FCSTD DOCUMENT  (FreeCAD 1.0R39319 (Git))
Label: lithography
License: All rights reserved
objects: App::Link×141, App::FeaturePython×32, Assembly::AssemblyLink×2, Assembly::JointGroup×1, Assembly::AssemblyObject×1
EXTERNAL_REF file=frame/frame.FCStd obj=Assembly
EXTERNAL_REF file=frame/frame.FCStd obj=_0x30_450_v3
EXTERNAL_REF file=frame/frame.FCStd obj=_0x30_550_v6
EXTERNAL_REF file=frame/frame.FCStd obj=_0x30_450
EXTERNAL_REF file=frame/frame.FCStd obj=_0x30_551
EXTERNAL_REF file=frame/frame.FCStd obj=_0x30_552
EXTERNAL_REF file=frame/frame.FCStd obj=_0x30_550
EXTERNAL_REF file=frame/frame.FCStd obj=_0x30_450_001
EXTERNAL_REF file=frame/frame.FCStd obj=_0x30_450_002
EXTERNAL_REF file=frame/frame.FCStd obj=_0x30_550_001
EXTERNAL_REF file=frame/frame.FCStd obj=_0x30_550_002
EXTERNAL_REF file=frame/frame.FCStd obj=_0x30_450_003
EXTERNAL_REF file=frame/frame.FCStd obj=_0x30_450_004
EXTERNAL_REF file=frame/frame.FCStd obj=_0_30_ANGLE_BRACKET_001
EXTERNAL_REF file=frame/frame.FCStd obj=_0_30_ANGLE_BRACKET_002
EXTERNAL_REF file=frame/frame.FCStd obj=_0_30_ANGLE_BRACKET_003
EXTERNAL_REF file=frame/frame.FCStd obj=_0_30_ANGLE_BRACKET_004
EXTERNAL_REF file=frame/frame.FCStd obj=_0_30_ANGLE_BRACKET_005
EXTERNAL_REF file=frame/frame.FCStd obj=_0_30_ANGLE_BRACKET_006
EXTERNAL_REF file=frame/frame.FCStd obj=_0_30_ANGLE_BRACKET_007
EXTERNAL_REF file=frame/frame.FCStd obj=_0_30_ANGLE_BRACKET_008
EXTERNAL_REF file=frame/frame.FCStd obj=_0_30_ANGLE_BRACKET_009
EXTERNAL_REF file=frame/frame.FCStd obj=_0_30_ANGLE_BRACKET_010
EXTERNAL_REF file=frame/frame.FCStd obj=_0_30_ANGLE_BRACKET_011
EXTERNAL_REF file=frame/frame.FCStd obj=_0_30_ANGLE_BRACKET_012
EXTERNAL_REF file=frame/frame.FCStd obj=_0_30_ANGLE_BRACKET_013
EXTERNAL_REF file=frame/frame.FCStd obj=_0_30_ANGLE_BRACKET_014
EXTERNAL_REF file=frame/frame.FCStd obj=_0_30_ANGLE_BRACKET_015
EXTERNAL_REF file=frame/frame.FCStd obj=_0_30_ANGLE_BRACKET_016
EXTERNAL_REF file=frame/frame.FCStd obj=_0_30_ANGLE_BRACKET_017
EXTERNAL_REF file=frame/frame.FCStd obj=_0_30_ANGLE_BRACKET_018
EXTERNAL_REF file=frame/frame.FCStd obj=_0_30_ANGLE_BRACKET_019
EXTERNAL_REF file=frame/frame.FCStd obj=_0_30_ANGLE_BRACKET_020
EXTERNAL_REF file=frame/frame.FCStd obj=_0_30_ANGLE_BRACKET_021
EXTERNAL_REF file=frame/frame.FCStd obj=_0_30_ANGLE_BRACKET_022
EXTERNAL_REF file=frame/frame.FCStd obj=_0_30_ANGLE_BRACKET_023
EXTERNAL_REF file=frame/frame.FCStd obj=_0_30_ANGLE_BRACKET_024
EXTERNAL_REF file=frame/frame.FCStd obj=_0x30_450_005
EXTERNAL_REF file=frame/frame.FCStd obj=_0x30_270_001
EXTERNAL_REF file=frame/frame.FCStd obj=_0x30_270_002
EXTERNAL_REF file=frame/frame.FCStd obj=_0x30_450_006
EXTERNAL_REF file=frame/frame.FCStd obj=_0x30_450_007
EXTERNAL_REF file=frame/frame.FCStd obj=_0x30_450_008
EXTERNAL_REF file=frame/frame.FCStd obj=_0_30_ANGLE_BRACKET_025
EXTERNAL_REF file=frame/frame.FCStd obj=_0_30_ANGLE_BRACKET_026
EXTERNAL_REF file=frame/frame.FCStd obj=_0_30_ANGLE_BRACKET_027
EXTERNAL_REF file=frame/frame.FCStd obj=_0_30_ANGLE_BRACKET_028
EXTERNAL_REF file=frame/frame.FCStd obj=_0_30_ANGLE_BRACKET_029
EXTERNAL_REF file=frame/frame.FCStd obj=_0_30_ANGLE_BRACKET_030
EXTERNAL_REF file=frame/frame.FCStd obj=_0_30_ANGLE_BRACKET_031
EXTERNAL_REF file=frame/frame.FCStd obj=_0_30_ANGLE_BRACKET_032
EXTERNAL_REF file=frame/frame.FCStd obj=_0x30_450_009
EXTERNAL_REF file=frame/frame.FCStd obj=_0x30_450_010
EXTERNAL_REF file=frame/frame.FCStd obj=_0_30_ANGLE_BRACKET_033
EXTERNAL_REF file=frame/frame.FCStd obj=_0_30_ANGLE_BRACKET_034
EXTERNAL_REF file=frame/frame.FCStd obj=_0_30_ANGLE_BRACKET_035
EXTERNAL_REF file=frame/frame.FCStd obj=_0_30_ANGLE_BRACKET_036
EXTERNAL_REF file=frame/frame.FCStd obj=_0_30_ANGLE_BRACKET_037
EXTERNAL_REF file=frame/frame.FCStd obj=_0_30_ANGLE_BRACKET_038
EXTERNAL_REF file=frame/frame.FCStd obj=_0_30_ANGLE_BRACKET_039
EXTERNAL_REF file=frame/frame.FCStd obj=_0_30_ANGLE_BRACKET_040
EXTERNAL_REF file=frame/frame.FCStd obj=_0_30_ANGLE_BRACKET_041
EXTERNAL_REF file=frame/frame.FCStd obj=_0_30_ANGLE_BRACKET_042
EXTERNAL_REF file=frame/frame.FCStd obj=_0_30_ANGLE_BRACKET_043
EXTERNAL_REF file=frame/frame.FCStd obj=_0_30_ANGLE_BRACKET_044
EXTERNAL_REF file=frame/frame.FCStd obj=_0x30_450_011
EXTERNAL_REF file=frame/frame.FCStd obj=_0_30_ANGLE_BRACKET_045
EXTERNAL_REF file=frame/frame.FCStd obj=_0_30_ANGLE_BRACKET_046
EXTERNAL_REF file=panels/plexi.FCStd obj=Part
EXTERNAL_REF file=panels/plexi.FCStd obj=Part002
EXTERNAL_REF file=panels/plexi-mount.FCStd obj=Part001
EXTERNAL_REF file=panels/plexi-mount.FCStd obj=Part
EXTERNAL_REF file=panels/plexi.FCStd obj=Part003
EXTERNAL_REF file=panels/plexi.FCStd obj=Part004
EXTERNAL_REF file=panels/plexi.FCStd obj=Part001
EXTERNAL_REF file=panels/plexi.FCStd obj=Part005
EXTERNAL_REF file=panels/plexi.FCStd obj=Part006
EXTERNAL_REF file=panels/plexi.FCStd obj=Part007
EXTERNAL_REF file=panels/plexi.FCStd obj=Part008
EXTERNAL_REF file=panels/plexi.FCStd obj=Part009
EXTERNAL_REF file=electronics/electronics-box.FCStd obj=Assembly
EXTERNAL_REF file=electronics/electronics-box.FCStd obj=alu_prof_3030_300_000
EXTERNAL_REF file=electronics/electronics-box.FCStd obj=alu_prof_3030_450_000
EXTERNAL_REF file=electronics/electronics-box.FCStd obj=alu_prof_3030_300_001
EXTERNAL_REF file=electronics/electronics-box.FCStd obj=alu_prof_3030_200_000
EXTERNAL_REF file=electronics/electronics-box.FCStd obj=alu_prof_3030_200_001
EXTERNAL_REF file=electronics/electronics-box.FCStd obj=alu_prof_3030_200_002
EXTERNAL_REF file=electronics/electronics-box.FCStd obj=alu_prof_3030_200_003
EXTERNAL_REF file=electronics/electronics-box.FCStd obj=alu_prof_3030_450_003
EXTERNAL_REF file=electronics/electronics-box.FCStd obj=_030_angle_bracket_000
EXTERNAL_REF file=electronics/electronics-box.FCStd obj=_030_angle_bracket_001
EXTERNAL_REF file=electronics/electronics-box.FCStd obj=_030_angle_bracket_002
EXTERNAL_REF file=electronics/electronics-box.FCStd obj=_030_angle_bracket_003
EXTERNAL_REF file=electronics/electronics-box.FCStd obj=_030_angle_bracket_004
EXTERNAL_REF file=electronics/electronics-box.FCStd obj=_030_angle_bracket_005
EXTERNAL_REF file=electronics/electronics-box.FCStd obj=_030_angle_bracket_006
EXTERNAL_REF file=electronics/electronics-box.FCStd obj=_030_angle_bracket_007
EXTERNAL_REF file=electronics/electronics-box.FCStd obj=_030_angle_bracket_008
EXTERNAL_REF file=electronics/electronics-box.FCStd obj=_030_angle_bracket_009
EXTERNAL_REF file=electronics/electronics-box.FCStd obj=_030_angle_bracket_010
EXTERNAL_REF file=electronics/electronics-box.FCStd obj=_030_angle_bracket_011
EXTERNAL_REF file=electronics/electronics-box.FCStd obj=_030_angle_bracket_012
EXTERNAL_REF file=electronics/electronics-box.FCStd obj=_030_angle_bracket_013
EXTERNAL_REF file=electronics/electronics-box.FCStd obj=_030_angle_bracket_014
EXTERNAL_REF file=electronics/electronics-box.FCStd obj=_030_angle_bracket_015
EXTERNAL_REF file=electronics/electronics-box.FCStd obj=din_mount_part
EXTERNAL_REF file=electronics/electronics-box.FCStd obj=din_mount_part001
EXTERNAL_REF file=electronics/electronics-box.FCStd obj=din_rail_180mm
EXTERNAL_REF file=electronics/electronics-box.FCStd obj=alu_prof_3030_450_004
EXTERNAL_REF file=electronics/electronics-box.FCStd obj=_030_angle_bracket_016
EXTERNAL_REF file=electronics/electronics-box.FCStd obj=_030_angle_bracket_017
EXTERNAL_REF file=electronics/electronics-box.FCStd obj=power_supply_bracket_part
EXTERNAL_REF file=electronics/electronics-box.FCStd obj=power_supply_bracket_part001
EXTERNAL_REF file=electronics/electronics-box.FCStd obj=LRS_154
EXTERNAL_REF file=electronics/electronics-box.FCStd obj=LRS_155
EXTERNAL_REF file=electronics/electronics-box.FCStd obj=dlp_power_supply_bracket_part
EXTERNAL_REF file=electronics/electronics-box.FCStd obj=smc100c_bracket_part
EXTERNAL_REF file=electronics/electronics-box.FCStd obj=smc100c_bracket_part001
EXTERNAL_REF file=electronics/electronics-box.FCStd obj=SMC100CC
EXTERNAL_REF file=electronics/electronics-box.FCStd obj=SMC100CC001
EXTERNAL_REF file=electronics/electronics-box.FCStd obj=ports_panel_part

FEATURE [App::Link] _0x30_450_v3  label="30x30 450 002"
  LinkPlacement = pos=(-180.5,79.4999,31.5001) rot=(0,1.00097,0;0rad)
  LinkedObject = -> <external frame/frame.FCStd>#_0x30_450_v3
  Placement = pos=(-180.5,79.4999,31.5001) rot=(0,1.00097,0;0rad)
FEATURE [App::Link] _0x30_550_v6  label="30x30 550 002"
  LinkPlacement = pos=(-145.5,79.4999,-33.4999) rot=(0,1,0;1.5708rad)
  LinkedObject = -> <external frame/frame.FCStd>#_0x30_550_v6
  Placement = pos=(-145.5,79.4999,-33.4999) rot=(0,1,0;1.5708rad)
FEATURE [App::Link] _0x30_450  label="30x30 450 005"
  LinkPlacement = pos=(339.5,79.4999,31.4999) rot=(0,1.00097,0;0rad)
  LinkedObject = -> <external frame/frame.FCStd>#_0x30_450
  Placement = pos=(339.5,79.4999,31.4999) rot=(0,1.00097,0;0rad)
FEATURE [App::Link] _0x30_551  label="30x30 450 003"
  LinkPlacement = pos=(339.5,494.5,-33.5001) rot=(1,0,0;1.5708rad)
  LinkedObject = -> <external frame/frame.FCStd>#_0x30_551
  Placement = pos=(339.5,494.5,-33.5001) rot=(1,0,0;1.5708rad)
FEATURE [App::Link] _0x30_552  label="30x30 450 004"
  LinkPlacement = pos=(339.5,494.5,446.5) rot=(0.57735,0.57735,-0.57735;2.0944rad)
  LinkedObject = -> <external frame/frame.FCStd>#_0x30_552
  Placement = pos=(339.5,494.5,446.5) rot=(0.57735,0.57735,-0.57735;2.0944rad)
FEATURE [App::Link] _0x30_550  label="30x30 550 003"
  LinkPlacement = pos=(304.5,79.4999,446.5) rot=(0,-1,0;1.5708rad)
  LinkedObject = -> <external frame/frame.FCStd>#_0x30_550
  Placement = pos=(304.5,79.4999,446.5) rot=(0,-1,0;1.5708rad)
FEATURE [App::Link] _0x30_450_001  label="30x30 450 006"
  LinkPlacement = pos=(-180.5,494.5,446.5) rot=(1,0,0;1.5708rad)
  LinkedObject = -> <external frame/frame.FCStd>#_0x30_450_001
  Placement = pos=(-180.5,494.5,446.5) rot=(1,0,0;1.5708rad)
FEATURE [App::Link] _0x30_450_002  label="30x30 450 007"
  LinkPlacement = pos=(-180.5,494.5,-33.4999) rot=(1,0,0;1.5708rad)
  LinkedObject = -> <external frame/frame.FCStd>#_0x30_450_002
  Placement = pos=(-180.5,494.5,-33.4999) rot=(1,0,0;1.5708rad)
FEATURE [App::Link] _0x30_550_001  label="30x30 550 004"
  LinkPlacement = pos=(-145.5,559.5,-33.4999) rot=(0,1,0;1.5708rad)
  LinkedObject = -> <external frame/frame.FCStd>#_0x30_550_001
  Placement = pos=(-145.5,559.5,-33.4999) rot=(0,1,0;1.5708rad)
FEATURE [App::Link] _0x30_550_002  label="30x30 550 005"
  LinkPlacement = pos=(304.5,559.5,446.5) rot=(0,-1,0;1.5708rad)
  LinkedObject = -> <external frame/frame.FCStd>#_0x30_550_002
  Placement = pos=(304.5,559.5,446.5) rot=(0,-1,0;1.5708rad)
FEATURE [App::Link] _0x30_450_003  label="30x30 450 008"
  LinkPlacement = pos=(339.5,559.5,31.4999) rot=(0,1.00097,0;0rad)
  LinkedObject = -> <external frame/frame.FCStd>#_0x30_450_003
  Placement = pos=(339.5,559.5,31.4999) rot=(0,1.00097,0;0rad)
FEATURE [App::Link] _0x30_450_004  label="30x30 450 009"
  LinkPlacement = pos=(-180.5,559.5,31.5001) rot=(0,1.00097,0;0rad)
  LinkedObject = -> <external frame/frame.FCStd>#_0x30_450_004
  Placement = pos=(-180.5,559.5,31.5001) rot=(0,1.00097,0;0rad)
FEATURE [App::Link] _0_30_ANGLE_BRACKET_001  label="30-30 ANGLE BRACKET 002"
  LinkPlacement = pos=(-165.5,79.2999,-0.999886) rot=(-0.57735,-0.57735,-0.57735;2.0944rad)
  LinkedObject = -> <external frame/frame.FCStd>#_0_30_ANGLE_BRACKET_001
  Placement = pos=(-165.5,79.2999,-0.999886) rot=(-0.57735,-0.57735,-0.57735;2.0944rad)
FEATURE [App::Link] _0_30_ANGLE_BRACKET_002  label="30-30 ANGLE BRACKET 003"
  LinkPlacement = pos=(-165.5,112,-33.2999) rot=(0.707107,0.707107,0;3.14159rad)
  LinkedObject = -> <external frame/frame.FCStd>#_0_30_ANGLE_BRACKET_002
  Placement = pos=(-165.5,112,-33.2999) rot=(0.707107,0.707107,0;3.14159rad)
FEATURE [App::Link] _0_30_ANGLE_BRACKET_003  label="30-30 ANGLE BRACKET 004"
  LinkPlacement = pos=(-180.7,112,-18.4999) rot=(0.57735,0.57735,0.57735;2.0944rad)
  LinkedObject = -> <external frame/frame.FCStd>#_0_30_ANGLE_BRACKET_003
  Placement = pos=(-180.7,112,-18.4999) rot=(0.57735,0.57735,0.57735;2.0944rad)
FEATURE [App::Link] _0_30_ANGLE_BRACKET_004  label="30-30 ANGLE BRACKET 005"
  LinkPlacement = pos=(-180.3,112,431.5) rot=(-0.57735,-0.57735,0.57735;2.0944rad)
  LinkedObject = -> <external frame/frame.FCStd>#_0_30_ANGLE_BRACKET_004
  Placement = pos=(-180.3,112,431.5) rot=(-0.57735,-0.57735,0.57735;2.0944rad)
FEATURE [App::Link] _0_30_ANGLE_BRACKET_005  label="30-30 ANGLE BRACKET 006"
  LinkPlacement = pos=(-180.7,544.5,-0.99988) rot=(0.707107,0,0.707107;3.14159rad)
  LinkedObject = -> <external frame/frame.FCStd>#_0_30_ANGLE_BRACKET_005
  Placement = pos=(-180.7,544.5,-0.99988) rot=(0.707107,0,0.707107;3.14159rad)
FEATURE [App::Link] _0_30_ANGLE_BRACKET_006  label="30-30 ANGLE BRACKET 007"
  LinkPlacement = pos=(-180.3,544.5,414) rot=(-0.707107,0,0.707107;3.14159rad)
  LinkedObject = -> <external frame/frame.FCStd>#_0_30_ANGLE_BRACKET_006
  Placement = pos=(-180.3,544.5,414) rot=(-0.707107,0,0.707107;3.14159rad)
FEATURE [App::Link] _0_30_ANGLE_BRACKET_007  label="30-30 ANGLE BRACKET 008"
  LinkPlacement = pos=(-165.5,79.5999,414) rot=(0.57735,0.57735,-0.57735;2.0944rad)
  LinkedObject = -> <external frame/frame.FCStd>#_0_30_ANGLE_BRACKET_007
  Placement = pos=(-165.5,79.5999,414) rot=(0.57735,0.57735,-0.57735;2.0944rad)
FEATURE [App::Link] _0_30_ANGLE_BRACKET_008  label="30-30 ANGLE BRACKET 009"
  LinkPlacement = pos=(324.5,79.2999,414) rot=(-0.57735,0.57735,0.57735;2.0944rad)
  LinkedObject = -> <external frame/frame.FCStd>#_0_30_ANGLE_BRACKET_008
  Placement = pos=(324.5,79.2999,414) rot=(-0.57735,0.57735,0.57735;2.0944rad)
FEATURE [App::Link] _0_30_ANGLE_BRACKET_009  label="30-30 ANGLE BRACKET 010"
  LinkPlacement = pos=(307,79.2999,-18.5001) rot=(0,0.707107,0.707107;3.14159rad)
  LinkedObject = -> <external frame/frame.FCStd>#_0_30_ANGLE_BRACKET_009
  Placement = pos=(307,79.2999,-18.5001) rot=(0,0.707107,0.707107;3.14159rad)
FEATURE [App::Link] _0_30_ANGLE_BRACKET_010  label="30-30 ANGLE BRACKET 011"
  LinkPlacement = pos=(307,544.5,-33.7001) rot=(0,0,1;3.14159rad)
  LinkedObject = -> <external frame/frame.FCStd>#_0_30_ANGLE_BRACKET_010
  Placement = pos=(307,544.5,-33.7001) rot=(0,0,1;3.14159rad)
FEATURE [App::Link] _0_30_ANGLE_BRACKET_011  label="30-30 ANGLE BRACKET 012"
  LinkPlacement = pos=(-165.5,527,-33.6999) rot=(0,0,1;4.71239rad)
  LinkedObject = -> <external frame/frame.FCStd>#_0_30_ANGLE_BRACKET_011
  Placement = pos=(-165.5,527,-33.6999) rot=(0,0,1;4.71239rad)
FEATURE [App::Link] _0_30_ANGLE_BRACKET_012  label="30-30 ANGLE BRACKET 013"
  LinkPlacement = pos=(307,94.4999,-33.7001) rot=(0,1,0;3.14159rad)
  LinkedObject = -> <external frame/frame.FCStd>#_0_30_ANGLE_BRACKET_012
  Placement = pos=(307,94.4999,-33.7001) rot=(0,1,0;3.14159rad)
FEATURE [App::Link] _0_30_ANGLE_BRACKET_013  label="30-30 ANGLE BRACKET 014"
  LinkPlacement = pos=(339.7,544.5,-1.00009) rot=(0.707107,0,0.707107;3.14159rad)
  LinkedObject = -> <external frame/frame.FCStd>#_0_30_ANGLE_BRACKET_013
  Placement = pos=(339.7,544.5,-1.00009) rot=(0.707107,0,0.707107;3.14159rad)
FEATURE [App::Link] _0_30_ANGLE_BRACKET_014  label="30-30 ANGLE BRACKET 015"
  LinkPlacement = pos=(339.7,112,-18.5001) rot=(0.57735,0.57735,0.57735;2.0944rad)
  LinkedObject = -> <external frame/frame.FCStd>#_0_30_ANGLE_BRACKET_014
  Placement = pos=(339.7,112,-18.5001) rot=(0.57735,0.57735,0.57735;2.0944rad)
FEATURE [App::Link] _0_30_ANGLE_BRACKET_015  label="30-30 ANGLE BRACKET 016"
  LinkPlacement = pos=(339.5,544.5,414) rot=(-0.707794,0,0.707795;3.14159rad)
  LinkedObject = -> <external frame/frame.FCStd>#_0_30_ANGLE_BRACKET_015
  Placement = pos=(339.5,544.5,414) rot=(-0.707794,0,0.707795;3.14159rad)
FEATURE [App::Link] _0_30_ANGLE_BRACKET_016  label="30-30 ANGLE BRACKET 017"
  LinkPlacement = pos=(339.9,112,431.5) rot=(-0.57735,-0.57735,0.57735;2.0944rad)
  LinkedObject = -> <external frame/frame.FCStd>#_0_30_ANGLE_BRACKET_016
  Placement = pos=(339.9,112,431.5) rot=(-0.57735,-0.57735,0.57735;2.0944rad)
FEATURE [App::Link] _0_30_ANGLE_BRACKET_017  label="30-30 ANGLE BRACKET 018"
  LinkPlacement = pos=(324.5,112,446.7) rot=(0,0,1;1.5708rad)
  LinkedObject = -> <external frame/frame.FCStd>#_0_30_ANGLE_BRACKET_017
  Placement = pos=(324.5,112,446.7) rot=(0,0,1;1.5708rad)
FEATURE [App::Link] _0_30_ANGLE_BRACKET_018  label="30-30 ANGLE BRACKET 019"
  LinkPlacement = pos=(-165.5,527,446.7) rot=(0,0,1;4.71239rad)
  LinkedObject = -> <external frame/frame.FCStd>#_0_30_ANGLE_BRACKET_018
  Placement = pos=(-165.5,527,446.7) rot=(0,0,1;4.71239rad)
FEATURE [App::Link] _0_30_ANGLE_BRACKET_019  label="30-30 ANGLE BRACKET 020"
  LinkPlacement = pos=(-165.5,112,446.7) rot=(-0.707107,-0.707107,0;3.14159rad)
  LinkedObject = -> <external frame/frame.FCStd>#_0_30_ANGLE_BRACKET_019
  Placement = pos=(-165.5,112,446.7) rot=(-0.707107,-0.707107,0;3.14159rad)
FEATURE [App::Link] _0_30_ANGLE_BRACKET_020  label="30-30 ANGLE BRACKET 021"
  LinkPlacement = pos=(324.5,527,446.6) rot=(0.707107,-0.707107,0;3.14159rad)
  LinkedObject = -> <external frame/frame.FCStd>#_0_30_ANGLE_BRACKET_020
  Placement = pos=(324.5,527,446.6) rot=(0.707107,-0.707107,0;3.14159rad)
FEATURE [App::Link] _0_30_ANGLE_BRACKET_021  label="30-30 ANGLE BRACKET 022"
  LinkPlacement = pos=(307,559.3,431.5) rot=(0,-0.707107,0.707107;3.14159rad)
  LinkedObject = -> <external frame/frame.FCStd>#_0_30_ANGLE_BRACKET_021
  Placement = pos=(307,559.3,431.5) rot=(0,-0.707107,0.707107;3.14159rad)
FEATURE [App::Link] _0_30_ANGLE_BRACKET_022  label="30-30 ANGLE BRACKET 023"
  LinkPlacement = pos=(307,559.7,-18.5001) rot=(0,-0.707107,-0.707107;3.14159rad)
  LinkedObject = -> <external frame/frame.FCStd>#_0_30_ANGLE_BRACKET_022
  Placement = pos=(307,559.7,-18.5001) rot=(0,-0.707107,-0.707107;3.14159rad)
FEATURE [App::Link] _0_30_ANGLE_BRACKET_023  label="30-30 ANGLE BRACKET 024"
  LinkPlacement = pos=(-165.5,559.7,-0.999886) rot=(0.57735,0.57735,0.57735;4.18879rad)
  LinkedObject = -> <external frame/frame.FCStd>#_0_30_ANGLE_BRACKET_023
  Placement = pos=(-165.5,559.7,-0.999886) rot=(0.57735,0.57735,0.57735;4.18879rad)
FEATURE [App::Link] _0_30_ANGLE_BRACKET_024  label="30-30 ANGLE BRACKET 025"
  LinkPlacement = pos=(-165.5,559.7,414) rot=(-0.57735,-0.57735,0.57735;4.18879rad)
  LinkedObject = -> <external frame/frame.FCStd>#_0_30_ANGLE_BRACKET_024
  Placement = pos=(-165.5,559.7,414) rot=(-0.57735,-0.57735,0.57735;4.18879rad)
FEATURE [App::Link] _0x30_450_005  label="30x30 450 010"
  LinkPlacement = pos=(-180.5,144.5,226.5) rot=(1,0,0;4.71239rad)
  LinkedObject = -> <external frame/frame.FCStd>#_0x30_450_005
  Placement = pos=(-180.5,144.5,226.5) rot=(1,0,0;4.71239rad)
FEATURE [App::Link] _0x30_270_001  label="30x30 270 002"
  LinkPlacement = pos=(54.5,229.5,226.5) rot=(0,1,0;4.71239rad)
  LinkedObject = -> <external frame/frame.FCStd>#_0x30_270_001
  Placement = pos=(54.5,229.5,226.5) rot=(0,1,0;4.71239rad)
FEATURE [App::Link] _0x30_270_002  label="30x30 270 003"
  LinkPlacement = pos=(54.5,314.5,226.5) rot=(0,1,0;4.71239rad)
  LinkedObject = -> <external frame/frame.FCStd>#_0x30_270_002
  Placement = pos=(54.5,314.5,226.5) rot=(0,1,0;4.71239rad)
FEATURE [App::Link] _0x30_450_006  label="30x30 450 011"
  LinkPlacement = pos=(119.5,494.5,226.5) rot=(-0.57735,0.57735,-0.57735;4.18879rad)
  LinkedObject = -> <external frame/frame.FCStd>#_0x30_450_006
  Placement = pos=(119.5,494.5,226.5) rot=(-0.57735,0.57735,-0.57735;4.18879rad)
FEATURE [App::Link] _0x30_450_007  label="30x30 450 012"
  LinkPlacement = pos=(119.5,79.4999,31.5) rot=(0,1.00375,0;0rad)
  LinkedObject = -> <external frame/frame.FCStd>#_0x30_450_007
  Placement = pos=(119.5,79.4999,31.5) rot=(0,1.00375,0;0rad)
FEATURE [App::Link] _0x30_450_008  label="30x30 450 013"
  LinkPlacement = pos=(119.5,559.5,31.5) rot=(0,-1.00375,0;6.28318rad)
  LinkedObject = -> <external frame/frame.FCStd>#_0x30_450_008
  Placement = pos=(119.5,559.5,31.5) rot=(0,-1.00375,0;6.28318rad)
FEATURE [App::Link] _0_30_ANGLE_BRACKET_025  label="30-30 ANGLE BRACKET 026"
  LinkPlacement = pos=(119.3,527,211.5) rot=(0.57735,-0.57735,0.57735;4.18879rad)
  LinkedObject = -> <external frame/frame.FCStd>#_0_30_ANGLE_BRACKET_025
  Placement = pos=(119.3,527,211.5) rot=(0.57735,-0.57735,0.57735;4.18879rad)
FEATURE [App::Link] _0_30_ANGLE_BRACKET_026  label="30-30 ANGLE BRACKET 027"
  LinkPlacement = pos=(-180.3,94.4999,194) rot=(0,1,0;1.5708rad)
  LinkedObject = -> <external frame/frame.FCStd>#_0_30_ANGLE_BRACKET_026
  Placement = pos=(-180.3,94.4999,194) rot=(0,1,0;1.5708rad)
FEATURE [App::Link] _0_30_ANGLE_BRACKET_027  label="30-30 ANGLE BRACKET 028"
  LinkPlacement = pos=(119.4,94.4999,194) rot=(0,1,0;1.5708rad)
  LinkedObject = -> <external frame/frame.FCStd>#_0_30_ANGLE_BRACKET_027
  Placement = pos=(119.4,94.4999,194) rot=(0,1,0;1.5708rad)
FEATURE [App::Link] _0_30_ANGLE_BRACKET_028  label="30-30 ANGLE BRACKET 029"
  LinkPlacement = pos=(-180.7,544.5,194) rot=(0.707107,0,-0.707107;3.14159rad)
  LinkedObject = -> <external frame/frame.FCStd>#_0_30_ANGLE_BRACKET_028
  Placement = pos=(-180.7,544.5,194) rot=(0.707107,0,-0.707107;3.14159rad)
FEATURE [App::Link] _0_30_ANGLE_BRACKET_029  label="30-30 ANGLE BRACKET 030"
  LinkPlacement = pos=(-165.5,197,226.7) rot=(0,0,-1;1.5708rad)
  LinkedObject = -> <external frame/frame.FCStd>#_0_30_ANGLE_BRACKET_029
  Placement = pos=(-165.5,197,226.7) rot=(0,0,-1;1.5708rad)
FEATURE [App::Link] _0_30_ANGLE_BRACKET_030  label="30-30 ANGLE BRACKET 031"
  LinkPlacement = pos=(-148,329.5,226.7) rot=(0,1.00375,0;0rad)
  LinkedObject = -> <external frame/frame.FCStd>#_0_30_ANGLE_BRACKET_030
  Placement = pos=(-148,329.5,226.7) rot=(0,1.00375,0;0rad)
FEATURE [App::Link] _0_30_ANGLE_BRACKET_031  label="30-30 ANGLE BRACKET 032"
  LinkPlacement = pos=(104.5,347,226.7) rot=(0,0,1;1.5708rad)
  LinkedObject = -> <external frame/frame.FCStd>#_0_30_ANGLE_BRACKET_031
  Placement = pos=(104.5,347,226.7) rot=(0,0,1;1.5708rad)
FEATURE [App::Link] _0_30_ANGLE_BRACKET_032  label="30-30 ANGLE BRACKET 033"
  LinkPlacement = pos=(87,214.5,226.7) rot=(0,0,-1;3.14159rad)
  LinkedObject = -> <external frame/frame.FCStd>#_0_30_ANGLE_BRACKET_032
  Placement = pos=(87,214.5,226.7) rot=(0,0,-1;3.14159rad)
FEATURE [App::Link] _0x30_450_009  label="30x30 450 014"
  LinkPlacement = pos=(229.5,144.5,-33.7) rot=(-1,0,0;1.5708rad)
  LinkedObject = -> <external frame/frame.FCStd>#_0x30_450_009
  Placement = pos=(229.5,144.5,-33.7) rot=(-1,0,0;1.5708rad)
FEATURE [App::Link] _0x30_450_010  label="30x30 450 015"
  LinkPlacement = pos=(149.5,494.5,-33.7) rot=(-1,0,0;4.71239rad)
  LinkedObject = -> <external frame/frame.FCStd>#_0x30_450_010
  Placement = pos=(149.5,494.5,-33.7) rot=(-1,0,0;4.71239rad)
FEATURE [App::Link] _0_30_ANGLE_BRACKET_033  label="30-30 ANGLE BRACKET 034"
  LinkPlacement = pos=(134.5,79.2999,-1.00001) rot=(0.579515,0.579515,0.579515;4.18879rad)
  LinkedObject = -> <external frame/frame.FCStd>#_0_30_ANGLE_BRACKET_033
  Placement = pos=(134.5,79.2999,-1.00001) rot=(0.579515,0.579515,0.579515;4.18879rad)
FEATURE [App::Link] _0_30_ANGLE_BRACKET_034  label="30-30 ANGLE BRACKET 035"
  LinkPlacement = pos=(86.9999,79.2999,-18.5) rot=(0,-0.709758,-0.709758;3.14159rad)
  LinkedObject = -> <external frame/frame.FCStd>#_0_30_ANGLE_BRACKET_034
  Placement = pos=(86.9999,79.2999,-18.5) rot=(0,-0.709758,-0.709758;3.14159rad)
FEATURE [App::Link] _0_30_ANGLE_BRACKET_035  label="30-30 ANGLE BRACKET 036"
  LinkPlacement = pos=(104.5,79.6999,414) rot=(0.579515,-0.579515,-0.579515;4.18879rad)
  LinkedObject = -> <external frame/frame.FCStd>#_0_30_ANGLE_BRACKET_035
  Placement = pos=(104.5,79.6999,414) rot=(0.579515,-0.579515,-0.579515;4.18879rad)
FEATURE [App::Link] _0_30_ANGLE_BRACKET_036  label="30-30 ANGLE BRACKET 037"
  LinkPlacement = pos=(152,79.3999,431.5) rot=(1.00375,0,0;4.71239rad)
  LinkedObject = -> <external frame/frame.FCStd>#_0_30_ANGLE_BRACKET_036
  Placement = pos=(152,79.3999,431.5) rot=(1.00375,0,0;4.71239rad)
FEATURE [App::Link] _0_30_ANGLE_BRACKET_037  label="30-30 ANGLE BRACKET 038"
  LinkPlacement = pos=(117,544.5,-33.5) rot=(0,0,1;3.14159rad)
  LinkedObject = -> <external frame/frame.FCStd>#_0_30_ANGLE_BRACKET_037
  Placement = pos=(117,544.5,-33.5) rot=(0,0,1;3.14159rad)
FEATURE [App::Link] _0_30_ANGLE_BRACKET_038  label="30-30 ANGLE BRACKET 039"
  LinkPlacement = pos=(134.5,112,-33.5) rot=(0,0,1;1.5708rad)
  LinkedObject = -> <external frame/frame.FCStd>#_0_30_ANGLE_BRACKET_038
  Placement = pos=(134.5,112,-33.5) rot=(0,0,1;1.5708rad)
FEATURE [App::Link] _0_30_ANGLE_BRACKET_039  label="30-30 ANGLE BRACKET 040"
  LinkPlacement = pos=(262,94.4999,-33.9001) rot=(0,1.00375,0;0rad)
  LinkedObject = -> <external frame/frame.FCStd>#_0_30_ANGLE_BRACKET_039
  Placement = pos=(262,94.4999,-33.9001) rot=(0,1.00375,0;0rad)
FEATURE [App::Link] _0_30_ANGLE_BRACKET_040  label="30-30 ANGLE BRACKET 041"
  LinkPlacement = pos=(244.5,527,-33.9001) rot=(0,0,1;4.71239rad)
  LinkedObject = -> <external frame/frame.FCStd>#_0_30_ANGLE_BRACKET_040
  Placement = pos=(244.5,527,-33.9001) rot=(0,0,1;4.71239rad)
FEATURE [App::Link] _0_30_ANGLE_BRACKET_041  label="30-30 ANGLE BRACKET 042"
  LinkPlacement = pos=(134.5,559.7,-1.00001) rot=(-0.579515,-0.579515,-0.579515;2.0944rad)
  LinkedObject = -> <external frame/frame.FCStd>#_0_30_ANGLE_BRACKET_041
  Placement = pos=(134.5,559.7,-1.00001) rot=(-0.579515,-0.579515,-0.579515;2.0944rad)
FEATURE [App::Link] _0_30_ANGLE_BRACKET_042  label="30-30 ANGLE BRACKET 043"
  LinkPlacement = pos=(86.9999,559.6,-18.5) rot=(0,0.709758,0.709758;3.14159rad)
  LinkedObject = -> <external frame/frame.FCStd>#_0_30_ANGLE_BRACKET_042
  Placement = pos=(86.9999,559.6,-18.5) rot=(0,0.709758,0.709758;3.14159rad)
FEATURE [App::Link] _0_30_ANGLE_BRACKET_043  label="30-30 ANGLE BRACKET 044"
  LinkPlacement = pos=(87,559.7,431.5) rot=(0,0.709758,-0.709758;3.14159rad)
  LinkedObject = -> <external frame/frame.FCStd>#_0_30_ANGLE_BRACKET_043
  Placement = pos=(87,559.7,431.5) rot=(0,0.709758,-0.709758;3.14159rad)
FEATURE [App::Link] _0_30_ANGLE_BRACKET_044  label="30-30 ANGLE BRACKET 045"
  LinkPlacement = pos=(134.5,559.3,414) rot=(0.579515,0.579515,-0.579515;2.0944rad)
  LinkedObject = -> <external frame/frame.FCStd>#_0_30_ANGLE_BRACKET_044
  Placement = pos=(134.5,559.3,414) rot=(0.579515,0.579515,-0.579515;2.0944rad)
FEATURE [App::Link] _0x30_450_011  label="30x30 450 016"
  LinkPlacement = pos=(119.5,144.5,446.5) rot=(1,0,0;4.71239rad)
  LinkedObject = -> <external frame/frame.FCStd>#_0x30_450_011
  Placement = pos=(119.5,144.5,446.5) rot=(1,0,0;4.71239rad)
FEATURE [App::Link] _0_30_ANGLE_BRACKET_045  label="30-30 ANGLE BRACKET 046"
  LinkPlacement = pos=(119.2,112,431.5) rot=(-0.57735,-0.57735,0.57735;2.0944rad)
  LinkedObject = -> <external frame/frame.FCStd>#_0_30_ANGLE_BRACKET_045
  Placement = pos=(119.2,112,431.5) rot=(-0.57735,-0.57735,0.57735;2.0944rad)
FEATURE [App::Link] _0_30_ANGLE_BRACKET_046  label="30-30 ANGLE BRACKET 047"
  LinkPlacement = pos=(119.8,544.5,414) rot=(0.707107,0,-0.707107;3.14159rad)
  LinkedObject = -> <external frame/frame.FCStd>#_0_30_ANGLE_BRACKET_046
  Placement = pos=(119.8,544.5,414) rot=(0.707107,0,-0.707107;3.14159rad)
FEATURE [Assembly::AssemblyLink] frame_assembly  label="frame-assembly"
  Group = -> [_0x30_450_v3,_0x30_550_v6,_0x30_450,_0x30_551,_0x30_552,_0x30_550,_0x30_450_001,_0x30_450_002,_0x30_550_001,_0x30_550_002,_0x30_450_003,_0x30_450_004,_0_30_ANGLE_BRACKET_001,_0_30_ANGLE_BRACKET_002,_0_30_ANGLE_BRACKET_003,_0_30_ANGLE_BRACKET_004,_0_30_ANGLE_BRACKET_005,_0_30_ANGLE_BRACKET_006,_0_30_ANGLE_BRACKET_007,_0_30_ANGLE_BRACKET_008,_0_30_ANGLE_BRACKET_009,_0_30_ANGLE_BRACKET_010,+45 more]
  LinkedObject = -> <external frame/frame.FCStd>#Assembly
  Origin = -> Origin001
  Rigid = true
FEATURE [App::FeaturePython] GroundedJoint  # Assembly grounded joint (typed FeaturePython)
  ObjectToGround = -> frame_assembly
FEATURE [App::Link] plexi_472x212_body001  label="plexi-472x212-body001"
  LinkPlacement = pos=(229.5,577.6,206.5) rot=(1,0,0;1.5708rad)
  LinkedObject = -> <external panels/plexi.FCStd>#Part
  Placement = pos=(229.5,577.6,206.5) rot=(1,0,0;1.5708rad)
FEATURE [App::Link] plexi_471_2x471_2_body  label="plexi-471.2x471.2-body"
  LinkPlacement = pos=(357.7,319.9,206.9) rot=(-0.707107,0,0.707107;3.14159rad)
  LinkedObject = -> <external panels/plexi.FCStd>#Part002
  Placement = pos=(357.7,319.9,206.9) rot=(-0.707107,0,0.707107;3.14159rad)
FEATURE [App::Link] middle_plexi_mount_part  label="middle-plexi-mount-part"
  LinkPlacement = pos=(104.5,580.7,-48.5) rot=(1,0,0;1.5708rad)
  LinkedObject = -> <external panels/plexi-mount.FCStd>#Part001
  Placement = pos=(104.5,580.7,-48.5) rot=(1,0,0;1.5708rad)
FEATURE [App::Link] corner_plexi_mount_part  label="corner-plexi-mount-part"
  LinkPlacement = pos=(354.5,580.7,-48.5001) rot=(0.57735,-0.57735,0.57735;2.0944rad)
  LinkedObject = -> <external panels/plexi-mount.FCStd>#Part
  Placement = pos=(354.5,580.7,-48.5001) rot=(0.57735,-0.57735,0.57735;2.0944rad)
FEATURE [App::FeaturePython] Joint  label="Fixed"  # Assembly joint (typed FeaturePython)
  Activated = true
  AngleMax = 0
  AngleMin = 0
  Detach1 = false
  Detach2 = false
  Distance = 0
  Distance2 = 0
  EnableAngleMax = false
  EnableAngleMin = false
  EnableLengthMax = false
  EnableLengthMin = false
  JointType = 0 (Fixed)
  LengthMax = 0
  LengthMin = 0
  Offset2 = pos=(0,0,13.8) rot=(0,0,-1;1.5708rad)
  Placement1 = pos=(37.5,0,6.2) rot=(-0.707107,0,0.707107;3.14159rad)
  Placement2 = pos=(-22.5,15,500) rot=(-0.57735,-0.57735,0.57735;2.0944rad)
  Reference1 = -> Assembly [corner_plexi_mount_part.Body.Edge29,corner_plexi_mount_part.Body.Edge29]
  Reference2 = -> Assembly [frame_assembly._0x30_550_001.Edge44,frame_assembly._0x30_550_001.Edge44]
FEATURE [App::FeaturePython] Joint005  label="Fixed004"  # Assembly joint (typed FeaturePython)
  Activated = true
  AngleMax = 0
  AngleMin = 0
  Detach1 = false
  Detach2 = false
  Distance = 0
  Distance2 = 0
  EnableAngleMax = false
  EnableAngleMin = false
  EnableLengthMax = false
  EnableLengthMin = false
  JointType = 0 (Fixed)
  LengthMax = 0
  LengthMin = 0
  Offset2 = pos=(0,0,0) rot=(0,0,-1;1.5708rad)
  Placement1 = pos=(106,-236,1.5) rot=(0,0,1;0rad)
  Placement2 = pos=(19,19,4.6) rot=(0,0,-1;1.5708rad)
  Reference1 = -> Assembly [plexi_472x212_body001.Body.Edge2,plexi_472x212_body001.Body.Edge2]
  Reference2 = -> Assembly [corner_plexi_mount_part.Body.Edge27,corner_plexi_mount_part.Body.Edge27]
FEATURE [App::Link] corner_plexi_mount_part001  label="corner-plexi-mount-part001"
  LinkPlacement = pos=(354.5,580.7,461.5) rot=(0,0.707107,-0.707107;3.14159rad)
  LinkedObject = -> <external panels/plexi-mount.FCStd>#Part
  Placement = pos=(354.5,580.7,461.5) rot=(0,0.707107,-0.707107;3.14159rad)
FEATURE [App::FeaturePython] Joint006  label="Fixed005"  # Assembly joint (typed FeaturePython)
  Activated = true
  AngleMax = 0
  AngleMin = 0
  Detach1 = false
  Detach2 = false
  Distance = 0
  Distance2 = 0
  EnableAngleMax = false
  EnableAngleMin = false
  EnableLengthMax = false
  EnableLengthMin = false
  JointType = 0 (Fixed)
  LengthMax = 0
  LengthMin = 0
  Offset2 = pos=(0,0,31.2) rot=(0,0,1;1.5708rad)
  Placement1 = pos=(0,37.5,6.2) rot=(0.57735,0.57735,0.57735;4.18879rad)
  Placement2 = pos=(-22.5,15,-50) rot=(-0.57735,0.57735,0.57735;4.18879rad)
  Reference1 = -> Assembly [corner_plexi_mount_part001.Body.Edge25,corner_plexi_mount_part001.Body.Edge25]
  Reference2 = -> Assembly [frame_assembly._0x30_550_002.Edge195,frame_assembly._0x30_550_002.Edge195]
FEATURE [App::FeaturePython] Joint007  label="Fixed006"  # Assembly joint (typed FeaturePython)
  Activated = true
  AngleMax = 0
  AngleMin = 0
  Detach1 = false
  Detach2 = false
  Distance = 0
  Distance2 = 0
  EnableAngleMax = false
  EnableAngleMin = false
  EnableLengthMax = false
  EnableLengthMin = false
  JointType = 0 (Fixed)
  LengthMax = 0
  LengthMin = 0
  Placement1 = pos=(19,19,4.6) rot=(0,0,1;0rad)
  Placement2 = pos=(-106,-236,1.5) rot=(0,0,1;0rad)
  Reference1 = -> Assembly [middle_plexi_mount_part.Body001.Edge31,middle_plexi_mount_part.Body001.Edge31]
  Reference2 = -> Assembly [plexi_472x212_body001.Body.Edge1,plexi_472x212_body001.Body.Edge1]
FEATURE [App::Link] middle_plexi_mount_part001  label="middle-plexi-mount-part001"
  LinkPlacement = pos=(134.5,580.7,461.5) rot=(0,0.707107,-0.707107;3.14159rad)
  LinkedObject = -> <external panels/plexi-mount.FCStd>#Part001
  Placement = pos=(134.5,580.7,461.5) rot=(0,0.707107,-0.707107;3.14159rad)
FEATURE [App::FeaturePython] Joint008  label="Fixed007"  # Assembly joint (typed FeaturePython)
  Activated = true
  AngleMax = 0
  AngleMin = 0
  Detach1 = false
  Detach2 = false
  Distance = 0
  Distance2 = 0
  EnableAngleMax = false
  EnableAngleMin = false
  EnableLengthMax = false
  EnableLengthMin = false
  JointType = 0 (Fixed)
  LengthMax = 0
  LengthMin = 0
  Offset2 = pos=(0,0,0) rot=(0,0,1;3.14159rad)
  Placement1 = pos=(11,19,4.6) rot=(0,0,1;0rad)
  Placement2 = pos=(-106,236,1.5) rot=(0,0,1;3.14159rad)
  Reference1 = -> Assembly [middle_plexi_mount_part001.Body001.Edge58,middle_plexi_mount_part001.Body001.Edge58]
  Reference2 = -> Assembly [plexi_472x212_body001.Body.Edge8,plexi_472x212_body001.Body.Edge8]
FEATURE [App::Link] corner_plexi_mount_part002  label="corner-plexi-mount-part002"
  LinkPlacement = pos=(360.7,574.5,461.5) rot=(-0.707107,0,0.707107;3.14159rad)
  LinkedObject = -> <external panels/plexi-mount.FCStd>#Part
  Placement = pos=(360.7,574.5,461.5) rot=(-0.707107,0,0.707107;3.14159rad)
FEATURE [App::FeaturePython] Joint009  label="Fixed008"  # Assembly joint (typed FeaturePython)
  Activated = true
  AngleMax = 0
  AngleMin = 0
  Detach1 = false
  Detach2 = false
  Distance = 0
  Distance2 = 0
  EnableAngleMax = false
  EnableAngleMin = false
  EnableLengthMax = false
  EnableLengthMin = false
  JointType = 0 (Fixed)
  LengthMax = 0
  LengthMin = 0
  Offset2 = pos=(0,0,0) rot=(0,0,-1;1.5708rad)
  Placement1 = pos=(37.5,0,6.2) rot=(-0.707107,0,0.707107;3.14159rad)
  Placement2 = pos=(0,37.5,6.2) rot=(0,0.707107,0.707107;3.14159rad)
  Reference1 = -> Assembly [corner_plexi_mount_part002.Body.Edge29,corner_plexi_mount_part002.Body.Edge29]
  Reference2 = -> Assembly [corner_plexi_mount_part001.Body.Edge25,corner_plexi_mount_part001.Body.Edge25]
FEATURE [App::FeaturePython] Joint010  label="Fixed009"  # Assembly joint (typed FeaturePython)
  Activated = true
  AngleMax = 0
  AngleMin = 0
  Detach1 = false
  Detach2 = false
  Distance = 0
  Distance2 = 0
  EnableAngleMax = false
  EnableAngleMin = false
  EnableLengthMax = false
  EnableLengthMin = false
  JointType = 0 (Fixed)
  LengthMax = 0
  LengthMin = 0
  Placement1 = pos=(-235.6,-235.6,0) rot=(0,0,1;0rad)
  Placement2 = pos=(19,19,3) rot=(0,0,1;0rad)
  Reference1 = -> Assembly [plexi_471_2x471_2_body.Body002.Edge1,plexi_471_2x471_2_body.Body002.Vertex1]
  Reference2 = -> Assembly [corner_plexi_mount_part002.Body.Edge27,corner_plexi_mount_part002.Body.Vertex20]
FEATURE [App::Link] corner_plexi_mount_part003  label="corner-plexi-mount-part003"
  LinkPlacement = pos=(360.8,64.4999,461.5) rot=(-0.57735,-0.57735,0.57735;2.0944rad)
  LinkedObject = -> <external panels/plexi-mount.FCStd>#Part
  Placement = pos=(360.8,64.4999,461.5) rot=(-0.57735,-0.57735,0.57735;2.0944rad)
FEATURE [App::FeaturePython] Joint011  label="Fixed010"  # Assembly joint (typed FeaturePython)
  Activated = true
  AngleMax = 0
  AngleMin = 0
  Detach1 = false
  Detach2 = false
  Distance = 0
  Distance2 = 0
  EnableAngleMax = false
  EnableAngleMin = false
  EnableLengthMax = false
  EnableLengthMin = false
  JointType = 0 (Fixed)
  LengthMax = 0
  LengthMin = 0
  Offset1 = pos=(0.8,0,0) rot=(0,0,1;0rad)
  Offset2 = pos=(0,0,0) rot=(0,0,-1;1.5708rad)
  Placement1 = pos=(19.8,19,4.6) rot=(0,0,1;0rad)
  Placement2 = pos=(-235.6,235.6,1.5) rot=(0,0,-1;1.5708rad)
  Reference1 = -> Assembly [corner_plexi_mount_part003.Body.Edge27,corner_plexi_mount_part003.Body.Edge27]
  Reference2 = -> Assembly [plexi_471_2x471_2_body.Body002.Edge8,plexi_471_2x471_2_body.Body002.Edge8]
FEATURE [App::Link] corner_plexi_mount_part004  label="corner-plexi-mount-part004"
  LinkPlacement = pos=(360.7,574.5,-48.5001) rot=(-0.57735,0.57735,0.57735;4.18879rad)
  LinkedObject = -> <external panels/plexi-mount.FCStd>#Part
  Placement = pos=(360.7,574.5,-48.5001) rot=(-0.57735,0.57735,0.57735;4.18879rad)
FEATURE [App::Link] corner_plexi_mount_part005  label="corner-plexi-mount-part005"
  LinkPlacement = pos=(360.8,64.4999,-48.5001) rot=(0,-1,0;1.5708rad)
  LinkedObject = -> <external panels/plexi-mount.FCStd>#Part
  Placement = pos=(360.8,64.4999,-48.5001) rot=(0,-1,0;1.5708rad)
FEATURE [App::FeaturePython] Joint012  label="Fixed011"  # Assembly joint (typed FeaturePython)
  Activated = true
  AngleMax = 0
  AngleMin = 0
  Detach1 = false
  Detach2 = false
  Distance = 0
  Distance2 = 0
  EnableAngleMax = false
  EnableAngleMin = false
  EnableLengthMax = false
  EnableLengthMin = false
  JointType = 0 (Fixed)
  LengthMax = 0
  LengthMin = 0
  Offset1 = pos=(0.8,0.8,0) rot=(0,0,1;0rad)
  Offset2 = pos=(0,0,0) rot=(0,0,1;3.14159rad)
  Placement1 = pos=(19.8,19.8,4.6) rot=(0,0,1;0rad)
  Placement2 = pos=(235.6,235.6,1.5) rot=(0,0,1;3.14159rad)
  Reference1 = -> Assembly [corner_plexi_mount_part005.Body.Edge27,corner_plexi_mount_part005.Body.Edge27]
  Reference2 = -> Assembly [plexi_471_2x471_2_body.Body002.Edge5,plexi_471_2x471_2_body.Body002.Edge5]
FEATURE [App::FeaturePython] Joint013  label="Fixed012"  # Assembly joint (typed FeaturePython)
  Activated = true
  AngleMax = 0
  AngleMin = 0
  Detach1 = false
  Detach2 = false
  Distance = 0
  Distance2 = 0
  EnableAngleMax = false
  EnableAngleMin = false
  EnableLengthMax = false
  EnableLengthMin = false
  JointType = 0 (Fixed)
  LengthMax = 0
  LengthMin = 0
  Offset2 = pos=(0,0,-75) rot=(0,0,-1;1.5708rad)
  Placement1 = pos=(0,75,6.2) rot=(0.57735,0.57735,0.57735;4.18879rad)
  Placement2 = pos=(75,0,6.2) rot=(-0.57735,-0.57735,0.57735;2.0944rad)
  Reference1 = -> Assembly [corner_plexi_mount_part004.Body.Edge25,corner_plexi_mount_part004.Body.Vertex6]
  Reference2 = -> Assembly [corner_plexi_mount_part.Body.Edge29,corner_plexi_mount_part.Body.Vertex21]
FEATURE [App::Link] corner_plexi_mount_part006  label="corner-plexi-mount-part006"
  LinkPlacement = pos=(354.5,574.5,467.7) rot=(-0.707107,0.707107,0;3.14159rad)
  LinkedObject = -> <external panels/plexi-mount.FCStd>#Part
  Placement = pos=(354.5,574.5,467.7) rot=(-0.707107,0.707107,0;3.14159rad)
FEATURE [App::FeaturePython] Joint014  label="Fixed013"  # Assembly joint (typed FeaturePython)
  Activated = true
  AngleMax = 0
  AngleMin = 0
  Detach1 = false
  Detach2 = false
  Distance = 0
  Distance2 = 0
  EnableAngleMax = false
  EnableAngleMin = false
  EnableLengthMax = false
  EnableLengthMin = false
  JointType = 0 (Fixed)
  LengthMax = 0
  LengthMin = 0
  Offset2 = pos=(0,0,37.5) rot=(0,0,-1;1.5708rad)
  Placement1 = pos=(37.5,0,6.2) rot=(-0.707107,0,0.707107;3.14159rad)
  Placement2 = pos=(0,37.5,6.2) rot=(0,0.707107,0.707107;3.14159rad)
  Reference1 = -> Assembly [corner_plexi_mount_part006.Body.Edge29,corner_plexi_mount_part006.Body.Edge29]
  Reference2 = -> Assembly [corner_plexi_mount_part002.Body.Edge25,corner_plexi_mount_part002.Body.Vertex21]
FEATURE [App::Link] plexi_top_471_2x211_2_part  label="plexi-top-471.2x211.2-part"
  LinkPlacement = pos=(229.9,319.9,461.6) rot=(0,1.00097,0;0rad)
  LinkedObject = -> <external panels/plexi.FCStd>#Part003
  Placement = pos=(229.9,319.9,461.6) rot=(0,1.00097,0;0rad)
FEATURE [App::FeaturePython] Joint015  label="Fixed014"  # Assembly joint (typed FeaturePython)
  Activated = true
  AngleMax = 0
  AngleMin = 0
  Detach1 = false
  Detach2 = false
  Distance = 0
  Distance2 = 0
  EnableAngleMax = false
  EnableAngleMin = false
  EnableLengthMax = false
  EnableLengthMin = false
  JointType = 0 (Fixed)
  LengthMax = 0
  LengthMin = 0
  Offset2 = pos=(0,0,0) rot=(0,0,-1;1.5708rad)
  Placement1 = pos=(105.6,235.6,1.5) rot=(0,0,1;0rad)
  Placement2 = pos=(19,19,4.6) rot=(0,0,-1;1.5708rad)
  Reference1 = -> Assembly [plexi_top_471_2x211_2_part.Body003.Edge5,plexi_top_471_2x211_2_part.Body003.Edge5]
  Reference2 = -> Assembly [corner_plexi_mount_part006.Body.Edge27,corner_plexi_mount_part006.Body.Edge27]
FEATURE [App::Link] corner_plexi_mount_part007  label="corner-plexi-mount-part007"
  LinkPlacement = pos=(354.6,64.4999,467.7) rot=(0,1,0;3.14159rad)
  LinkedObject = -> <external panels/plexi-mount.FCStd>#Part
  Placement = pos=(354.6,64.4999,467.7) rot=(0,1,0;3.14159rad)
FEATURE [App::FeaturePython] Joint016  label="Fixed015"  # Assembly joint (typed FeaturePython)
  Activated = true
  AngleMax = 0
  AngleMin = 0
  Detach1 = false
  Detach2 = false
  Distance = 0
  Distance2 = 0
  EnableAngleMax = false
  EnableAngleMin = false
  EnableLengthMax = false
  EnableLengthMin = false
  JointType = 0 (Fixed)
  LengthMax = 0
  LengthMin = 0
  Offset2 = pos=(0,0,0) rot=(0,0,-1;1.5708rad)
  Placement1 = pos=(0,37.5,6.2) rot=(0.57735,0.57735,0.57735;4.18879rad)
  Placement2 = pos=(37.5,0,6.2) rot=(-0.57735,-0.57735,0.57735;2.0944rad)
  Reference1 = -> Assembly [corner_plexi_mount_part007.Body.Edge25,corner_plexi_mount_part007.Body.Edge25]
  Reference2 = -> Assembly [corner_plexi_mount_part003.Body.Edge29,corner_plexi_mount_part003.Body.Edge29]
FEATURE [App::Link] middle_plexi_mount_part002  label="middle-plexi-mount-part002"
  LinkPlacement = pos=(104.5,574.5,467.7) rot=(1,0,0;3.14159rad)
  LinkedObject = -> <external panels/plexi-mount.FCStd>#Part001
  Placement = pos=(104.5,574.5,467.7) rot=(1,0,0;3.14159rad)
FEATURE [App::FeaturePython] Joint017  label="Fixed016"  # Assembly joint (typed FeaturePython)
  Activated = true
  AngleMax = 0
  AngleMin = 0
  Detach1 = false
  Detach2 = false
  Distance = 0
  Distance2 = 0
  EnableAngleMax = false
  EnableAngleMin = false
  EnableLengthMax = false
  EnableLengthMin = false
  JointType = 0 (Fixed)
  LengthMax = 0
  LengthMin = 0
  Offset2 = pos=(0,0,0) rot=(0,0,1;1.5708rad)
  Placement1 = pos=(75,0,6.2) rot=(-0.707107,0,0.707107;3.14159rad)
  Placement2 = pos=(-45,0,6.2) rot=(-0.57735,0.57735,0.57735;4.18879rad)
  Reference1 = -> Assembly [middle_plexi_mount_part002.Body001.Edge29,middle_plexi_mount_part002.Body001.Vertex6]
  Reference2 = -> Assembly [middle_plexi_mount_part001.Body001.Edge29,middle_plexi_mount_part001.Body001.Vertex25]
FEATURE [App::Link] middle_plexi_mount_part003  label="middle-plexi-mount-part003"
  LinkPlacement = pos=(134.5,64.4999,467.697) rot=(0,1,0;3.14159rad)
  LinkedObject = -> <external panels/plexi-mount.FCStd>#Part001
  Placement = pos=(134.5,64.4999,467.697) rot=(0,1,0;3.14159rad)
FEATURE [App::FeaturePython] Joint018  label="Fixed017"  # Assembly joint (typed FeaturePython)
  Activated = true
  AngleMax = 0
  AngleMin = 0
  Detach1 = false
  Detach2 = false
  Distance = 0
  Distance2 = 0
  EnableAngleMax = false
  EnableAngleMin = false
  EnableLengthMax = false
  EnableLengthMin = false
  JointType = 0 (Fixed)
  LengthMax = 0
  LengthMin = 0
  Offset1 = pos=(0.5,4,360) rot=(0,0,1;0rad)
  Placement1 = pos=(19,435,2.99698) rot=(0.57735,0.57735,0.57735;4.18879rad)
  Placement2 = pos=(11,75,3) rot=(0.57735,0.57735,0.57735;4.18879rad)
  Reference1 = -> Assembly [middle_plexi_mount_part003.Body001.Face13,middle_plexi_mount_part003.Body001.Face13]
  Reference2 = -> Assembly [middle_plexi_mount_part002.Body001.Face13,middle_plexi_mount_part002.Body001.Vertex38]
FEATURE [App::Link] plexi_top_471_2x291_2_part  label="plexi-top-471.2x291.2-part"
  LinkPlacement = pos=(-30.4999,319.5,461.997) rot=(0,1.00097,0;0rad)
  LinkedObject = -> <external panels/plexi.FCStd>#Part004
  Placement = pos=(-30.4999,319.5,461.997) rot=(0,1.00097,0;0rad)
FEATURE [App::FeaturePython] Joint019  label="Fixed018"  # Assembly joint (typed FeaturePython)
  Activated = true
  AngleMax = 0
  AngleMin = 0
  Detach1 = false
  Detach2 = false
  Distance = 0
  Distance2 = 0
  EnableAngleMax = false
  EnableAngleMin = false
  EnableLengthMax = false
  EnableLengthMin = false
  JointType = 0 (Fixed)
  LengthMax = 0
  LengthMin = 0
  Offset1 = pos=(0.4,-0.4,0) rot=(0,0,1;0rad)
  Offset2 = pos=(0,0,-2) rot=(0,0,1;3.14159rad)
  Placement1 = pos=(146,-236,1.5) rot=(0,0,1;0rad)
  Placement2 = pos=(19,19,4.2) rot=(0,0,1;3.14159rad)
  Reference1 = -> Assembly [plexi_top_471_2x291_2_part.Body004.Edge2,plexi_top_471_2x291_2_part.Body004.Edge2]
  Reference2 = -> Assembly [middle_plexi_mount_part003.Body001.Edge31,middle_plexi_mount_part003.Body001.Vertex26]
FEATURE [App::Link] corner_plexi_mount_part008  label="corner-plexi-mount-part008"
  LinkPlacement = pos=(-195.5,574.5,467.7) rot=(1,0,0;3.14159rad)
  LinkedObject = -> <external panels/plexi-mount.FCStd>#Part
  Placement = pos=(-195.5,574.5,467.7) rot=(1,0,0;3.14159rad)
FEATURE [App::FeaturePython] Joint020  label="Fixed019"  # Assembly joint (typed FeaturePython)
  Activated = true
  AngleMax = 0
  AngleMin = 0
  Detach1 = false
  Detach2 = false
  Distance = 0
  Distance2 = 0
  EnableAngleMax = false
  EnableAngleMin = false
  EnableLengthMax = false
  EnableLengthMin = false
  JointType = 0 (Fixed)
  LengthMax = 0
  LengthMin = 0
  Offset1 = pos=(0,0,-31.2) rot=(0,0,1;0rad)
  Offset2 = pos=(0,0,0) rot=(0,0,-1;1.5708rad)
  Placement1 = pos=(0,6.3,6.2) rot=(0.57735,0.57735,0.57735;4.18879rad)
  Placement2 = pos=(15,8.7,500) rot=(0,0.707107,0.707107;3.14159rad)
  Reference1 = -> Assembly [corner_plexi_mount_part008.Body.Edge25,corner_plexi_mount_part008.Body.Edge25]
  Reference2 = -> Assembly [frame_assembly._0x30_550_002.Edge22,frame_assembly._0x30_550_002.Edge22]
FEATURE [App::Link] corner_plexi_mount_part009  label="corner-plexi-mount-part009"
  LinkPlacement = pos=(-195.5,64.4999,467.7) rot=(0.707107,0.707107,0;3.14159rad)
  LinkedObject = -> <external panels/plexi-mount.FCStd>#Part
  Placement = pos=(-195.5,64.4999,467.7) rot=(0.707107,0.707107,0;3.14159rad)
FEATURE [App::FeaturePython] Joint021  label="Fixed020"  # Assembly joint (typed FeaturePython)
  Activated = true
  AngleMax = 0
  AngleMin = 0
  Detach1 = false
  Detach2 = false
  Distance = 0
  Distance2 = 0
  EnableAngleMax = false
  EnableAngleMin = false
  EnableLengthMax = false
  EnableLengthMin = false
  JointType = 0 (Fixed)
  LengthMax = 0
  LengthMin = 0
  Offset2 = pos=(0,0,13.8) rot=(0,0,1;1.5708rad)
  Placement1 = pos=(37.5,0,6.2) rot=(-0.707107,0,0.707107;3.14159rad)
  Placement2 = pos=(15,22.5,500) rot=(1,0,0;4.71239rad)
  Reference1 = -> Assembly [corner_plexi_mount_part009.Body.Edge29,corner_plexi_mount_part009.Body.Edge29]
  Reference2 = -> Assembly [frame_assembly._0x30_550.Edge22,frame_assembly._0x30_550.Edge22]
FEATURE [App::Link] plexi_bottom_511_2x471_2_part  label="plexi-bottom-511.2x471.2-part"
  LinkPlacement = pos=(79.4998,319.5,-51.5) rot=(0,1.00097,0;0rad)
  LinkedObject = -> <external panels/plexi.FCStd>#Part001
  Placement = pos=(79.4998,319.5,-51.5) rot=(0,1.00097,0;0rad)
FEATURE [App::FeaturePython] Joint022  label="Fixed021"  # Assembly joint (typed FeaturePython)
  Activated = true
  AngleMax = 0
  AngleMin = 0
  Detach1 = false
  Detach2 = false
  Distance = 0
  Distance2 = 0
  EnableAngleMax = false
  EnableAngleMin = false
  EnableLengthMax = false
  EnableLengthMin = false
  JointType = 0 (Fixed)
  LengthMax = 0
  LengthMin = 0
  Offset2 = pos=(0,0,0) rot=(0,0,1;1.5708rad)
  Placement1 = pos=(255.6,-225,3) rot=(0.57735,0.57735,0.57735;4.18879rad)
  Placement2 = pos=(-4.4,-15,400) rot=(0.707107,0.707107,0;3.14159rad)
  Reference1 = -> Assembly [plexi_bottom_511_2x471_2_part.Body001.Edge25,plexi_bottom_511_2x471_2_part.Body001.Vertex16]
  Reference2 = -> Assembly [frame_assembly._0x30_551.Edge315,frame_assembly._0x30_551.Vertex81]
FEATURE [App::Link] corner_plexi_mount_part010  label="corner-plexi-mount-part010"
  LinkPlacement = pos=(-195.5,58.2999,461.5) rot=(-1,0,0;1.5708rad)
  LinkedObject = -> <external panels/plexi-mount.FCStd>#Part
  Placement = pos=(-195.5,58.2999,461.5) rot=(-1,0,0;1.5708rad)
FEATURE [App::FeaturePython] Joint024  label="Fixed023"  # Assembly joint (typed FeaturePython)
  Activated = true
  AngleMax = 0
  AngleMin = 0
  Detach1 = false
  Detach2 = false
  Distance = 0
  Distance2 = 0
  EnableAngleMax = false
  EnableAngleMin = false
  EnableLengthMax = false
  EnableLengthMin = false
  JointType = 0 (Fixed)
  LengthMax = 0
  LengthMin = 0
  Offset2 = pos=(0,0,37.5) rot=(0,0,-1;1.5708rad)
  Placement1 = pos=(37.5,0,6.2) rot=(-0.707107,0,0.707107;3.14159rad)
  Placement2 = pos=(0,37.5,6.2) rot=(0,0.707107,0.707107;3.14159rad)
  Reference1 = -> Assembly [corner_plexi_mount_part010.Body.Edge29,corner_plexi_mount_part010.Body.Edge29]
  Reference2 = -> Assembly [corner_plexi_mount_part009.Body.Edge25,corner_plexi_mount_part009.Body.Vertex21]
FEATURE [App::Link] corner_plexi_mount_part011  label="corner-plexi-mount-part011"
  LinkPlacement = pos=(-195.5,580.7,461.5) rot=(0.57735,0.57735,-0.57735;2.0944rad)
  LinkedObject = -> <external panels/plexi-mount.FCStd>#Part
  Placement = pos=(-195.5,580.7,461.5) rot=(0.57735,0.57735,-0.57735;2.0944rad)
FEATURE [App::FeaturePython] Joint026  label="Fixed025"  # Assembly joint (typed FeaturePython)
  Activated = true
  AngleMax = 0
  AngleMin = 0
  Detach1 = false
  Detach2 = false
  Distance = 0
  Distance2 = 0
  EnableAngleMax = false
  EnableAngleMin = false
  EnableLengthMax = false
  EnableLengthMin = false
  JointType = 0 (Fixed)
  LengthMax = 0
  LengthMin = 0
  Offset2 = pos=(0,0,-37.5) rot=(0,0,-1;1.5708rad)
  Placement1 = pos=(0,37.5,6.2) rot=(0.57735,0.57735,0.57735;4.18879rad)
  Placement2 = pos=(37.5,0,6.2) rot=(-0.57735,-0.57735,0.57735;2.0944rad)
  Reference1 = -> Assembly [corner_plexi_mount_part011.Body.Edge25,corner_plexi_mount_part011.Body.Edge25]
  Reference2 = -> Assembly [corner_plexi_mount_part008.Body.Edge29,corner_plexi_mount_part008.Body.Vertex21]
FEATURE [App::Link] plexi_top_471_2x211_2_part001  label="plexi-top-471.2x211.2-part001"
  LinkPlacement = pos=(229.5,61.4999,206.5) rot=(0,0.707107,0.707107;3.14159rad)
  LinkedObject = -> <external panels/plexi.FCStd>#Part003
  Placement = pos=(229.5,61.4999,206.5) rot=(0,0.707107,0.707107;3.14159rad)
FEATURE [App::FeaturePython] Joint027  label="Fixed026"  # Assembly joint (typed FeaturePython)
  Activated = true
  AngleMax = 0
  AngleMin = 0
  Detach1 = false
  Detach2 = false
  Distance = 0
  Distance2 = 0
  EnableAngleMax = false
  EnableAngleMin = false
  EnableLengthMax = false
  EnableLengthMin = false
  JointType = 0 (Fixed)
  LengthMax = 0
  LengthMin = 0
  Offset2 = pos=(0,0,19.4) rot=(0,0,-1;1.5708rad)
  Placement1 = pos=(-105.6,235.6,3) rot=(-0.707107,0,0.707107;3.14159rad)
  Placement2 = pos=(-4.4,-15,-30.6) rot=(0,0,-1;1.5708rad)
  Reference1 = -> Assembly [plexi_top_471_2x211_2_part001.Body003.Edge10,plexi_top_471_2x211_2_part001.Body003.Vertex8]
  Reference2 = -> Assembly [frame_assembly._0x30_550.Edge315,frame_assembly._0x30_550.Vertex148]
FEATURE [App::Link] corner_plexi_mount_part012  label="corner-plexi-mount-part012"
  LinkPlacement = pos=(-201.7,574.5,461.5) rot=(-0.57735,0.57735,-0.57735;2.0944rad)
  LinkedObject = -> <external panels/plexi-mount.FCStd>#Part
  Placement = pos=(-201.7,574.5,461.5) rot=(-0.57735,0.57735,-0.57735;2.0944rad)
FEATURE [App::Link] corner_plexi_mount_part013  label="corner-plexi-mount-part013"
  LinkPlacement = pos=(-201.7,64.4999,461.5) rot=(0,1,0;1.5708rad)
  LinkedObject = -> <external panels/plexi-mount.FCStd>#Part
  Placement = pos=(-201.7,64.4999,461.5) rot=(0,1,0;1.5708rad)
FEATURE [App::FeaturePython] Joint029  label="Fixed028"  # Assembly joint (typed FeaturePython)
  Activated = true
  AngleMax = 0
  AngleMin = 0
  Detach1 = false
  Detach2 = false
  Distance = 0
  Distance2 = 0
  EnableAngleMax = false
  EnableAngleMin = false
  EnableLengthMax = false
  EnableLengthMin = false
  JointType = 0 (Fixed)
  LengthMax = 0
  LengthMin = 0
  Offset2 = pos=(0,0,0) rot=(0,0,-1;1.5708rad)
  Placement1 = pos=(0,37.5,6.2) rot=(0.57735,0.57735,0.57735;4.18879rad)
  Placement2 = pos=(37.5,0,6.2) rot=(-0.57735,-0.57735,0.57735;2.0944rad)
  Reference1 = -> Assembly [corner_plexi_mount_part013.Body.Edge25,corner_plexi_mount_part013.Body.Edge25]
  Reference2 = -> Assembly [corner_plexi_mount_part009.Body.Edge29,corner_plexi_mount_part009.Body.Edge29]
FEATURE [App::FeaturePython] Joint030  label="Fixed029"  # Assembly joint (typed FeaturePython)
  Activated = true
  AngleMax = 0
  AngleMin = 0
  Detach1 = false
  Detach2 = false
  Distance = 0
  Distance2 = 0
  EnableAngleMax = false
  EnableAngleMin = false
  EnableLengthMax = false
  EnableLengthMin = false
  JointType = 0 (Fixed)
  LengthMax = 0
  LengthMin = 0
  Offset2 = pos=(0,0,37.5) rot=(0,0,-1;1.5708rad)
  Placement1 = pos=(37.5,0,6.2) rot=(-0.707107,0,0.707107;3.14159rad)
  Placement2 = pos=(0,37.5,6.2) rot=(0,0.707107,0.707107;3.14159rad)
  Reference1 = -> Assembly [corner_plexi_mount_part012.Body.Edge29,corner_plexi_mount_part012.Body.Edge29]
  Reference2 = -> Assembly [corner_plexi_mount_part008.Body.Edge25,corner_plexi_mount_part008.Body.Vertex21]
FEATURE [App::Link] plexi_top_471_2x291_2_part001  label="plexi-top-471.2x291.2-part001"
  LinkPlacement = pos=(-30.9,64.4999,206.9) rot=(1,0,0;1.5708rad)
  LinkedObject = -> <external panels/plexi.FCStd>#Part004
  Placement = pos=(-30.9,64.4999,206.9) rot=(1,0,0;1.5708rad)
FEATURE [App::Link] plexi_top_471_2x291_2_part002  label="plexi-top-471.2x291.2-part002"
  LinkPlacement = pos=(-30.6,574.6,206.4) rot=(-1,0,0;1.5708rad)
  LinkedObject = -> <external panels/plexi.FCStd>#Part004
  Placement = pos=(-30.6,574.6,206.4) rot=(-1,0,0;1.5708rad)
FEATURE [App::FeaturePython] Joint032  label="Fixed031"  # Assembly joint (typed FeaturePython)
  Activated = true
  AngleMax = 0
  AngleMin = 0
  Detach1 = false
  Detach2 = false
  Distance = 0
  Distance2 = 0
  EnableAngleMax = false
  EnableAngleMin = false
  EnableLengthMax = false
  EnableLengthMin = false
  JointType = 0 (Fixed)
  LengthMax = 0
  LengthMin = 0
  Offset1 = pos=(0.5,-0.5,0) rot=(0,0,1;0rad)
  Offset2 = pos=(0,0,0) rot=(0,0,1;3.14159rad)
  Placement1 = pos=(146.1,-236.1,1.5) rot=(0,0,1;0rad)
  Placement2 = pos=(19,19,4.6) rot=(0,0,1;3.14159rad)
  Reference1 = -> Assembly [plexi_top_471_2x291_2_part002.Body004.Edge2,plexi_top_471_2x291_2_part002.Body004.Edge2]
  Reference2 = -> Assembly [middle_plexi_mount_part001.Body001.Edge31,middle_plexi_mount_part001.Body001.Edge31]
  expr: .Offset1.Base.y = -0.5
FEATURE [App::FeaturePython] Joint033  label="Fixed032"  # Assembly joint (typed FeaturePython)
  Activated = true
  AngleMax = 0
  AngleMin = 0
  Detach1 = false
  Detach2 = false
  Distance = 0
  Distance2 = 0
  EnableAngleMax = false
  EnableAngleMin = false
  EnableLengthMax = false
  EnableLengthMin = false
  JointType = 0 (Fixed)
  LengthMax = 0
  LengthMin = 0
  Offset2 = pos=(0,0,-1.5) rot=(0,0,1;0rad)
  Placement1 = pos=(-145.6,235.6,1.5) rot=(0,0,1;0rad)
  Placement2 = pos=(19,19,4.7) rot=(0,0,1;0rad)
  Reference1 = -> Assembly [plexi_top_471_2x291_2_part001.Body004.Edge8,plexi_top_471_2x291_2_part001.Body004.Edge8]
  Reference2 = -> Assembly [corner_plexi_mount_part010.Body.Edge27,corner_plexi_mount_part010.Body.Vertex22]
FEATURE [App::Link] corner_plexi_mount_part014  label="corner-plexi-mount-part014"
  LinkPlacement = pos=(-195.5,58.2999,-48.4999) rot=(-0.57735,-0.57735,-0.57735;2.0944rad)
  LinkedObject = -> <external panels/plexi-mount.FCStd>#Part
  Placement = pos=(-195.5,58.2999,-48.4999) rot=(-0.57735,-0.57735,-0.57735;2.0944rad)
FEATURE [App::FeaturePython] Joint034  label="Fixed033"  # Assembly joint (typed FeaturePython)
  Activated = true
  AngleMax = 0
  AngleMin = 0
  Detach1 = false
  Detach2 = false
  Distance = 0
  Distance2 = 0
  EnableAngleMax = false
  EnableAngleMin = false
  EnableLengthMax = false
  EnableLengthMin = false
  JointType = 0 (Fixed)
  LengthMax = 0
  LengthMin = 0
  Offset2 = pos=(0,0,23.7) rot=(0,0,1;1.5708rad)
  Placement1 = pos=(0,0,6.2) rot=(-0.707107,0,0.707107;3.14159rad)
  Placement2 = pos=(15,-15,-50) rot=(0.57735,-0.57735,0.57735;4.18879rad)
  Reference1 = -> Assembly [corner_plexi_mount_part014.Body.Edge29,corner_plexi_mount_part014.Body.Vertex21]
  Reference2 = -> Assembly [frame_assembly._0x30_550_v6.Edge151,frame_assembly._0x30_550_v6.Edge151]
FEATURE [App::Link] corner_plexi_mount_part015  label="corner-plexi-mount-part015"
  LinkPlacement = pos=(-195.5,580.7,-51.4999) rot=(1,0,0;1.5708rad)
  LinkedObject = -> <external panels/plexi-mount.FCStd>#Part
  Placement = pos=(-195.5,580.7,-51.4999) rot=(1,0,0;1.5708rad)
FEATURE [App::FeaturePython] Joint035  label="Fixed034"  # Assembly joint (typed FeaturePython)
  Activated = true
  AngleMax = 0
  AngleMin = 0
  Detach1 = false
  Detach2 = false
  Distance = 0
  Distance2 = 0
  EnableAngleMax = false
  EnableAngleMin = false
  EnableLengthMax = false
  EnableLengthMin = false
  JointType = 0 (Fixed)
  LengthMax = 0
  LengthMin = 0
  Offset2 = pos=(0,0,28.2) rot=(0,0,1;1.5708rad)
  Placement1 = pos=(0,37.5,6.2) rot=(0.57735,0.57735,0.57735;4.18879rad)
  Placement2 = pos=(-19.5,15,-50) rot=(-0.57735,0.57735,0.57735;4.18879rad)
  Reference1 = -> Assembly [corner_plexi_mount_part015.Body.Edge25,corner_plexi_mount_part015.Body.Edge25]
  Reference2 = -> Assembly [frame_assembly._0x30_550_001.Edge195,frame_assembly._0x30_550_001.Edge195]
FEATURE [App::Link] plexi_back_471x471_part  label="plexi-back-471x471-part"
  LinkPlacement = pos=(-197.1,319.5,206.5) rot=(-0.57735,0.57735,0.57735;4.18879rad)
  LinkedObject = -> <external panels/plexi.FCStd>#Part005
  Placement = pos=(-197.1,319.5,206.5) rot=(-0.57735,0.57735,0.57735;4.18879rad)
FEATURE [App::FeaturePython] Joint036  label="Fixed035"  # Assembly joint (typed FeaturePython)
  Activated = true
  AngleMax = 0
  AngleMin = 0
  Detach1 = false
  Detach2 = false
  Distance = 0
  Distance2 = 0
  EnableAngleMax = false
  EnableAngleMin = false
  EnableLengthMax = false
  EnableLengthMin = false
  JointType = 0 (Fixed)
  LengthMax = 0
  LengthMin = 0
  Offset1 = pos=(-0.5,0.5,0) rot=(0,0,1;0rad)
  Placement1 = pos=(-236,236,0) rot=(0,0,1;0rad)
  Placement2 = pos=(19,19,4.6) rot=(0,0,1;0rad)
  Reference1 = -> Assembly [plexi_back_471x471_part.Body005.Edge43,plexi_back_471x471_part.Body005.Vertex11]
  Reference2 = -> Assembly [corner_plexi_mount_part012.Body.Edge27,corner_plexi_mount_part012.Body.Edge27]
FEATURE [App::Link] plexi_electronics_side_261x210_6_part  label="plexi-electronics-side-261x210.6-part"
  LinkPlacement = pos=(-300.8,61.4999,101.6) rot=(-0.57735,-0.57735,-0.57735;2.0944rad)
  LinkedObject = -> <external panels/plexi.FCStd>#Part006
  Placement = pos=(-300.8,61.4999,101.6) rot=(-0.57735,-0.57735,-0.57735;2.0944rad)
FEATURE [App::Link] plexi_electronics_side_261x210_6_part001  label="plexi-electronics-side-261x210.6-part001"
  LinkPlacement = pos=(-300.8,577.5,101.6) rot=(0.57735,-0.57735,0.57735;2.0944rad)
  LinkedObject = -> <external panels/plexi.FCStd>#Part006
  Placement = pos=(-300.8,577.5,101.6) rot=(0.57735,-0.57735,0.57735;2.0944rad)
FEATURE [App::Link] plexi_electronics_top_471x207_6_part  label="plexi-electronics-top-471x207.6-part"
  LinkPlacement = pos=(-302.3,319.6,251.5) rot=(0,0,1;4.71239rad)
  LinkedObject = -> <external panels/plexi.FCStd>#Part007
  Placement = pos=(-302.3,319.6,251.5) rot=(0,0,1;4.71239rad)
FEATURE [App::Link] plexi_electronics_bottom_471x210_6_part  label="plexi-electronics-bottom-471x210.6-part"
  LinkPlacement = pos=(-300.7,319.4,-48.4998) rot=(0.707107,0.707107,0;3.14159rad)
  LinkedObject = -> <external panels/plexi.FCStd>#Part008
  Placement = pos=(-300.7,319.4,-48.4998) rot=(0.707107,0.707107,0;3.14159rad)
FEATURE [App::Link] plexi_electronics_front_471x261_part  label="plexi-electronics-front-471x261-part"
  LinkPlacement = pos=(-428.5,319.6,101.6) rot=(0,-1,0;4.71239rad)
  LinkedObject = -> <external panels/plexi.FCStd>#Part009
  Placement = pos=(-428.5,319.6,101.6) rot=(0,-1,0;4.71239rad)
FEATURE [App::FeaturePython] Joint042  label="RackPinion"  # Assembly joint (typed FeaturePython)
  Activated = true
  AngleMax = 0
  AngleMin = 0
  Detach1 = false
  Detach2 = false
  Distance = 0
  Distance2 = 0
  EnableAngleMax = false
  EnableAngleMin = false
  EnableLengthMax = false
  EnableLengthMin = false
  JointType = 9 (RackPinion)
  LengthMax = 0
  LengthMin = 0
FEATURE [App::Link] alu_prof_3030_300_000  label="alu-prof-3030-300-001"
  LinkedObject = -> <external electronics/electronics-box.FCStd>#alu_prof_3030_300_000
FEATURE [App::Link] alu_prof_3030_450_000  label="alu-prof-3030-450-001"
  LinkPlacement = pos=(415,-2.4e-15,235) rot=(0,-1,0;1.5708rad)
  LinkedObject = -> <external electronics/electronics-box.FCStd>#alu_prof_3030_450_000
  Placement = pos=(415,-2.4e-15,235) rot=(0,-1,0;1.5708rad)
FEATURE [App::Link] alu_prof_3030_300_001  label="alu-prof-3030-300-002"
  LinkPlacement = pos=(480,-1.166e-13,740) rot=(0,1,0;3.14159rad)
  LinkedObject = -> <external electronics/electronics-box.FCStd>#alu_prof_3030_300_001
  Placement = pos=(480,-1.166e-13,740) rot=(0,1,0;3.14159rad)
FEATURE [App::Link] alu_prof_3030_200_000  label="alu-prof-3030-200-001"
  LinkPlacement = pos=(480,-235,505) rot=(1,0,0;4.71239rad)
  LinkedObject = -> <external electronics/electronics-box.FCStd>#alu_prof_3030_200_000
  Placement = pos=(480,-235,505) rot=(1,0,0;4.71239rad)
FEATURE [App::Link] alu_prof_3030_200_001  label="alu-prof-3030-200-002"
  LinkPlacement = pos=(9.88e-14,-235,505) rot=(-1,0,0;1.5708rad)
  LinkedObject = -> <external electronics/electronics-box.FCStd>#alu_prof_3030_200_001
  Placement = pos=(9.88e-14,-235,505) rot=(-1,0,0;1.5708rad)
FEATURE [App::Link] alu_prof_3030_200_002  label="alu-prof-3030-200-003"
  LinkPlacement = pos=(-9.59e-14,-235,235) rot=(1,0,0;4.71239rad)
  LinkedObject = -> <external electronics/electronics-box.FCStd>#alu_prof_3030_200_002
  Placement = pos=(-9.59e-14,-235,235) rot=(1,0,0;4.71239rad)
FEATURE [App::Link] alu_prof_3030_200_003  label="alu-prof-3030-200-004"
  LinkPlacement = pos=(480,-235,235) rot=(-1,0,0;1.5708rad)
  LinkedObject = -> <external electronics/electronics-box.FCStd>#alu_prof_3030_200_003
  Placement = pos=(480,-235,235) rot=(-1,0,0;1.5708rad)
FEATURE [App::Link] alu_prof_3030_450_003  label="alu-prof-3030-450-004"
  LinkPlacement = pos=(415,-2e-15,505) rot=(0,1,0;4.71239rad)
  LinkedObject = -> <external electronics/electronics-box.FCStd>#alu_prof_3030_450_003
  Placement = pos=(415,-2e-15,505) rot=(0,1,0;4.71239rad)
FEATURE [App::Link] _030_angle_bracket_000  label="3030-angle-bracket-001"
  LinkPlacement = pos=(0.3,-197.5,250) rot=(-0.57735,-0.57735,-0.57735;4.18879rad)
  LinkedObject = -> <external electronics/electronics-box.FCStd>#_030_angle_bracket_000
  Placement = pos=(0.3,-197.5,250) rot=(-0.57735,-0.57735,-0.57735;4.18879rad)
FEATURE [App::Link] _030_angle_bracket_001  label="3030-angle-bracket-002"
  LinkPlacement = pos=(32.5,-15,505) rot=(1,0,0;3.14159rad)
  LinkedObject = -> <external electronics/electronics-box.FCStd>#_030_angle_bracket_001
  Placement = pos=(32.5,-15,505) rot=(1,0,0;3.14159rad)
FEATURE [App::Link] _030_angle_bracket_002  label="3030-angle-bracket-003"
  LinkPlacement = pos=(0.1,-15,267.5) rot=(0.707107,0,0.707107;3.14159rad)
  LinkedObject = -> <external electronics/electronics-box.FCStd>#_030_angle_bracket_002
  Placement = pos=(0.1,-15,267.5) rot=(0.707107,0,0.707107;3.14159rad)
FEATURE [App::Link] _030_angle_bracket_003  label="3030-angle-bracket-004"
  LinkPlacement = pos=(15,0.1,472.5) rot=(0.57735,0.57735,-0.57735;2.0944rad)
  LinkedObject = -> <external electronics/electronics-box.FCStd>#_030_angle_bracket_003
  Placement = pos=(15,0.1,472.5) rot=(0.57735,0.57735,-0.57735;2.0944rad)
FEATURE [App::Link] _030_angle_bracket_004  label="3030-angle-bracket-005"
  LinkPlacement = pos=(0.3,-215,472.5) rot=(0,-1,0;4.71239rad)
  LinkedObject = -> <external electronics/electronics-box.FCStd>#_030_angle_bracket_004
  Placement = pos=(0.3,-215,472.5) rot=(0,-1,0;4.71239rad)
FEATURE [App::Link] _030_angle_bracket_005  label="3030-angle-bracket-006"
  LinkPlacement = pos=(-0.3,-32.5,490) rot=(0.57735,-0.57735,0.57735;4.18879rad)
  LinkedObject = -> <external electronics/electronics-box.FCStd>#_030_angle_bracket_005
  Placement = pos=(-0.3,-32.5,490) rot=(0.57735,-0.57735,0.57735;4.18879rad)
FEATURE [App::Link] _030_angle_bracket_006  label="3030-angle-bracket-007"
  LinkPlacement = pos=(447.5,-0.3,250) rot=(0,0.707107,0.707107;3.14159rad)
  LinkedObject = -> <external electronics/electronics-box.FCStd>#_030_angle_bracket_006
  Placement = pos=(447.5,-0.3,250) rot=(0,0.707107,0.707107;3.14159rad)
FEATURE [App::Link] _030_angle_bracket_007  label="3030-angle-bracket-008"
  LinkPlacement = pos=(465,-1.3,472.5) rot=(-0.57735,0.57735,0.57735;2.0944rad)
  LinkedObject = -> <external electronics/electronics-box.FCStd>#_030_angle_bracket_007
  Placement = pos=(465,-1.3,472.5) rot=(-0.57735,0.57735,0.57735;2.0944rad)
FEATURE [App::Link] _030_angle_bracket_008  label="3030-angle-bracket-009"
  LinkPlacement = pos=(32.5,-15,234.7) rot=(-1,0,0;3.14159rad)
  LinkedObject = -> <external electronics/electronics-box.FCStd>#_030_angle_bracket_008
  Placement = pos=(32.5,-15,234.7) rot=(-1,0,0;3.14159rad)
FEATURE [App::Link] _030_angle_bracket_009  label="3030-angle-bracket-010"
  LinkPlacement = pos=(15,0.3,267.5) rot=(0.57735,0.57735,0.57735;4.18879rad)
  LinkedObject = -> <external electronics/electronics-box.FCStd>#_030_angle_bracket_009
  Placement = pos=(15,0.3,267.5) rot=(0.57735,0.57735,0.57735;4.18879rad)
FEATURE [App::Link] _030_angle_bracket_010  label="3030-angle-bracket-011"
  LinkPlacement = pos=(447.5,-15,235.3) rot=(0,0,1;3.14159rad)
  LinkedObject = -> <external electronics/electronics-box.FCStd>#_030_angle_bracket_010
  Placement = pos=(447.5,-15,235.3) rot=(0,0,1;3.14159rad)
FEATURE [App::Link] _030_angle_bracket_011  label="3030-angle-bracket-012"
  LinkPlacement = pos=(480.3,-15,267.5) rot=(0.707107,0,0.707107;3.14159rad)
  LinkedObject = -> <external electronics/electronics-box.FCStd>#_030_angle_bracket_011
  Placement = pos=(480.3,-15,267.5) rot=(0.707107,0,0.707107;3.14159rad)
FEATURE [App::Link] _030_angle_bracket_012  label="3030-angle-bracket-013"
  LinkPlacement = pos=(480.3,-197.5,250) rot=(0.57735,0.57735,0.57735;2.0944rad)
  LinkedObject = -> <external electronics/electronics-box.FCStd>#_030_angle_bracket_012
  Placement = pos=(480.3,-197.5,250) rot=(0.57735,0.57735,0.57735;2.0944rad)
FEATURE [App::Link] _030_angle_bracket_013  label="3030-angle-bracket-014"
  LinkPlacement = pos=(479.7,-215,472.5) rot=(0,1,0;1.5708rad)
  LinkedObject = -> <external electronics/electronics-box.FCStd>#_030_angle_bracket_013
  Placement = pos=(479.7,-215,472.5) rot=(0,1,0;1.5708rad)
FEATURE [App::Link] _030_angle_bracket_014  label="3030-angle-bracket-015"
  LinkPlacement = pos=(480.3,-32.5,490) rot=(-0.57735,0.57735,-0.57735;2.0944rad)
  LinkedObject = -> <external electronics/electronics-box.FCStd>#_030_angle_bracket_014
  Placement = pos=(480.3,-32.5,490) rot=(-0.57735,0.57735,-0.57735;2.0944rad)
FEATURE [App::Link] _030_angle_bracket_015  label="3030-angle-bracket-016"
  LinkPlacement = pos=(447.5,-15,504.7) rot=(0,0,-1;3.14159rad)
  LinkedObject = -> <external electronics/electronics-box.FCStd>#_030_angle_bracket_015
  Placement = pos=(447.5,-15,504.7) rot=(0,0,-1;3.14159rad)
FEATURE [App::FeaturePython] Joint043  label="Fixed036"  # Assembly joint (typed FeaturePython)
  Activated = true
  AngleMax = 0
  AngleMin = 0
  Detach1 = false
  Detach2 = false
  Distance = 0
  Distance2 = 0
  EnableAngleMax = false
  EnableAngleMin = false
  EnableLengthMax = false
  EnableLengthMin = false
  JointType = 0 (Fixed)
  LengthMax = 0
  LengthMin = 0
  Placement1 = pos=(8.7,15,20) rot=(-0.707107,0,0.707107;3.14159rad)
  Placement2 = pos=(15,8.7,-50) rot=(0.57735,0.57735,0.57735;4.18879rad)
  Reference1 = -> Assembly [electronics_box_assembly.alu_prof_3030_200_003.Edge71,electronics_box_assembly.alu_prof_3030_200_003.Edge71]
  Reference2 = -> Assembly [frame_assembly._0x30_550_001.Edge197,frame_assembly._0x30_550_001.Edge197]
FEATURE [Assembly::JointGroup] Joints
  Group = -> [GroundedJoint,Joint,Joint005,Joint006,Joint007,Joint008,Joint009,Joint010,Joint011,Joint012,Joint013,Joint014,Joint015,Joint016,Joint017,Joint018,Joint019,Joint020,Joint021,Joint022,Joint024,Joint026,Joint027,Joint029,Joint030,Joint032,Joint033,Joint034,Joint035,Joint036,Joint042,Joint043]
FEATURE [App::Link] din_mount_part
  LinkPlacement = pos=(480,-79,490) rot=(0.707107,-0.707107,0;3.14159rad)
  LinkedObject = -> <external electronics/electronics-box.FCStd>#din_mount_part
  Placement = pos=(480,-79,490) rot=(0.707107,-0.707107,0;3.14159rad)
FEATURE [App::Link] din_mount_part001
  LinkPlacement = pos=(480,-140,490) rot=(0.707107,-0.707107,0;3.14159rad)
  LinkedObject = -> <external electronics/electronics-box.FCStd>#din_mount_part001
  Placement = pos=(480,-140,490) rot=(0.707107,-0.707107,0;3.14159rad)
FEATURE [App::Link] din_rail_180mm  label="din_rail_180mm001"
  LinkPlacement = pos=(465,3,437.5) rot=(0,0,-1;4.71239rad)
  LinkedObject = -> <external electronics/electronics-box.FCStd>#din_rail_180mm
  Placement = pos=(465,3,437.5) rot=(0,0,-1;4.71239rad)
FEATURE [App::Link] alu_prof_3030_450_004  label="alu-prof-3030-450-005"
  LinkPlacement = pos=(65,-5.3e-15,415) rot=(0,-1,0;4.71239rad)
  LinkedObject = -> <external electronics/electronics-box.FCStd>#alu_prof_3030_450_004
  Placement = pos=(65,-5.3e-15,415) rot=(0,-1,0;4.71239rad)
FEATURE [App::Link] _030_angle_bracket_016  label="3030-angle-bracket-017"
  LinkPlacement = pos=(32.5,-0.2,400) rot=(-1,0,0;1.5708rad)
  LinkedObject = -> <external electronics/electronics-box.FCStd>#_030_angle_bracket_016
  Placement = pos=(32.5,-0.2,400) rot=(-1,0,0;1.5708rad)
FEATURE [App::Link] _030_angle_bracket_017  label="3030-angle-bracket-018"
  LinkPlacement = pos=(447.5,-0.3,400) rot=(0,0.707107,-0.707107;3.14159rad)
  LinkedObject = -> <external electronics/electronics-box.FCStd>#_030_angle_bracket_017
  Placement = pos=(447.5,-0.3,400) rot=(0,0.707107,-0.707107;3.14159rad)
FEATURE [App::Link] power_supply_bracket_part  label="power-supply-bracket-part"
  LinkPlacement = pos=(283,15,400) rot=(0.57735,-0.57735,-0.57735;2.0944rad)
  LinkedObject = -> <external electronics/electronics-box.FCStd>#power_supply_bracket_part
  Placement = pos=(283,15,400) rot=(0.57735,-0.57735,-0.57735;2.0944rad)
FEATURE [App::Link] power_supply_bracket_part001  label="power-supply-bracket-part001"
  LinkPlacement = pos=(347,15,400) rot=(0.57735,-0.57735,-0.57735;2.0944rad)
  LinkedObject = -> <external electronics/electronics-box.FCStd>#power_supply_bracket_part001
  Placement = pos=(347,15,400) rot=(0.57735,-0.57735,-0.57735;2.0944rad)
FEATURE [App::Link] LRS_154  label="LRS-155"
  LinkPlacement = pos=(283,-104.5,414.75) rot=(-0.57735,-0.57735,0.57735;4.18879rad)
  LinkedObject = -> <external electronics/electronics-box.FCStd>#LRS_154
  Placement = pos=(283,-104.5,414.75) rot=(-0.57735,-0.57735,0.57735;4.18879rad)
FEATURE [App::Link] LRS_155  label="LRS-156"
  LinkPlacement = pos=(347,-103.25,414.75) rot=(-0.57735,-0.57735,0.57735;4.18879rad)
  LinkedObject = -> <external electronics/electronics-box.FCStd>#LRS_155
  Placement = pos=(347,-103.25,414.75) rot=(-0.57735,-0.57735,0.57735;4.18879rad)
FEATURE [App::Link] dlp_power_supply_bracket_part  label="dlp-power-supply-bracket-part"
  LinkPlacement = pos=(226,-36.5,425) rot=(0,0,1;0rad)
  LinkedObject = -> <external electronics/electronics-box.FCStd>#dlp_power_supply_bracket_part
  Placement = pos=(226,-36.5,425) rot=(0,0,1;0rad)
FEATURE [App::Link] smc100c_bracket_part  label="smc100c-bracket-part"
  LinkPlacement = pos=(171,-194,435) rot=(0,0,-1;4.71239rad)
  LinkedObject = -> <external electronics/electronics-box.FCStd>#smc100c_bracket_part
  Placement = pos=(171,-194,435) rot=(0,0,-1;4.71239rad)
FEATURE [App::Link] smc100c_bracket_part001  label="smc100c-bracket-part001"
  LinkPlacement = pos=(116,-194,435) rot=(0,0,-1;4.71239rad)
  LinkedObject = -> <external electronics/electronics-box.FCStd>#smc100c_bracket_part001
  Placement = pos=(116,-194,435) rot=(0,0,-1;4.71239rad)
FEATURE [App::Link] SMC100CC  label="SMC100CC001"
  LinkPlacement = pos=(92.7646,-343.5,357.708) rot=(-0.57735,0.57735,0.57735;2.0944rad)
  LinkedObject = -> <external electronics/electronics-box.FCStd>#SMC100CC
  Placement = pos=(92.7646,-343.5,357.708) rot=(-0.57735,0.57735,0.57735;2.0944rad)
FEATURE [App::Link] SMC100CC001  label="SMC100CC002"
  LinkPlacement = pos=(147.765,-343.5,357.708) rot=(-0.57735,0.57735,0.57735;2.0944rad)
  LinkedObject = -> <external electronics/electronics-box.FCStd>#SMC100CC001
  Placement = pos=(147.765,-343.5,357.708) rot=(-0.57735,0.57735,0.57735;2.0944rad)
FEATURE [App::Link] ports_panel_part  label="ports-panel-part"
  LinkPlacement = pos=(501.2,-100,257.5) rot=(0.57735,-0.57735,-0.57735;2.0944rad)
  LinkedObject = -> <external electronics/electronics-box.FCStd>#ports_panel_part
  Placement = pos=(501.2,-100,257.5) rot=(0.57735,-0.57735,-0.57735;2.0944rad)
FEATURE [Assembly::AssemblyLink] electronics_box_assembly  label="electronics-box-assembly"
  Group = -> [alu_prof_3030_300_000,alu_prof_3030_450_000,alu_prof_3030_300_001,alu_prof_3030_200_000,alu_prof_3030_200_001,alu_prof_3030_200_002,alu_prof_3030_200_003,alu_prof_3030_450_003,_030_angle_bracket_000,_030_angle_bracket_001,_030_angle_bracket_002,_030_angle_bracket_003,_030_angle_bracket_004,_030_angle_bracket_005,_030_angle_bracket_006,_030_angle_bracket_007,_030_angle_bracket_008,+23 more]
  LinkedObject = -> <external electronics/electronics-box.FCStd>#Assembly
  Origin = -> Origin002
  Placement = pos=(-410.5,79.4999,-268.5) rot=(0,0,1;1.5708rad)
  Rigid = true
FEATURE [Assembly::AssemblyObject] Assembly  label="lithography-assembly"
  Group = -> [Joints,frame_assembly,GroundedJoint,plexi_472x212_body001,plexi_471_2x471_2_body,middle_plexi_mount_part,corner_plexi_mount_part,Joint,Joint005,corner_plexi_mount_part001,Joint006,Joint007,middle_plexi_mount_part001,Joint008,corner_plexi_mount_part002,Joint009,Joint010,corner_plexi_mount_part003,Joint011,corner_plexi_mount_part004,corner_plexi_mount_part005,Joint012,Joint013,+46 more]
  Origin = -> Origin
  Type = Assembly

RESOLVED EXTERNAL PARTS (link-assembly join: the EXTERNAL_REF files above that resolve inside this repo's crawl, each included once):
---- part electronics/electronics-box.FCStd = doc fcstd_18db4ff1930a ----
FCSTD DOCUMENT  (FreeCAD 1.0R39319 (Git))
Label: electronics-box
License: All rights reserved
objects: App::Link×40, App::FeaturePython×40, Part::Feature×11, App::Part×1, Assembly::JointGroup×1, Assembly::AssemblyObject×1
note: 11 computed .brp shape members not serialized (recipe doc carries the construction recipe); baked Part::Feature solids carry a one-line shape summary decoded from their .brp
EXTERNAL_REF file=din_mount.FCStd obj=Part
EXTERNAL_REF file=power-supply-bracket.FCStd obj=Part
EXTERNAL_REF file=dlp-power-supply-bracket.FCStd obj=Part
EXTERNAL_REF file=smc100c-bracket.FCStd obj=Part
EXTERNAL_REF file=ports-panel.FCStd obj=Part

FEATURE [Part::Feature] Part__Feature  label="alu-prof-3030-200-000"
  shape: bbox 30 x 30 x 200 mm, 122 faces (baked)
FEATURE [Part::Feature] Part__Feature001  label="alu-prof-3030-300-000"
  shape: bbox 30 x 30 x 300 mm, 122 faces (baked)
FEATURE [Part::Feature] Part__Feature002  label="alu-prof-3030-450-000"
  shape: bbox 30 x 30 x 450 mm, 122 faces (baked)
FEATURE [App::Link] alu_prof_3030_300_000  label="alu-prof-3030-300-001"
  LinkedObject = -> Part__Feature001
FEATURE [App::Link] alu_prof_3030_450_000  label="alu-prof-3030-450-001"
  LinkPlacement = pos=(415,-2.4e-15,235) rot=(0,-1,0;1.5708rad)
  LinkedObject = -> Part__Feature002
  Placement = pos=(415,-2.4e-15,235) rot=(0,-1,0;1.5708rad)
FEATURE [App::FeaturePython] GroundedJoint  # Assembly grounded joint (typed FeaturePython)
  ObjectToGround = -> alu_prof_3030_300_000
FEATURE [App::FeaturePython] Joint  label="Fixed"  # Assembly joint (typed FeaturePython)
  Activated = true
  AngleMax = 0
  AngleMin = 0
  Detach1 = false
  Detach2 = false
  Distance = 0
  Distance2 = 0
  EnableAngleMax = false
  EnableAngleMin = false
  EnableLengthMax = false
  EnableLengthMin = false
  JointType = 0 (Fixed)
  LengthMax = 0
  LengthMin = 0
  Offset2 = pos=(0,0,0) rot=(0,0,-1;1.5708rad)
  Placement1 = pos=(-15,-8.7,400) rot=(0.57735,0.57735,0.57735;4.18879rad)
  Placement2 = pos=(15,-8.7,220) rot=(0,0.707107,0.707107;3.14159rad)
  Reference1 = -> Assembly [alu_prof_3030_450_000.Edge78,alu_prof_3030_450_000.Edge78]
  Reference2 = -> Assembly [alu_prof_3030_300_000.Edge7,alu_prof_3030_300_000.Edge7]
FEATURE [App::Link] alu_prof_3030_300_001  label="alu-prof-3030-300-002"
  LinkPlacement = pos=(480,-1.166e-13,740) rot=(0,1,0;3.14159rad)
  LinkedObject = -> Part__Feature001
  Placement = pos=(480,-1.166e-13,740) rot=(0,1,0;3.14159rad)
FEATURE [App::Link] alu_prof_3030_200_000  label="alu-prof-3030-200-001"
  LinkPlacement = pos=(480,-235,505) rot=(1,0,0;4.71239rad)
  LinkedObject = -> Part__Feature
  Placement = pos=(480,-235,505) rot=(1,0,0;4.71239rad)
FEATURE [App::Link] alu_prof_3030_200_001  label="alu-prof-3030-200-002"
  LinkPlacement = pos=(9.88e-14,-235,505) rot=(-1,0,0;1.5708rad)
  LinkedObject = -> Part__Feature
  Placement = pos=(9.88e-14,-235,505) rot=(-1,0,0;1.5708rad)
FEATURE [App::Link] alu_prof_3030_200_002  label="alu-prof-3030-200-003"
  LinkPlacement = pos=(-9.59e-14,-235,235) rot=(1,0,0;4.71239rad)
  LinkedObject = -> Part__Feature
  Placement = pos=(-9.59e-14,-235,235) rot=(1,0,0;4.71239rad)
FEATURE [App::Link] alu_prof_3030_200_003  label="alu-prof-3030-200-004"
  LinkPlacement = pos=(480,-235,235) rot=(-1,0,0;1.5708rad)
  LinkedObject = -> Part__Feature
  Placement = pos=(480,-235,235) rot=(-1,0,0;1.5708rad)
FEATURE [App::FeaturePython] Joint001  label="Fixed001"  # Assembly joint (typed FeaturePython)
  Activated = true
  AngleMax = 0
  AngleMin = 0
  Detach1 = false
  Detach2 = false
  Distance = 0
  Distance2 = 0
  EnableAngleMax = false
  EnableAngleMin = false
  EnableLengthMax = false
  EnableLengthMin = false
  JointType = 0 (Fixed)
  LengthMax = 0
  LengthMin = 0
  Offset2 = pos=(0,0,0) rot=(0,0,-1;1.5708rad)
  Placement1 = pos=(15,-8.7,520) rot=(0.57735,0.57735,0.57735;4.18879rad)
  Placement2 = pos=(-15,-8.7,-50) rot=(0,-0.707107,0.707107;3.14159rad)
  Reference1 = -> Assembly [alu_prof_3030_300_001.Edge5,alu_prof_3030_300_001.Edge5]
  Reference2 = -> Assembly [alu_prof_3030_450_000.Edge153,alu_prof_3030_450_000.Edge153]
FEATURE [App::FeaturePython] Joint002  label="Fixed002"  # Assembly joint (typed FeaturePython)
  Activated = true
  AngleMax = 0
  AngleMin = 0
  Detach1 = false
  Detach2 = false
  Distance = 0
  Distance2 = 0
  EnableAngleMax = false
  EnableAngleMin = false
  EnableLengthMax = false
  EnableLengthMin = false
  JointType = 0 (Fixed)
  LengthMax = 0
  LengthMin = 0
  Offset2 = pos=(0,0,0) rot=(0,0,1;1.5708rad)
  Placement1 = pos=(-8.7,15,220) rot=(-0.707107,0,0.707107;3.14159rad)
  Placement2 = pos=(-8.7,-15,220) rot=(0.57735,-0.57735,0.57735;4.18879rad)
  Reference1 = -> Assembly [alu_prof_3030_200_002.Edge133,alu_prof_3030_200_002.Edge133]
  Reference2 = -> Assembly [alu_prof_3030_300_000.Edge205,alu_prof_3030_300_000.Edge205]
FEATURE [App::FeaturePython] Joint003  label="Fixed003"  # Assembly joint (typed FeaturePython)
  Activated = true
  AngleMax = 0
  AngleMin = 0
  Detach1 = false
  Detach2 = false
  Distance = 0
  Distance2 = 0
  EnableAngleMax = false
  EnableAngleMin = false
  EnableLengthMax = false
  EnableLengthMin = false
  JointType = 0 (Fixed)
  LengthMax = 0
  LengthMin = 0
  Offset2 = pos=(0,0,0) rot=(0,0,1;1.5708rad)
  Placement1 = pos=(-8.7,15,220) rot=(-0.707107,0,0.707107;3.14159rad)
  Placement2 = pos=(8.7,-15,520) rot=(0.57735,-0.57735,0.57735;4.18879rad)
  Reference1 = -> Assembly [alu_prof_3030_200_003.Edge133,alu_prof_3030_200_003.Edge133]
  Reference2 = -> Assembly [alu_prof_3030_300_001.Edge263,alu_prof_3030_300_001.Edge263]
FEATURE [App::FeaturePython] Joint004  label="Fixed004"  # Assembly joint (typed FeaturePython)
  Activated = true
  AngleMax = 0
  AngleMin = 0
  Detach1 = false
  Detach2 = false
  Distance = 0
  Distance2 = 0
  EnableAngleMax = false
  EnableAngleMin = false
  EnableLengthMax = false
  EnableLengthMin = false
  JointType = 0 (Fixed)
  LengthMax = 0
  LengthMin = 0
  Offset2 = pos=(0,0,0) rot=(0,0,-1;1.5708rad)
  Placement1 = pos=(-8.7,-15,220) rot=(0.707107,0,0.707107;3.14159rad)
  Placement2 = pos=(-8.7,-15,520) rot=(0.57735,0.57735,0.57735;2.0944rad)
  Reference1 = -> Assembly [alu_prof_3030_200_001.Edge205,alu_prof_3030_200_001.Edge205]
  Reference2 = -> Assembly [alu_prof_3030_300_000.Edge203,alu_prof_3030_300_000.Edge203]
FEATURE [App::FeaturePython] Joint005  label="Fixed005"  # Assembly joint (typed FeaturePython)
  Activated = true
  AngleMax = 0
  AngleMin = 0
  Detach1 = false
  Detach2 = false
  Distance = 0
  Distance2 = 0
  EnableAngleMax = false
  EnableAngleMin = false
  EnableLengthMax = false
  EnableLengthMin = false
  JointType = 0 (Fixed)
  LengthMax = 0
  LengthMin = 0
  Offset2 = pos=(0,0,0) rot=(0,0,-1;1.5708rad)
  Placement1 = pos=(-8.7,-15,220) rot=(0.707107,0,0.707107;3.14159rad)
  Placement2 = pos=(8.7,-15,220) rot=(0.57735,0.57735,0.57735;2.0944rad)
  Reference1 = -> Assembly [alu_prof_3030_200_000.Edge205,alu_prof_3030_200_000.Edge205]
  Reference2 = -> Assembly [alu_prof_3030_300_001.Edge264,alu_prof_3030_300_001.Edge264]
FEATURE [App::Link] alu_prof_3030_450_003  label="alu-prof-3030-450-004"
  LinkPlacement = pos=(415,-2e-15,505) rot=(0,1,0;4.71239rad)
  LinkedObject = -> Part__Feature002
  Placement = pos=(415,-2e-15,505) rot=(0,1,0;4.71239rad)
FEATURE [App::FeaturePython] Joint010  label="Fixed010"  # Assembly joint (typed FeaturePython)
  Activated = true
  AngleMax = 0
  AngleMin = 0
  Detach1 = false
  Detach2 = false
  Distance = 0
  Distance2 = 0
  EnableAngleMax = false
  EnableAngleMin = false
  EnableLengthMax = false
  EnableLengthMin = false
  JointType = 0 (Fixed)
  LengthMax = 0
  LengthMin = 0
  Offset2 = pos=(0,0,0) rot=(0,0,1;1.5708rad)
  Placement1 = pos=(15,-8.7,400) rot=(-0.57735,-0.57735,0.57735;4.18879rad)
  Placement2 = pos=(15,-8.7,520) rot=(1,0,0;4.71239rad)
  Reference1 = -> Assembly [alu_prof_3030_450_003.Edge14,alu_prof_3030_450_003.Edge14]
  Reference2 = -> Assembly [alu_prof_3030_300_000.Edge5,alu_prof_3030_300_000.Edge5]
FEATURE [Part::Feature] Part__Feature003  label="3030-angle-bracket-000"
  shape: bbox 36.72 x 36.72 x 28 mm, 72 faces (baked)
FEATURE [Part::Feature] Part__Feature004  label="SMC100CC"
  shape: bbox 150.5 x 35.5 x 163 mm, 2390 faces (baked)
FEATURE [Part::Feature] Part__Feature005  label="alu-prof-3030-240-000"
  Placement = pos=(0,177,0) rot=(0,0,1;0rad)
  shape: bbox 30 x 30 x 240 mm, 122 faces (baked)
FEATURE [App::Link] _030_angle_bracket_000  label="3030-angle-bracket-001"
  LinkPlacement = pos=(0.3,-197.5,250) rot=(-0.57735,-0.57735,-0.57735;4.18879rad)
  LinkedObject = -> Part__Feature003
  Placement = pos=(0.3,-197.5,250) rot=(-0.57735,-0.57735,-0.57735;4.18879rad)
FEATURE [App::Link] _030_angle_bracket_001  label="3030-angle-bracket-002"
  LinkPlacement = pos=(32.5,-15,505) rot=(1,0,0;3.14159rad)
  LinkedObject = -> Part__Feature003
  Placement = pos=(32.5,-15,505) rot=(1,0,0;3.14159rad)
FEATURE [App::Link] _030_angle_bracket_002  label="3030-angle-bracket-003"
  LinkPlacement = pos=(0.1,-15,267.5) rot=(0.707107,0,0.707107;3.14159rad)
  LinkedObject = -> Part__Feature003
  Placement = pos=(0.1,-15,267.5) rot=(0.707107,0,0.707107;3.14159rad)
FEATURE [App::Link] _030_angle_bracket_003  label="3030-angle-bracket-004"
  LinkPlacement = pos=(15,0.1,472.5) rot=(0.57735,0.57735,-0.57735;2.0944rad)
  LinkedObject = -> Part__Feature003
  Placement = pos=(15,0.1,472.5) rot=(0.57735,0.57735,-0.57735;2.0944rad)
FEATURE [App::Link] _030_angle_bracket_004  label="3030-angle-bracket-005"
  LinkPlacement = pos=(0.3,-215,472.5) rot=(0,-1,0;4.71239rad)
  LinkedObject = -> Part__Feature003
  Placement = pos=(0.3,-215,472.5) rot=(0,-1,0;4.71239rad)
FEATURE [App::Link] _030_angle_bracket_005  label="3030-angle-bracket-006"
  LinkPlacement = pos=(-0.3,-32.5,490) rot=(0.57735,-0.57735,0.57735;4.18879rad)
  LinkedObject = -> Part__Feature003
  Placement = pos=(-0.3,-32.5,490) rot=(0.57735,-0.57735,0.57735;4.18879rad)
FEATURE [App::FeaturePython] Joint013  label="Fixed013"  # Assembly joint (typed FeaturePython)
  Activated = true
  AngleMax = 0
  AngleMin = 0
  Detach1 = false
  Detach2 = false
  Distance = 0
  Distance2 = 0
  EnableAngleMax = false
  EnableAngleMin = false
  EnableLengthMax = false
  EnableLengthMin = false
  JointType = 0 (Fixed)
  LengthMax = 0
  LengthMin = 0
  Offset2 = pos=(0,0,13) rot=(0,0,1;1.5708rad)
  Placement1 = pos=(-17.5,0,0) rot=(0,0,1;0rad)
  Placement2 = pos=(15,0,220) rot=(1,0,0;4.71239rad)
  Reference1 = -> Assembly [_030_angle_bracket_001.Edge3,_030_angle_bracket_001.Edge3]
  Reference2 = -> Assembly [alu_prof_3030_200_001.Edge7,alu_prof_3030_200_001.Vertex4]
FEATURE [App::FeaturePython] Joint014  label="Fixed014"  # Assembly joint (typed FeaturePython)
  Activated = true
  AngleMax = 0
  AngleMin = 0
  Detach1 = false
  Detach2 = false
  Distance = 0
  Distance2 = 0
  EnableAngleMax = false
  EnableAngleMin = false
  EnableLengthMax = false
  EnableLengthMin = false
  JointType = 0 (Fixed)
  LengthMax = 0
  LengthMin = 0
  Offset2 = pos=(0,0,9) rot=(0,0,1;0rad)
  Placement1 = pos=(-17.5,0,3.4e-15) rot=(0,0,1;0rad)
  Placement2 = pos=(-0.3,15,220) rot=(-0.707107,0,0.707107;3.14159rad)
  Reference1 = -> Assembly [_030_angle_bracket_005.Edge3,_030_angle_bracket_005.Edge3]
  Reference2 = -> Assembly [alu_prof_3030_200_001.Edge73,alu_prof_3030_200_001.Edge73]
FEATURE [App::FeaturePython] Joint015  label="Fixed015"  # Assembly joint (typed FeaturePython)
  Activated = true
  AngleMax = 0
  AngleMin = 0
  Detach1 = false
  Detach2 = false
  Distance = 0
  Distance2 = 0
  EnableAngleMax = false
  EnableAngleMin = false
  EnableLengthMax = false
  EnableLengthMin = false
  JointType = 0 (Fixed)
  LengthMax = 0
  LengthMin = 0
  Offset2 = pos=(0,0,4.5) rot=(0,0,-1;1.5708rad)
  Placement1 = pos=(-17.5,1.8e-15,-3e-16) rot=(0,0,1;0rad)
  Placement2 = pos=(-15,0.1,400) rot=(0,0.707107,0.707107;3.14159rad)
  Reference1 = -> Assembly [_030_angle_bracket_003.Edge3,_030_angle_bracket_003.Edge3]
  Reference2 = -> Assembly [alu_prof_3030_450_003.Edge78,alu_prof_3030_450_003.Vertex78]
FEATURE [App::FeaturePython] Joint018  label="Fixed018"  # Assembly joint (typed FeaturePython)
  Activated = true
  AngleMax = 0
  AngleMin = 0
  Detach1 = false
  Detach2 = false
  Distance = 0
  Distance2 = 0
  EnableAngleMax = false
  EnableAngleMin = false
  EnableLengthMax = false
  EnableLengthMin = false
  JointType = 0 (Fixed)
  LengthMax = 0
  LengthMin = 0
  Offset2 = pos=(0,0,-4.5) rot=(0,0,-1;1.5708rad)
  Placement1 = pos=(-4.4,-15,220) rot=(0.707107,0,0.707107;3.14159rad)
  Placement2 = pos=(-17.5,0,-4.5) rot=(0,0,-1;1.5708rad)
  Reference1 = -> Assembly [alu_prof_3030_200_002.Edge205,alu_prof_3030_200_002.Vertex138]
  Reference2 = -> Assembly [_030_angle_bracket_002.Edge3,_030_angle_bracket_002.Edge3]
FEATURE [App::Link] _030_angle_bracket_006  label="3030-angle-bracket-007"
  LinkPlacement = pos=(447.5,-0.3,250) rot=(0,0.707107,0.707107;3.14159rad)
  LinkedObject = -> Part__Feature003
  Placement = pos=(447.5,-0.3,250) rot=(0,0.707107,0.707107;3.14159rad)
FEATURE [App::FeaturePython] Joint019  label="Fixed019"  # Assembly joint (typed FeaturePython)
  Activated = true
  AngleMax = 0
  AngleMin = 0
  Detach1 = false
  Detach2 = false
  Distance = 0
  Distance2 = 0
  EnableAngleMax = false
  EnableAngleMin = false
  EnableLengthMax = false
  EnableLengthMin = false
  JointType = 0 (Fixed)
  LengthMax = 0
  LengthMin = 0
  Offset2 = pos=(0,0,-9) rot=(0,0,1;0rad)
  Placement1 = pos=(-17.5,0,-4e-16) rot=(0,0,1;0rad)
  Placement2 = pos=(15,-0.3,-50) rot=(0.57735,0.57735,0.57735;4.18879rad)
  Reference1 = -> Assembly [_030_angle_bracket_006.Edge3,_030_angle_bracket_006.Edge3]
  Reference2 = -> Assembly [alu_prof_3030_450_000.Edge197,alu_prof_3030_450_000.Edge197]
FEATURE [App::Link] _030_angle_bracket_007  label="3030-angle-bracket-008"
  LinkPlacement = pos=(465,-1.3,472.5) rot=(-0.57735,0.57735,0.57735;2.0944rad)
  LinkedObject = -> Part__Feature003
  Placement = pos=(465,-1.3,472.5) rot=(-0.57735,0.57735,0.57735;2.0944rad)
FEATURE [App::FeaturePython] Joint020  label="Fixed020"  # Assembly joint (typed FeaturePython)
  Activated = true
  AngleMax = 0
  AngleMin = 0
  Detach1 = false
  Detach2 = false
  Distance = 0
  Distance2 = 0
  EnableAngleMax = false
  EnableAngleMin = false
  EnableLengthMax = false
  EnableLengthMin = false
  JointType = 0 (Fixed)
  LengthMax = 0
  LengthMin = 0
  Offset2 = pos=(0,0,-4) rot=(0,0,-1;1.5708rad)
  Placement1 = pos=(-17.5,0,14) rot=(0,0,1;0rad)
  Placement2 = pos=(-15,12.7,-50) rot=(0,-0.707107,0.707107;3.14159rad)
  Reference1 = -> Assembly [_030_angle_bracket_007.Edge3,_030_angle_bracket_007.Vertex3]
  Reference2 = -> Assembly [alu_prof_3030_450_003.Edge173,alu_prof_3030_450_003.Edge173]
FEATURE [App::Link] _030_angle_bracket_008  label="3030-angle-bracket-009"
  LinkPlacement = pos=(32.5,-15,234.7) rot=(-1,0,0;3.14159rad)
  LinkedObject = -> Part__Feature003
  Placement = pos=(32.5,-15,234.7) rot=(-1,0,0;3.14159rad)
FEATURE [App::Link] _030_angle_bracket_009  label="3030-angle-bracket-010"
  LinkPlacement = pos=(15,0.3,267.5) rot=(0.57735,0.57735,0.57735;4.18879rad)
  LinkedObject = -> Part__Feature003
  Placement = pos=(15,0.3,267.5) rot=(0.57735,0.57735,0.57735;4.18879rad)
FEATURE [App::Link] _030_angle_bracket_010  label="3030-angle-bracket-011"
  LinkPlacement = pos=(447.5,-15,235.3) rot=(0,0,1;3.14159rad)
  LinkedObject = -> Part__Feature003
  Placement = pos=(447.5,-15,235.3) rot=(0,0,1;3.14159rad)
FEATURE [App::FeaturePython] Joint021  label="Fixed021"  # Assembly joint (typed FeaturePython)
  Activated = true
  AngleMax = 0
  AngleMin = 0
  Detach1 = false
  Detach2 = false
  Distance = 0
  Distance2 = 0
  EnableAngleMax = false
  EnableAngleMin = false
  EnableLengthMax = false
  EnableLengthMin = false
  JointType = 0 (Fixed)
  LengthMax = 0
  LengthMin = 0
  Offset2 = pos=(0,0,9) rot=(0,0,1;1.5708rad)
  Placement1 = pos=(-17.5,0,0) rot=(0,0,1;0rad)
  Placement2 = pos=(15,0.3,220) rot=(1,0,0;4.71239rad)
  Reference1 = -> Assembly [_030_angle_bracket_008.Edge3,_030_angle_bracket_008.Edge3]
  Reference2 = -> Assembly [alu_prof_3030_200_002.Edge7,alu_prof_3030_200_002.Edge7]
FEATURE [App::FeaturePython] Joint022  label="Fixed022"  # Assembly joint (typed FeaturePython)
  Activated = true
  AngleMax = 0
  AngleMin = 0
  Detach1 = false
  Detach2 = false
  Distance = 0
  Distance2 = 0
  EnableAngleMax = false
  EnableAngleMin = false
  EnableLengthMax = false
  EnableLengthMin = false
  JointType = 0 (Fixed)
  LengthMax = 0
  LengthMin = 0
  Offset2 = pos=(0,0,-9) rot=(0,0,1;1.5708rad)
  Placement1 = pos=(-17.5,3.6e-15,-6e-16) rot=(0,0,1;0rad)
  Placement2 = pos=(15,0.3,400) rot=(-1,0,0;4.71239rad)
  Reference1 = -> Assembly [_030_angle_bracket_009.Edge3,_030_angle_bracket_009.Edge3]
  Reference2 = -> Assembly [alu_prof_3030_450_000.Edge14,alu_prof_3030_450_000.Edge14]
FEATURE [App::FeaturePython] Joint023  label="Fixed023"  # Assembly joint (typed FeaturePython)
  Activated = true
  AngleMax = 0
  AngleMin = 0
  Detach1 = false
  Detach2 = false
  Distance = 0
  Distance2 = 0
  EnableAngleMax = false
  EnableAngleMin = false
  EnableLengthMax = false
  EnableLengthMin = false
  JointType = 0 (Fixed)
  LengthMax = 0
  LengthMin = 0
  Offset2 = pos=(0,0,9) rot=(0,0,1;0rad)
  Placement1 = pos=(-17.5,0,0) rot=(0,0,1;0rad)
  Placement2 = pos=(0.3,-15,-50) rot=(0.707107,0,0.707107;3.14159rad)
  Reference1 = -> Assembly [_030_angle_bracket_010.Edge3,_030_angle_bracket_010.Edge3]
  Reference2 = -> Assembly [alu_prof_3030_450_000.Edge151,alu_prof_3030_450_000.Edge151]
FEATURE [App::Link] _030_angle_bracket_011  label="3030-angle-bracket-012"
  LinkPlacement = pos=(480.3,-15,267.5) rot=(0.707107,0,0.707107;3.14159rad)
  LinkedObject = -> Part__Feature003
  Placement = pos=(480.3,-15,267.5) rot=(0.707107,0,0.707107;3.14159rad)
FEATURE [App::Link] _030_angle_bracket_012  label="3030-angle-bracket-013"
  LinkPlacement = pos=(480.3,-197.5,250) rot=(0.57735,0.57735,0.57735;2.0944rad)
  LinkedObject = -> Part__Feature003
  Placement = pos=(480.3,-197.5,250) rot=(0.57735,0.57735,0.57735;2.0944rad)
FEATURE [App::Link] _030_angle_bracket_013  label="3030-angle-bracket-014"
  LinkPlacement = pos=(479.7,-215,472.5) rot=(0,1,0;1.5708rad)
  LinkedObject = -> Part__Feature003
  Placement = pos=(479.7,-215,472.5) rot=(0,1,0;1.5708rad)
FEATURE [App::FeaturePython] Joint024  label="Fixed024"  # Assembly joint (typed FeaturePython)
  Activated = true
  AngleMax = 0
  AngleMin = 0
  Detach1 = false
  Detach2 = false
  Distance = 0
  Distance2 = 0
  EnableAngleMax = false
  EnableAngleMin = false
  EnableLengthMax = false
  EnableLengthMin = false
  JointType = 0 (Fixed)
  LengthMax = 0
  LengthMin = 0
  Offset2 = pos=(0,0,9) rot=(0,0,1;1.5708rad)
  Placement1 = pos=(-17.5,-1.8e-15,0) rot=(0,0,1;0rad)
  Placement2 = pos=(0.3,-15,220) rot=(0.57735,-0.57735,0.57735;4.18879rad)
  Reference1 = -> Assembly [_030_angle_bracket_011.Edge3,_030_angle_bracket_011.Edge3]
  Reference2 = -> Assembly [alu_prof_3030_200_003.Edge205,alu_prof_3030_200_003.Edge205]
FEATURE [App::Link] _030_angle_bracket_014  label="3030-angle-bracket-015"
  LinkPlacement = pos=(480.3,-32.5,490) rot=(-0.57735,0.57735,-0.57735;2.0944rad)
  LinkedObject = -> Part__Feature003
  Placement = pos=(480.3,-32.5,490) rot=(-0.57735,0.57735,-0.57735;2.0944rad)
FEATURE [App::Link] _030_angle_bracket_015  label="3030-angle-bracket-016"
  LinkPlacement = pos=(447.5,-15,504.7) rot=(0,0,-1;3.14159rad)
  LinkedObject = -> Part__Feature003
  Placement = pos=(447.5,-15,504.7) rot=(0,0,-1;3.14159rad)
FEATURE [App::FeaturePython] Joint027  label="Fixed027"  # Assembly joint (typed FeaturePython)
  Activated = true
  AngleMax = 0
  AngleMin = 0
  Detach1 = false
  Detach2 = false
  Distance = 0
  Distance2 = 0
  EnableAngleMax = false
  EnableAngleMin = false
  EnableLengthMax = false
  EnableLengthMin = false
  JointType = 0 (Fixed)
  LengthMax = 0
  LengthMin = 0
  Offset2 = pos=(0,0,-9) rot=(0,0,1;0rad)
  Placement1 = pos=(-17.5,0,0) rot=(0,0,1;0rad)
  Placement2 = pos=(-0.3,-15,-50) rot=(0.707107,0,0.707107;3.14159rad)
  Reference1 = -> Assembly [_030_angle_bracket_015.Edge3,_030_angle_bracket_015.Edge3]
  Reference2 = -> Assembly [alu_prof_3030_450_003.Edge131,alu_prof_3030_450_003.Edge131]
FEATURE [App::FeaturePython] Joint028  label="Fixed028"  # Assembly joint (typed FeaturePython)
  Activated = true
  AngleMax = 0
  AngleMin = 0
  Detach1 = false
  Detach2 = false
  Distance = 0
  Distance2 = 0
  EnableAngleMax = false
  EnableAngleMin = false
  EnableLengthMax = false
  EnableLengthMin = false
  JointType = 0 (Fixed)
  LengthMax = 0
  LengthMin = 0
  Offset2 = pos=(0,0,-9) rot=(0,0,1;0rad)
  Placement1 = pos=(-17.5,0,0) rot=(0,0,1;0rad)
  Placement2 = pos=(0.3,15,220) rot=(-0.707107,0,0.707107;3.14159rad)
  Reference1 = -> Assembly [_030_angle_bracket_014.Edge3,_030_angle_bracket_014.Edge3]
  Reference2 = -> Assembly [alu_prof_3030_200_000.Edge133,alu_prof_3030_200_000.Edge133]
FEATURE [App::FeaturePython] Joint029  label="Fixed029"  # Assembly joint (typed FeaturePython)
  Activated = true
  AngleMax = 0
  AngleMin = 0
  Detach1 = false
  Detach2 = false
  Distance = 0
  Distance2 = 0
  EnableAngleMax = false
  EnableAngleMin = false
  EnableLengthMax = false
  EnableLengthMin = false
  JointType = 0 (Fixed)
  LengthMax = 0
  LengthMin = 0
  Offset2 = pos=(0,0,9) rot=(0,0,1;0rad)
  Placement1 = pos=(-17.5,-2.84e-14,1.2e-15) rot=(0,0,1;0rad)
  Placement2 = pos=(0.3,-15,20) rot=(0.707107,0,0.707107;3.14159rad)
  Reference1 = -> Assembly [_030_angle_bracket_000.Edge3,_030_angle_bracket_000.Edge3]
  Reference2 = -> Assembly [alu_prof_3030_200_002.Edge203,alu_prof_3030_200_002.Edge203]
FEATURE [App::FeaturePython] Joint030  label="Fixed030"  # Assembly joint (typed FeaturePython)
  Activated = true
  AngleMax = 0
  AngleMin = 0
  Detach1 = false
  Detach2 = false
  Distance = 0
  Distance2 = 0
  EnableAngleMax = false
  EnableAngleMin = false
  EnableLengthMax = false
  EnableLengthMin = false
  JointType = 0 (Fixed)
  LengthMax = 0
  LengthMin = 0
  Offset2 = pos=(0,0,5) rot=(0,0,-1;1.5708rad)
  Placement1 = pos=(-17.5,0,-14) rot=(0,0,1;0rad)
  Placement2 = pos=(-13.7,15,20) rot=(-0.57735,-0.57735,0.57735;2.0944rad)
  Reference1 = -> Assembly [_030_angle_bracket_004.Edge3,_030_angle_bracket_004.Vertex4]
  Reference2 = -> Assembly [alu_prof_3030_200_001.Edge131,alu_prof_3030_200_001.Edge131]
FEATURE [App::FeaturePython] Joint031  label="Fixed031"  # Assembly joint (typed FeaturePython)
  Activated = true
  AngleMax = 0
  AngleMin = 0
  Detach1 = false
  Detach2 = false
  Distance = 0
  Distance2 = 0
  EnableAngleMax = false
  EnableAngleMin = false
  EnableLengthMax = false
  EnableLengthMin = false
  JointType = 0 (Fixed)
  LengthMax = 0
  LengthMin = 0
  Offset2 = pos=(0,0,9) rot=(0,0,1;0rad)
  Placement1 = pos=(-17.5,0,0) rot=(0,0,1;0rad)
  Placement2 = pos=(0.3,-15,20) rot=(0.707107,0,0.707107;3.14159rad)
  Reference1 = -> Assembly [_030_angle_bracket_012.Edge3,_030_angle_bracket_012.Edge3]
  Reference2 = -> Assembly [alu_prof_3030_200_003.Edge203,alu_prof_3030_200_003.Edge203]
FEATURE [App::FeaturePython] Joint032  label="Fixed032"  # Assembly joint (typed FeaturePython)
  Activated = true
  AngleMax = 0
  AngleMin = 0
  Detach1 = false
  Detach2 = false
  Distance = 0
  Distance2 = 0
  EnableAngleMax = false
  EnableAngleMin = false
  EnableLengthMax = false
  EnableLengthMin = false
  JointType = 0 (Fixed)
  LengthMax = 0
  LengthMin = 0
  Offset2 = pos=(0,0,9) rot=(0,0,-1;1.5708rad)
  Placement1 = pos=(-17.5,0,0) rot=(0,0,1;0rad)
  Placement2 = pos=(-0.3,15,20) rot=(-0.57735,-0.57735,0.57735;2.0944rad)
  Reference1 = -> Assembly [_030_angle_bracket_013.Edge3,_030_angle_bracket_013.Edge3]
  Reference2 = -> Assembly [alu_prof_3030_200_000.Edge71,alu_prof_3030_200_000.Edge71]
FEATURE [App::Link] din_mount_part
  LinkPlacement = pos=(480,-79,490) rot=(0.707107,-0.707107,0;3.14159rad)
  LinkedObject = -> <external din_mount.FCStd>#Part
  Placement = pos=(480,-79,490) rot=(0.707107,-0.707107,0;3.14159rad)
FEATURE [App::Link] din_mount_part001
  LinkPlacement = pos=(480,-140,490) rot=(0.707107,-0.707107,0;3.14159rad)
  LinkedObject = -> <external din_mount.FCStd>#Part
  Placement = pos=(480,-140,490) rot=(0.707107,-0.707107,0;3.14159rad)
FEATURE [App::FeaturePython] Joint033  label="Fixed033"  # Assembly joint (typed FeaturePython)
  Activated = true
  AngleMax = 0
  AngleMin = 0
  Detach1 = false
  Detach2 = false
  Distance = 0
  Distance2 = 0
  EnableAngleMax = false
  EnableAngleMin = false
  EnableLengthMax = false
  EnableLengthMin = false
  JointType = 0 (Fixed)
  LengthMax = 0
  LengthMin = 0
  Offset2 = pos=(2,0,-36) rot=(0,0,-1;1.5708rad)
  Placement1 = pos=(0,15,0) rot=(-0.707107,0,0.707107;3.14159rad)
  Placement2 = pos=(-15,15,156) rot=(-0.707107,0.707107,0;3.14159rad)
  Reference1 = -> Assembly [din_mount_part.Body.Edge27,din_mount_part.Body.Edge27]
  Reference2 = -> Assembly [alu_prof_3030_200_000.Edge132,alu_prof_3030_200_000.Edge132]
FEATURE [Part::Feature] Part__Feature006  label="din_rail_180mm"
  shape: bbox 180 x 7.5 x 35 mm, 50 faces (baked)
FEATURE [App::Link] din_rail_180mm  label="din_rail_180mm001"
  LinkPlacement = pos=(465,3,437.5) rot=(0,0,-1;4.71239rad)
  LinkedObject = -> Part__Feature006
  Placement = pos=(465,3,437.5) rot=(0,0,-1;4.71239rad)
FEATURE [App::FeaturePython] Joint034  label="Fixed034"  # Assembly joint (typed FeaturePython)
  Activated = true
  AngleMax = 0
  AngleMin = 0
  Detach1 = false
  Detach2 = false
  Distance = 0
  Distance2 = 0
  EnableAngleMax = false
  EnableAngleMin = false
  EnableLengthMax = false
  EnableLengthMin = false
  JointType = 0 (Fixed)
  LengthMax = 0
  LengthMin = 0
  Offset1 = pos=(-7,0,0) rot=(0,0,1;0rad)
  Placement1 = pos=(-32,-7.92893,2.5) rot=(0,0,1;0rad)
  Placement2 = pos=(25,-7.92893,2.5) rot=(0,0,1;0rad)
  Reference1 = -> Assembly [din_mount_part001.Body.Edge37,din_mount_part001.Body.Edge37]
  Reference2 = -> Assembly [din_mount_part.Body.Edge47,din_mount_part.Body.Edge47]
FEATURE [App::FeaturePython] Joint035  label="Fixed035"  # Assembly joint (typed FeaturePython)
  Activated = true
  AngleMax = 0
  AngleMin = 0
  Detach1 = false
  Detach2 = false
  Distance = 0
  Distance2 = 0
  EnableAngleMax = false
  EnableAngleMin = false
  EnableLengthMax = false
  EnableLengthMin = false
  JointType = 0 (Fixed)
  LengthMax = 0
  LengthMin = 0
  Offset1 = pos=(0,-49,0) rot=(0,0,1;0rad)
  Offset2 = pos=(0,0,0) rot=(0,0,1;1.5708rad)
  Placement1 = pos=(-82,-8.2e-15,1.733e-13) rot=(-0.57735,-0.57735,0.57735;4.18879rad)
  Placement2 = pos=(0,15,52.5) rot=(0.57735,0.57735,0.57735;4.18879rad)
  Reference1 = -> Assembly [din_rail_180mm.Edge62,din_rail_180mm.Edge62]
  Reference2 = -> Assembly [din_mount_part.Body.Edge30,din_mount_part.Body.Edge30]
FEATURE [App::Link] alu_prof_3030_450_004  label="alu-prof-3030-450-005"
  LinkPlacement = pos=(65,-5.3e-15,415) rot=(0,-1,0;4.71239rad)
  LinkedObject = -> Part__Feature002
  Placement = pos=(65,-5.3e-15,415) rot=(0,-1,0;4.71239rad)
FEATURE [App::Link] _030_angle_bracket_016  label="3030-angle-bracket-017"
  LinkPlacement = pos=(32.5,-0.2,400) rot=(-1,0,0;1.5708rad)
  LinkedObject = -> Part__Feature003
  Placement = pos=(32.5,-0.2,400) rot=(-1,0,0;1.5708rad)
FEATURE [App::Link] _030_angle_bracket_017  label="3030-angle-bracket-018"
  LinkPlacement = pos=(447.5,-0.3,400) rot=(0,0.707107,-0.707107;3.14159rad)
  LinkedObject = -> Part__Feature003
  Placement = pos=(447.5,-0.3,400) rot=(0,0.707107,-0.707107;3.14159rad)
FEATURE [App::FeaturePython] Joint036  label="Fixed036"  # Assembly joint (typed FeaturePython)
  Activated = true
  AngleMax = 0
  AngleMin = 0
  Detach1 = false
  Detach2 = false
  Distance = 0
  Distance2 = 0
  EnableAngleMax = false
  EnableAngleMin = false
  EnableLengthMax = false
  EnableLengthMin = false
  JointType = 0 (Fixed)
  LengthMax = 0
  LengthMin = 0
  Offset1 = pos=(0,-90,0) rot=(0,0,1;0rad)
  Offset2 = pos=(0,0,0) rot=(0,0,1;3.14159rad)
  Placement1 = pos=(-105,8.7,400) rot=(0.57735,0.57735,0.57735;4.18879rad)
  Placement2 = pos=(15,8.7,-50) rot=(0.57735,-0.57735,-0.57735;4.18879rad)
  Reference1 = -> Assembly [alu_prof_3030_450_004.Edge58,alu_prof_3030_450_004.Edge58]
  Reference2 = -> Assembly [alu_prof_3030_450_003.Edge197,alu_prof_3030_450_003.Edge197]
FEATURE [App::FeaturePython] Joint037  label="Fixed037"  # Assembly joint (typed FeaturePython)
  Activated = true
  AngleMax = 0
  AngleMin = 0
  Detach1 = false
  Detach2 = false
  Distance = 0
  Distance2 = 0
  EnableAngleMax = false
  EnableAngleMin = false
  EnableLengthMax = false
  EnableLengthMin = false
  JointType = 0 (Fixed)
  LengthMax = 0
  LengthMin = 0
  Offset2 = pos=(0,0,22.5) rot=(0,0,1;0rad)
  Placement1 = pos=(-17.5,0,14) rot=(0,0,1;0rad)
  Placement2 = pos=(15,13.8,-50) rot=(0.57735,0.57735,0.57735;4.18879rad)
  Reference1 = -> Assembly [_030_angle_bracket_016.Edge3,_030_angle_bracket_016.Vertex3]
  Reference2 = -> Assembly [alu_prof_3030_450_004.Edge217,alu_prof_3030_450_004.Edge217]
FEATURE [App::FeaturePython] Joint038  label="Fixed038"  # Assembly joint (typed FeaturePython)
  Activated = true
  AngleMax = 0
  AngleMin = 0
  Detach1 = false
  Detach2 = false
  Distance = 0
  Distance2 = 0
  EnableAngleMax = false
  EnableAngleMin = false
  EnableLengthMax = false
  EnableLengthMin = false
  JointType = 0 (Fixed)
  LengthMax = 0
  LengthMin = 0
  Offset2 = pos=(0,0,9) rot=(0,0,1;0rad)
  Placement1 = pos=(-17.5,0,-6e-16) rot=(0,0,1;0rad)
  Placement2 = pos=(15,-0.3,400) rot=(-0.57735,-0.57735,0.57735;4.18879rad)
  Reference1 = -> Assembly [_030_angle_bracket_017.Edge3,_030_angle_bracket_017.Edge3]
  Reference2 = -> Assembly [alu_prof_3030_450_004.Edge34,alu_prof_3030_450_004.Edge34]
FEATURE [App::Link] power_supply_bracket_part  label="power-supply-bracket-part"
  LinkPlacement = pos=(283,15,400) rot=(0.57735,-0.57735,-0.57735;2.0944rad)
  LinkedObject = -> <external power-supply-bracket.FCStd>#Part
  Placement = pos=(283,15,400) rot=(0.57735,-0.57735,-0.57735;2.0944rad)
FEATURE [App::Link] power_supply_bracket_part001  label="power-supply-bracket-part001"
  LinkPlacement = pos=(347,15,400) rot=(0.57735,-0.57735,-0.57735;2.0944rad)
  LinkedObject = -> <external power-supply-bracket.FCStd>#Part
  Placement = pos=(347,15,400) rot=(0.57735,-0.57735,-0.57735;2.0944rad)
FEATURE [App::FeaturePython] Joint039  label="Fixed039"  # Assembly joint (typed FeaturePython)
  Activated = true
  AngleMax = 0
  AngleMin = 0
  Detach1 = false
  Detach2 = false
  Distance = 0
  Distance2 = 0
  EnableAngleMax = false
  EnableAngleMin = false
  EnableLengthMax = false
  EnableLengthMin = false
  JointType = 0 (Fixed)
  LengthMax = 0
  LengthMin = 0
  Offset2 = pos=(0,2,-120) rot=(0,0,-1;1.5708rad)
  Placement1 = pos=(0,30,-13) rot=(0,0,1;0rad)
  Placement2 = pos=(-15,15,295) rot=(-0.707107,0.707107,0;3.14159rad)
  Reference1 = -> Assembly [power_supply_bracket_part001.Body.Edge82,power_supply_bracket_part001.Body.Edge82]
  Reference2 = -> Assembly [alu_prof_3030_450_004.Edge292,alu_prof_3030_450_004.Edge292]
FEATURE [App::FeaturePython] Joint040  label="Fixed040"  # Assembly joint (typed FeaturePython)
  Activated = true
  AngleMax = 0
  AngleMin = 0
  Detach1 = false
  Detach2 = false
  Distance = 0
  Distance2 = 0
  EnableAngleMax = false
  EnableAngleMin = false
  EnableLengthMax = false
  EnableLengthMin = false
  JointType = 0 (Fixed)
  LengthMax = 0
  LengthMin = 0
  Offset2 = pos=(-30,0,0) rot=(0,0,1;0rad)
  Placement1 = pos=(15,30,-30) rot=(-0.707107,0,0.707107;3.14159rad)
  Placement2 = pos=(15,30,34) rot=(-0.707107,0,0.707107;3.14159rad)
  Reference1 = -> Assembly [power_supply_bracket_part.Body.Edge83,power_supply_bracket_part.Body.Edge83]
  Reference2 = -> Assembly [power_supply_bracket_part001.Body.Edge9,power_supply_bracket_part001.Body.Edge9]
FEATURE [Part::Feature] Part__Feature007  label="LRS-150"
  shape: bbox 97.19 x 29.5 x 159 mm, 315 faces (baked)
FEATURE [Part::Feature] Part__Feature008  label="LRS-151"
  shape: bbox 95.3 x 28.5 x 143 mm, 2203 faces (baked)
FEATURE [Part::Feature] Part__Feature009  label="LRS-152"
  shape: bbox 94.01 x 16.61 x 152.1 mm, 1017 faces (baked)
FEATURE [Part::Feature] Part__Feature010  label="LRS-153"
  shape: bbox 4.818 x 5.068 x 4.818 mm, 39 faces (baked)
FEATURE [App::Part] LRS_150  label="LRS-154"
  Group = -> [Part__Feature007,Part__Feature008,Part__Feature009,Part__Feature010]
  Origin = -> Origin002
FEATURE [App::Link] LRS_154  label="LRS-155"
  LinkPlacement = pos=(283,-104.5,414.75) rot=(-0.57735,-0.57735,0.57735;4.18879rad)
  LinkedObject = -> LRS_150
  Placement = pos=(283,-104.5,414.75) rot=(-0.57735,-0.57735,0.57735;4.18879rad)
FEATURE [App::Link] LRS_155  label="LRS-156"
  LinkPlacement = pos=(347,-103.25,414.75) rot=(-0.57735,-0.57735,0.57735;4.18879rad)
  LinkedObject = -> LRS_150
  Placement = pos=(347,-103.25,414.75) rot=(-0.57735,-0.57735,0.57735;4.18879rad)
FEATURE [App::FeaturePython] Joint041  label="Fixed041"  # Assembly joint (typed FeaturePython)
  Activated = true
  AngleMax = 0
  AngleMin = 0
  Detach1 = false
  Detach2 = false
  Distance = 0
  Distance2 = 0
  EnableAngleMax = false
  EnableAngleMin = false
  EnableLengthMax = false
  EnableLengthMin = false
  JointType = 0 (Fixed)
  LengthMax = 0
  LengthMin = 0
  Offset1 = pos=(0,0,0) rot=(0,1,0;0.785398rad)
  Placement1 = pos=(47.75,15,58.75) rot=(0,1,0;4.71239rad)
  Placement2 = pos=(177,-33,-15) rot=(-1,0,0;1.5708rad)
  Reference1 = -> Assembly [LRS_155.Part__Feature007.Edge487,LRS_155.Part__Feature007.Vertex360]
  Reference2 = -> Assembly [power_supply_bracket_part001.Body.Edge170,power_supply_bracket_part001.Body.Edge170]
FEATURE [App::FeaturePython] Joint042  label="Fixed042"  # Assembly joint (typed FeaturePython)
  Activated = true
  AngleMax = 0
  AngleMin = 0
  Detach1 = false
  Detach2 = false
  Distance = 0
  Distance2 = 0
  EnableAngleMax = false
  EnableAngleMin = false
  EnableLengthMax = false
  EnableLengthMin = false
  JointType = 0 (Fixed)
  LengthMax = 0
  LengthMin = 0
  Offset2 = pos=(0,0,0) rot=(0,0,1;3.14159rad)
  Placement1 = pos=(47.75,15,57.5) rot=(0,1,0;1.5708rad)
  Placement2 = pos=(177,-33,-15) rot=(0,0.707107,0.707107;3.14159rad)
  Reference1 = -> Assembly [LRS_154.Part__Feature007.Edge488,LRS_154.Part__Feature007.Edge488]
  Reference2 = -> Assembly [power_supply_bracket_part.Body.Edge170,power_supply_bracket_part.Body.Edge170]
FEATURE [App::Link] dlp_power_supply_bracket_part  label="dlp-power-supply-bracket-part"
  LinkPlacement = pos=(226,-36.5,425) rot=(0,0,1;0rad)
  LinkedObject = -> <external dlp-power-supply-bracket.FCStd>#Part
  Placement = pos=(226,-36.5,425) rot=(0,0,1;0rad)
FEATURE [App::FeaturePython] Joint043  label="Fixed043"  # Assembly joint (typed FeaturePython)
  Activated = true
  AngleMax = 0
  AngleMin = 0
  Detach1 = false
  Detach2 = false
  Distance = 0
  Distance2 = 0
  EnableAngleMax = false
  EnableAngleMin = false
  EnableLengthMax = false
  EnableLengthMin = false
  JointType = 0 (Fixed)
  LengthMax = 0
  LengthMin = 0
  Offset2 = pos=(0,0,-70) rot=(0,0,1;1.5708rad)
  Placement1 = pos=(0,21.5,5) rot=(0.707107,0,0.707107;3.14159rad)
  Placement2 = pos=(30,30,57) rot=(0.707107,0.707107,0;3.14159rad)
  Reference1 = -> Assembly [dlp_power_supply_bracket_part.Body.Edge15,dlp_power_supply_bracket_part.Body.Edge15]
  Reference2 = -> Assembly [power_supply_bracket_part.Body.Edge77,power_supply_bracket_part.Body.Edge77]
FEATURE [App::Link] smc100c_bracket_part  label="smc100c-bracket-part"
  LinkPlacement = pos=(171,-194,435) rot=(0,0,-1;4.71239rad)
  LinkedObject = -> <external smc100c-bracket.FCStd>#Part
  Placement = pos=(171,-194,435) rot=(0,0,-1;4.71239rad)
FEATURE [App::Link] smc100c_bracket_part001  label="smc100c-bracket-part001"
  LinkPlacement = pos=(116,-194,435) rot=(0,0,-1;4.71239rad)
  LinkedObject = -> <external smc100c-bracket.FCStd>#Part
  Placement = pos=(116,-194,435) rot=(0,0,-1;4.71239rad)
FEATURE [App::FeaturePython] Joint044  label="Fixed044"  # Assembly joint (typed FeaturePython)
  Activated = true
  AngleMax = 0
  AngleMin = 0
  Detach1 = false
  Detach2 = false
  Distance = 0
  Distance2 = 0
  EnableAngleMax = false
  EnableAngleMin = false
  EnableLengthMax = false
  EnableLengthMin = false
  JointType = 0 (Fixed)
  LengthMax = 0
  LengthMin = 0
  Offset2 = pos=(0,0,-140) rot=(0,0,1;1.5708rad)
  Placement1 = pos=(179,15,-5) rot=(0.57735,0.57735,0.57735;4.18879rad)
  Placement2 = pos=(30,30,127) rot=(0.707107,0.707107,0;3.14159rad)
  Reference1 = -> Assembly [smc100c_bracket_part.Body.Edge49,smc100c_bracket_part.Body.Edge49]
  Reference2 = -> Assembly [power_supply_bracket_part.Body.Edge77,power_supply_bracket_part.Body.Edge77]
FEATURE [App::FeaturePython] Joint045  label="Fixed045"  # Assembly joint (typed FeaturePython)
  Activated = true
  AngleMax = 0
  AngleMin = 0
  Detach1 = false
  Detach2 = false
  Distance = 0
  Distance2 = 0
  EnableAngleMax = false
  EnableAngleMin = false
  EnableLengthMax = false
  EnableLengthMin = false
  JointType = 0 (Fixed)
  LengthMax = 0
  LengthMin = 0
  Offset2 = pos=(0,0,40) rot=(0,0,1;0rad)
  Placement1 = pos=(179,15,-5) rot=(0.57735,0.57735,0.57735;4.18879rad)
  Placement2 = pos=(179,70,-5) rot=(0.57735,0.57735,0.57735;4.18879rad)
  Reference1 = -> Assembly [smc100c_bracket_part001.Body.Edge49,smc100c_bracket_part001.Body.Edge49]
  Reference2 = -> Assembly [smc100c_bracket_part.Body.Edge49,smc100c_bracket_part.Body.Vertex42]
FEATURE [App::Link] SMC100CC  label="SMC100CC001"
  LinkPlacement = pos=(92.7646,-343.5,357.708) rot=(-0.57735,0.57735,0.57735;2.0944rad)
  LinkedObject = -> Part__Feature004
  Placement = pos=(92.7646,-343.5,357.708) rot=(-0.57735,0.57735,0.57735;2.0944rad)
FEATURE [App::Link] SMC100CC001  label="SMC100CC002"
  LinkPlacement = pos=(147.765,-343.5,357.708) rot=(-0.57735,0.57735,0.57735;2.0944rad)
  LinkedObject = -> Part__Feature004
  Placement = pos=(147.765,-343.5,357.708) rot=(-0.57735,0.57735,0.57735;2.0944rad)
FEATURE [App::FeaturePython] Joint046  label="Fixed046"  # Assembly joint (typed FeaturePython)
  Activated = true
  AngleMax = 0
  AngleMin = 0
  Detach1 = false
  Detach2 = false
  Distance = 0
  Distance2 = 0
  EnableAngleMax = false
  EnableAngleMin = false
  EnableLengthMax = false
  EnableLengthMin = false
  JointType = 0 (Fixed)
  LengthMax = 0
  LengthMin = 0
  Offset2 = pos=(0,0,0) rot=(0,0,1;1.5708rad)
  Placement1 = pos=(1.70837,-17.2354,239) rot=(0,-0.707107,-0.707107;3.14159rad)
  Placement2 = pos=(89.5,6,-79) rot=(0.57735,-0.57735,0.57735;2.0944rad)
  Reference1 = -> Assembly [SMC100CC.Edge5281,SMC100CC.Edge5281]
  Reference2 = -> Assembly [smc100c_bracket_part001.Body.Edge20,smc100c_bracket_part001.Body.Edge20]
FEATURE [App::FeaturePython] Joint047  label="Fixed047"  # Assembly joint (typed FeaturePython)
  Activated = true
  AngleMax = 0
  AngleMin = 0
  Detach1 = false
  Detach2 = false
  Distance = 0
  Distance2 = 0
  EnableAngleMax = false
  EnableAngleMin = false
  EnableLengthMax = false
  EnableLengthMin = false
  JointType = 0 (Fixed)
  LengthMax = 0
  LengthMin = 0
  Offset2 = pos=(0,0,0) rot=(0,0,1;1.5708rad)
  Placement1 = pos=(1.70837,-17.2354,239) rot=(0,-0.707107,-0.707107;3.14159rad)
  Placement2 = pos=(89.5,6,-79) rot=(0.57735,-0.57735,0.57735;2.0944rad)
  Reference1 = -> Assembly [SMC100CC001.Edge5281,SMC100CC001.Edge5281]
  Reference2 = -> Assembly [smc100c_bracket_part.Body.Edge20,smc100c_bracket_part.Body.Edge20]
FEATURE [App::Link] ports_panel_part  label="ports-panel-part"
  LinkPlacement = pos=(501.2,-100,257.5) rot=(0.57735,-0.57735,-0.57735;2.0944rad)
  LinkedObject = -> <external ports-panel.FCStd>#Part
  Placement = pos=(501.2,-100,257.5) rot=(0.57735,-0.57735,-0.57735;2.0944rad)
FEATURE [App::FeaturePython] Joint048  label="Fixed048"  # Assembly joint (typed FeaturePython)
  Activated = true
  AngleMax = 0
  AngleMin = 0
  Detach1 = false
  Detach2 = false
  Distance = 0
  Distance2 = 0
  EnableAngleMax = false
  EnableAngleMin = false
  EnableLengthMax = false
  EnableLengthMin = false
  JointType = 0 (Fixed)
  LengthMax = 0
  LengthMin = 0
  Offset2 = pos=(0,0,-11.8) rot=(0,0,-1;1.5708rad)
  Placement1 = pos=(115,-2,6.2) rot=(0.57735,0.57735,0.57735;4.18879rad)
  Placement2 = pos=(15,-20.5,20) rot=(0,0.707107,0.707107;3.14159rad)
  Reference1 = -> Assembly [ports_panel_part.Body.Edge13,ports_panel_part.Body.Edge13]
  Reference2 = -> Assembly [alu_prof_3030_200_003.Edge5,alu_prof_3030_200_003.Edge5]
FEATURE [Assembly::JointGroup] Joints
  Group = -> [GroundedJoint,Joint,Joint001,Joint002,Joint003,Joint004,Joint005,Joint010,Joint013,Joint014,Joint015,Joint018,Joint019,Joint020,Joint021,Joint022,Joint023,Joint024,Joint027,Joint028,Joint029,Joint030,Joint031,Joint032,Joint033,Joint034,Joint035,Joint036,Joint037,Joint038,Joint039,Joint040,Joint041,Joint042,Joint043,Joint044,Joint045,Joint046,Joint047,Joint048]
FEATURE [Assembly::AssemblyObject] Assembly  label="electronics-box-assembly"
  Group = -> [Joints,alu_prof_3030_300_000,alu_prof_3030_450_000,GroundedJoint,Joint,alu_prof_3030_300_001,alu_prof_3030_200_000,alu_prof_3030_200_001,alu_prof_3030_200_002,alu_prof_3030_200_003,Joint001,Joint002,Joint003,Joint004,Joint005,alu_prof_3030_450_003,Joint010,_030_angle_bracket_000,_030_angle_bracket_001,_030_angle_bracket_002,_030_angle_bracket_003,_030_angle_bracket_004,_030_angle_bracket_005,+58 more]
  Origin = -> Origin
  Type = Assembly
---- part frame/frame.FCStd = doc fcstd_5eea95a91701 (65374 chars; too large to inline — full recipe in that document) ----
---- part panels/plexi-mount.FCStd = doc fcstd_8aadb9d5b53b ----
FCSTD DOCUMENT  (FreeCAD 1.0R39285 (Git))
Label: plexi-mount
License: All rights reserved
objects: Sketcher::SketchObject×6, PartDesign::Pad×4, PartDesign::Chamfer×4, PartDesign::Pocket×2, PartDesign::Body×2, App::Part×2
note: 44 computed .brp shape members not serialized (recipe doc carries the construction recipe); baked Part::Feature solids carry a one-line shape summary decoded from their .brp

FEATURE [Sketcher::SketchObject] Sketch
  ArcFitTolerance = 1e-06
  AttachmentSupport = -> [XY_Plane001]
  FullyConstrained = true
  MakeInternals = false
  MapMode = 5
  sketch-geometry (13):
    g0: LineSegment [constr] StartX=1e-16 StartY=0 StartZ=0 EndX=75 EndY=0 EndZ=0
    g1: LineSegment [constr] StartX=75 StartY=0 StartZ=0 EndX=75 EndY=30 EndZ=0
    g2: LineSegment [constr] StartX=75 StartY=30 StartZ=0 EndX=0 EndY=30 EndZ=0
    g3: LineSegment [constr] StartX=1e-16 StartY=30 StartZ=0 EndX=1e-16 EndY=0 EndZ=0
    g4: LineSegment [constr] StartX=1e-16 StartY=0 StartZ=0 EndX=30 EndY=0 EndZ=0
    g5: LineSegment [constr] StartX=30 StartY=0 StartZ=0 EndX=30 EndY=75 EndZ=0
    g6: LineSegment [constr] StartX=30 StartY=75 StartZ=0 EndX=0 EndY=75 EndZ=0
    g7: LineSegment [constr] StartX=1e-16 StartY=75 StartZ=0 EndX=1e-16 EndY=0 EndZ=0
    g8: LineSegment StartX=75 StartY=0 StartZ=0 EndX=75 EndY=30 EndZ=0
    g9: LineSegment StartX=30 StartY=75 StartZ=0 EndX=0 EndY=75 EndZ=0
    g10: LineSegment StartX=1e-16 StartY=75 StartZ=0 EndX=1e-16 EndY=0 EndZ=0
    g11: LineSegment StartX=1e-16 StartY=0 StartZ=0 EndX=75 EndY=0 EndZ=0
    g12: LineSegment StartX=30 StartY=75 StartZ=0 EndX=75 EndY=30 EndZ=0
  constraints (32):
    c: Coincident(g0,g1)
    c: Coincident(g1,g2)
    c: Coincident(g2,g3)
    c: Coincident(g3,g0)
    c: Horizontal(g0)
    c: Horizontal(g2)
    c: Vertical(g1)
    c: Vertical(g3)
    c: Distance(g1,g3) = 75
    c: Distance(g0,g2) = 30
    c: Coincident(g0,g-1)
    c: Coincident(g4,g5)
    c: Coincident(g5,g6)
    c: Coincident(g6,g7)
    c: Coincident(g7,g4)
    c: Horizontal(g4)
    c: Horizontal(g6)
    c: Vertical(g5)
    c: Vertical(g7)
    c: Distance(g5,g7) = 30
    c: Distance(g4,g6) = 75
    c: Coincident(g4,g0)
    c: Coincident(g8,g0)
    c: Coincident(g8,g1)
    c: Coincident(g9,g5)
    c: Coincident(g9,g6)
    c: Coincident(g10,g6)
    c: Coincident(g10,g0)
    c: Coincident(g11,g0)
    c: Coincident(g11,g0)
    c: Coincident(g12,g5)
    c: Coincident(g12,g1)
FEATURE [PartDesign::Pad] Pad
  Direction = (0,0,1)
  Length = 3
  Length2 = 10
  Profile = -> Sketch
  ReferenceAxis = -> Sketch [N_Axis]
  Refine = true
  Suppressed = false
  Type = 0
FEATURE [Sketcher::SketchObject] Sketch001
  ArcFitTolerance = 1e-06
  AttachmentSupport = -> [Pad]
  FullyConstrained = true
  MakeInternals = false
  MapMode = 5
  Placement = pos=(0,0,3) rot=(0,0,1;0rad)
  sketch-geometry (14):
    g0: LineSegment [constr] StartX=0 StartY=0 StartZ=0 EndX=19 EndY=0 EndZ=0
    g1: LineSegment [constr] StartX=19 StartY=0 StartZ=0 EndX=19 EndY=75 EndZ=0
    g2: LineSegment [constr] StartX=19 StartY=75 StartZ=0 EndX=0 EndY=75 EndZ=0
    g3: LineSegment [constr] StartX=0 StartY=75 StartZ=0 EndX=0 EndY=0 EndZ=0
    g4: LineSegment [constr] StartX=0 StartY=0 StartZ=0 EndX=75 EndY=0 EndZ=0
    g5: LineSegment [constr] StartX=75 StartY=0 StartZ=0 EndX=75 EndY=19 EndZ=0
    g6: LineSegment [constr] StartX=75 StartY=19 StartZ=0 EndX=0 EndY=19 EndZ=0
    g7: LineSegment [constr] StartX=0 StartY=19 StartZ=0 EndX=0 EndY=0 EndZ=0
    g8: LineSegment StartX=0 StartY=75 StartZ=0 EndX=19 EndY=75 EndZ=0
    g9: LineSegment StartX=19 StartY=75 StartZ=0 EndX=19 EndY=19 EndZ=0
    g10: LineSegment StartX=19 StartY=19 StartZ=0 EndX=75 EndY=19 EndZ=0
    g11: LineSegment StartX=75 StartY=19 StartZ=0 EndX=75 EndY=0 EndZ=0
    g12: LineSegment StartX=75 StartY=0 StartZ=0 EndX=0 EndY=0 EndZ=0
    g13: LineSegment StartX=0 StartY=0 StartZ=0 EndX=0 EndY=75 EndZ=0
  constraints (35):
    c: Coincident(g0,g1)
    c: Coincident(g1,g2)
    c: Coincident(g2,g3)
    c: Coincident(g3,g0)
    c: Horizontal(g0)
    c: Horizontal(g2)
    c: Vertical(g1)
    c: Vertical(g3)
    c: Distance(g1,g3) = 19
    c: Distance(g0,g2) = 75
    c: Coincident(g0,g-1)
    c: Coincident(g4,g5)
    c: Coincident(g5,g6)
    c: Coincident(g6,g7)
    c: Coincident(g7,g4)
    c: Horizontal(g4)
    c: Horizontal(g6)
    c: Vertical(g5)
    c: Vertical(g7)
    c: Distance(g5,g7) = 75
    c: Distance(g4,g6) = 19
    c: Coincident(g4,g0)
    c: Coincident(g8,g2)
    c: Coincident(g8,g1)
    c: Coincident(g9,g1)
    c: PointOnObject(g9,g6)
    c: Vertical(g9)
    c: Coincident(g10,g9)
    c: Coincident(g10,g5)
    c: Coincident(g11,g5)
    c: Coincident(g11,g4)
    c: Coincident(g12,g4)
    c: Coincident(g12,g0)
    c: Coincident(g13,g0)
    c: Coincident(g13,g2)
FEATURE [PartDesign::Pad] Pad001
  BaseFeature = -> Pad
  Direction = (0,0,1)
  Length = 3.2
  Length2 = 10
  Profile = -> Sketch001
  ReferenceAxis = -> Sketch001 [N_Axis]
  Refine = true
  Suppressed = false
  Type = 0
FEATURE [Sketcher::SketchObject] Sketch002
  ArcFitTolerance = 1e-06
  AttachmentSupport = -> [Pad001]
  FullyConstrained = true
  MakeInternals = false
  MapMode = 5
  Placement = pos=(0,0,0) rot=(1,0,0;3.14159rad)
  sketch-geometry (14):
    g0: LineSegment [constr] StartX=0 StartY=1e-16 StartZ=0 EndX=0 EndY=-30 EndZ=0
    g1: LineSegment [constr] StartX=0 StartY=-30 StartZ=0 EndX=30 EndY=-30 EndZ=0
    g2: LineSegment [constr] StartX=30 StartY=-30 StartZ=0 EndX=30 EndY=0 EndZ=0
    g3: LineSegment [constr] StartX=30 StartY=1e-16 StartZ=0 EndX=0 EndY=1e-16 EndZ=0
    g4: LineSegment [constr] StartX=30 StartY=1e-16 StartZ=0 EndX=30 EndY=-15 EndZ=0
    g5: LineSegment [constr] StartX=30 StartY=-15 StartZ=0 EndX=52.5 EndY=-15 EndZ=0
    g6: LineSegment [constr] StartX=52.5 StartY=-15 StartZ=0 EndX=52.5 EndY=0 EndZ=0
    g7: LineSegment [constr] StartX=52.5 StartY=1e-16 StartZ=0 EndX=30 EndY=1e-16 EndZ=0
    g8: Circle CenterX=52.5 CenterY=-15 CenterZ=0 NormalX=0 NormalY=0 NormalZ=1 AngleXU=0 Radius=2.7
    g9: LineSegment [constr] StartX=30 StartY=-30 StartZ=0 EndX=15 EndY=-30 EndZ=0
    g10: LineSegment [constr] StartX=15 StartY=-30 StartZ=0 EndX=15 EndY=-52.5 EndZ=0
    g11: LineSegment [constr] StartX=15 StartY=-52.5 StartZ=0 EndX=30 EndY=-52.5 EndZ=0
    g12: LineSegment [constr] StartX=30 StartY=-52.5 StartZ=0 EndX=30 EndY=-30 EndZ=0
    g13: Circle CenterX=15 CenterY=-52.5 CenterZ=0 NormalX=0 NormalY=0 NormalZ=1 AngleXU=0 Radius=2.7
  constraints (37):
    c: Coincident(g0,g1)
    c: Coincident(g1,g2)
    c: Coincident(g2,g3)
    c: Coincident(g3,g0)
    c: Vertical(g0)
    c: Vertical(g2)
    c: Horizontal(g1)
    c: Horizontal(g3)
    c: Distance(g0,g2) = 30
    c: Distance(g1,g3) = 30
    c: Coincident(g0,g-1)
    c: Coincident(g4,g5)
    c: Coincident(g5,g6)
    c: Coincident(g6,g7)
    c: Coincident(g7,g4)
    c: Vertical(g4)
    c: Vertical(g6)
    c: Horizontal(g5)
    c: Horizontal(g7)
    c: Distance(g4,g6) = 22.5
    c: Distance(g5,g7) = 15
    c: Coincident(g4,g2)
    c: Diameter(g8) = 5.4
    c: Coincident(g8,g5)
    c: Coincident(g9,g10)
    c: Coincident(g10,g11)
    c: Coincident(g11,g12)
    c: Coincident(g12,g9)
    c: Horizontal(g9)
    c: Horizontal(g11)
    c: Vertical(g10)
    c: Vertical(g12)
    c: Distance(g10,g12) = 15
    c: Distance(g9,g11) = 22.5
    c: Coincident(g9,g1)
    c: Diameter(g13) = 5.4
    c: Coincident(g13,g10)
FEATURE [PartDesign::Pocket] Pocket
  BaseFeature = -> Pad001
  Direction = (0,0,1)
  Length = 8
  Length2 = 5
  Profile = -> Sketch002
  ReferenceAxis = -> Sketch002 [N_Axis]
  Refine = true
  Suppressed = false
  Type = 0
FEATURE [PartDesign::Chamfer] Chamfer
  Angle = 45
  Base = -> Pocket [Edge16,Edge15]
  BaseFeature = -> Pocket
  ChamferType = 0
  FlipDirection = false
  Refine = true
  Size = 2
  Size2 = 1
  SupportTransform = false
  Suppressed = false
  UseAllEdges = false
FEATURE [PartDesign::Chamfer] Chamfer001
  Angle = 45
  Base = -> Chamfer [Edge16,Edge3]
  BaseFeature = -> Chamfer
  ChamferType = 0
  FlipDirection = false
  Refine = true
  Size = 6
  Size2 = 1
  SupportTransform = false
  Suppressed = false
  UseAllEdges = false
FEATURE [PartDesign::Body] Body  label="corner-plexi-mount-body"
  AllowCompound = false
  Group = -> [Sketch,Pad,Sketch001,Pad001,Sketch002,Pocket,Chamfer,Chamfer001]
  Origin = -> Origin001
  Tip = -> Chamfer001
FEATURE [App::Part] Part  label="corner-plexi-mount-part"
  Group = -> [Body]
  Origin = -> Origin
FEATURE [Sketcher::SketchObject] Sketch003
  ArcFitTolerance = 1e-06
  AttachmentSupport = -> [XY_Plane003]
  FullyConstrained = true
  MakeInternals = false
  MapMode = 5
  sketch-geometry (15):
    g0: LineSegment [constr] StartX=0 StartY=0 StartZ=0 EndX=75 EndY=0 EndZ=0
    g1: LineSegment [constr] StartX=75 StartY=0 StartZ=0 EndX=75 EndY=30 EndZ=0
    g2: LineSegment [constr] StartX=75 StartY=30 StartZ=0 EndX=0 EndY=30 EndZ=0
    g3: LineSegment [constr] StartX=0 StartY=30 StartZ=0 EndX=0 EndY=0 EndZ=0
    g4: LineSegment [constr] StartX=0 StartY=0 StartZ=0 EndX=30 EndY=0 EndZ=0
    g5: LineSegment [constr] StartX=30 StartY=0 StartZ=0 EndX=30 EndY=75 EndZ=0
    g6: LineSegment [constr] StartX=30 StartY=75 StartZ=0 EndX=0 EndY=75 EndZ=0
    g7: LineSegment [constr] StartX=0 StartY=75 StartZ=0 EndX=0 EndY=0 EndZ=0
    g8: LineSegment StartX=75 StartY=0 StartZ=0 EndX=75 EndY=30 EndZ=0
    g9: LineSegment StartX=0 StartY=0 StartZ=0 EndX=75 EndY=0 EndZ=0
    g10: LineSegment StartX=30 StartY=75 StartZ=0 EndX=75 EndY=30 EndZ=0
    g11: LineSegment StartX=0 StartY=0 StartZ=0 EndX=-45 EndY=0 EndZ=0
    g12: LineSegment StartX=-45 StartY=0 StartZ=0 EndX=-45 EndY=30 EndZ=0
    g13: LineSegment StartX=30 StartY=75 StartZ=0 EndX=0 EndY=75 EndZ=0
    g14: LineSegment StartX=0 StartY=75 StartZ=0 EndX=-45 EndY=30 EndZ=0
  constraints (38):
    c: Coincident(g0,g1)
    c: Coincident(g1,g2)
    c: Coincident(g2,g3)
    c: Coincident(g3,g0)
    c: Horizontal(g0)
    c: Horizontal(g2)
    c: Vertical(g1)
    c: Vertical(g3)
    c: Distance(g1,g3) = 75
    c: Distance(g0,g2) = 30
    c: Coincident(g0,g-1)
    c: Coincident(g4,g5)
    c: Coincident(g5,g6)
    c: Coincident(g6,g7)
    c: Coincident(g7,g4)
    c: Horizontal(g4)
    c: Horizontal(g6)
    c: Vertical(g5)
    c: Vertical(g7)
    c: Distance(g5,g7) = 30
    c: Distance(g4,g6) = 75
    c: Coincident(g4,g0)
    c: Coincident(g8,g0)
    c: Coincident(g8,g1)
    c: Coincident(g9,g0)
    c: Coincident(g9,g0)
    c: Coincident(g10,g5)
    c: Coincident(g10,g1)
    c: Distance(g11) = 45
    c: Coincident(g11,g0)
    c: PointOnObject(g11,g-1)
    c: Distance(g12) = 30
    c: Coincident(g12,g11)
    c: Vertical(g12)
    c: Coincident(g13,g5)
    c: Coincident(g13,g6)
    c: Coincident(g14,g6)
    c: Coincident(g14,g12)
FEATURE [PartDesign::Pad] Pad002
  Direction = (0,0,1)
  Length = 3
  Length2 = 10
  Profile = -> Sketch003
  ReferenceAxis = -> Sketch003 [N_Axis]
  Refine = true
  Suppressed = false
  Type = 0
FEATURE [Sketcher::SketchObject] Sketch004
  ArcFitTolerance = 1e-06
  AttachmentSupport = -> [Pad002]
  FullyConstrained = true
  MakeInternals = false
  MapMode = 5
  Placement = pos=(0,0,3) rot=(0,0,1;0rad)
  sketch-geometry (17):
    g0: LineSegment [constr] StartX=0 StartY=0 StartZ=0 EndX=19 EndY=0 EndZ=0
    g1: LineSegment [constr] StartX=19 StartY=0 StartZ=0 EndX=19 EndY=75 EndZ=0
    g2: LineSegment [constr] StartX=19 StartY=75 StartZ=0 EndX=0 EndY=75 EndZ=0
    g3: LineSegment [constr] StartX=0 StartY=75 StartZ=0 EndX=0 EndY=0 EndZ=0
    g4: LineSegment [constr] StartX=0 StartY=0 StartZ=0 EndX=75 EndY=0 EndZ=0
    g5: LineSegment [constr] StartX=75 StartY=0 StartZ=0 EndX=75 EndY=19 EndZ=0
    g6: LineSegment [constr] StartX=75 StartY=19 StartZ=0 EndX=0 EndY=19 EndZ=0
    g7: LineSegment [constr] StartX=0 StartY=19 StartZ=0 EndX=0 EndY=0 EndZ=0
    g8: LineSegment StartX=19 StartY=75 StartZ=0 EndX=19 EndY=19 EndZ=0
    g9: LineSegment StartX=19 StartY=19 StartZ=0 EndX=75 EndY=19 EndZ=0
    g10: LineSegment StartX=75 StartY=19 StartZ=0 EndX=75 EndY=0 EndZ=0
    g11: LineSegment StartX=75 StartY=0 StartZ=0 EndX=0 EndY=0 EndZ=0
    g12: LineSegment StartX=0 StartY=0 StartZ=0 EndX=-45 EndY=0 EndZ=0
    g13: LineSegment StartX=-45 StartY=0 StartZ=0 EndX=-45 EndY=19 EndZ=0
    g14: LineSegment StartX=-45 StartY=19 StartZ=0 EndX=11 EndY=19 EndZ=0
    g15: LineSegment StartX=11 StartY=19 StartZ=0 EndX=11 EndY=75 EndZ=0
    g16: LineSegment StartX=11 StartY=75 StartZ=0 EndX=19 EndY=75 EndZ=0
  constraints (45):
    c: Coincident(g0,g1)
    c: Coincident(g1,g2)
    c: Coincident(g2,g3)
    c: Coincident(g3,g0)
    c: Horizontal(g0)
    c: Horizontal(g2)
    c: Vertical(g1)
    c: Vertical(g3)
    c: Distance(g1,g3) = 19
    c: Distance(g0,g2) = 75
    c: Coincident(g0,g-1)
    c: Coincident(g4,g5)
    c: Coincident(g5,g6)
    c: Coincident(g6,g7)
    c: Coincident(g7,g4)
    c: Horizontal(g4)
    c: Horizontal(g6)
    c: Vertical(g5)
    c: Vertical(g7)
    c: Distance(g5,g7) = 75
    c: Distance(g4,g6) = 19
    c: Coincident(g4,g0)
    c: Coincident(g8,g1)
    c: PointOnObject(g8,g6)
    c: Vertical(g8)
    c: Coincident(g9,g8)
    c: Coincident(g9,g5)
    c: Coincident(g10,g5)
    c: Coincident(g10,g4)
    c: Coincident(g11,g4)
    c: Coincident(g11,g0)
    c: Distance(g12) = 45
    c: Coincident(g12,g0)
    c: PointOnObject(g12,g-1)
    c: Distance(g13) = 19
    c: Coincident(g13,g12)
    c: Vertical(g13)
    c: Distance(g14) = 56
    c: Coincident(g14,g13)
    c: PointOnObject(g14,g6)
    c: Coincident(g15,g14)
    c: PointOnObject(g15,g2)
    c: Vertical(g15)
    c: Coincident(g16,g15)
    c: Coincident(g16,g1)
FEATURE [PartDesign::Pad] Pad003
  BaseFeature = -> Pad002
  Direction = (0,0,1)
  Length = 3.2
  Length2 = 10
  Profile = -> Sketch004
  ReferenceAxis = -> Sketch004 [N_Axis]
  Refine = true
  Suppressed = false
  Type = 0
FEATURE [Sketcher::SketchObject] Sketch005
  ArcFitTolerance = 1e-06
  AttachmentSupport = -> [Pad003]
  FullyConstrained = true
  MakeInternals = false
  MapMode = 5
  Placement = pos=(0,0,0) rot=(1,0,0;3.14159rad)
  sketch-geometry (16):
    g0: LineSegment [constr] StartX=0 StartY=0 StartZ=0 EndX=0 EndY=-30 EndZ=0
    g1: LineSegment [constr] StartX=0 StartY=-30 StartZ=0 EndX=30 EndY=-30 EndZ=0
    g2: LineSegment [constr] StartX=30 StartY=-30 StartZ=0 EndX=30 EndY=0 EndZ=0
    g3: LineSegment [constr] StartX=30 StartY=0 StartZ=0 EndX=0 EndY=0 EndZ=0
    g4: LineSegment [constr] StartX=30 StartY=0 StartZ=0 EndX=30 EndY=-15 EndZ=0
    g5: LineSegment [constr] StartX=30 StartY=-15 StartZ=0 EndX=52.5 EndY=-15 EndZ=0
    g6: LineSegment [constr] StartX=52.5 StartY=-15 StartZ=0 EndX=52.5 EndY=0 EndZ=0
    g7: LineSegment [constr] StartX=52.5 StartY=0 StartZ=0 EndX=30 EndY=0 EndZ=0
    g8: Circle CenterX=52.5 CenterY=-15 CenterZ=0 NormalX=0 NormalY=0 NormalZ=1 AngleXU=0 Radius=2.7
    g9: LineSegment [constr] StartX=30 StartY=-30 StartZ=0 EndX=15 EndY=-30 EndZ=0
    g10: LineSegment [constr] StartX=15 StartY=-30 StartZ=0 EndX=15 EndY=-52.5 EndZ=0
    g11: LineSegment [constr] StartX=15 StartY=-52.5 StartZ=0 EndX=30 EndY=-52.5 EndZ=0
    g12: LineSegment [constr] StartX=30 StartY=-52.5 StartZ=0 EndX=30 EndY=-30 EndZ=0
    g13: Circle CenterX=15 CenterY=-52.5 CenterZ=0 NormalX=0 NormalY=0 NormalZ=1 AngleXU=0 Radius=2.7
    g14: LineSegment [constr] StartX=0 StartY=-15 StartZ=0 EndX=-22.5 EndY=-15 EndZ=0
    g15: Circle CenterX=-22.5 CenterY=-15 CenterZ=0 NormalX=0 NormalY=0 NormalZ=1 AngleXU=0 Radius=2.7
  constraints (42):
    c: Coincident(g0,g1)
    c: Coincident(g1,g2)
    c: Coincident(g2,g3)
    c: Coincident(g3,g0)
    c: Vertical(g0)
    c: Vertical(g2)
    c: Horizontal(g1)
    c: Horizontal(g3)
    c: Distance(g0,g2) = 30
    c: Distance(g1,g3) = 30
    c: Coincident(g0,g-1)
    c: Coincident(g4,g5)
    c: Coincident(g5,g6)
    c: Coincident(g6,g7)
    c: Coincident(g7,g4)
    c: Vertical(g4)
    c: Vertical(g6)
    c: Horizontal(g5)
    c: Horizontal(g7)
    c: Distance(g4,g6) = 22.5
    c: Distance(g5,g7) = 15
    c: Coincident(g4,g2)
    c: Diameter(g8) = 5.4
    c: Coincident(g8,g5)
    c: Coincident(g9,g10)
    c: Coincident(g10,g11)
    c: Coincident(g11,g12)
    c: Coincident(g12,g9)
    c: Horizontal(g9)
    c: Horizontal(g11)
    c: Vertical(g10)
    c: Vertical(g12)
    c: Distance(g10,g12) = 15
    c: Distance(g9,g11) = 22.5
    c: Coincident(g9,g1)
    c: Diameter(g13) = 5.4
    c: Coincident(g13,g10)
    c: Distance(g14) = 22.5
    c: Symmetric(g0,g0,g14)
    c: Horizontal(g14)
    c: Diameter(g15) = 5.4
    c: Coincident(g15,g14)
FEATURE [PartDesign::Pocket] Pocket001
  BaseFeature = -> Pad003
  Direction = (0,0,1)
  Length = 8
  Length2 = 5
  Profile = -> Sketch005
  ReferenceAxis = -> Sketch005 [N_Axis]
  Refine = true
  Suppressed = false
  Type = 0
FEATURE [PartDesign::Chamfer] Chamfer002
  Angle = 45
  Base = -> Pocket001 [Edge17]
  BaseFeature = -> Pocket001
  ChamferType = 0
  FlipDirection = false
  Refine = true
  Size = 2
  Size2 = 1
  SupportTransform = false
  Suppressed = false
  UseAllEdges = false
FEATURE [PartDesign::Chamfer] Chamfer003
  Angle = 45
  Base = -> Chamfer002 [Edge38,Edge36,Edge18,Edge3]
  BaseFeature = -> Chamfer002
  ChamferType = 0
  FlipDirection = false
  Refine = true
  Size = 6
  Size2 = 1
  SupportTransform = false
  Suppressed = false
  UseAllEdges = false
FEATURE [PartDesign::Body] Body001  label="plexi-mount-part001"
  AllowCompound = false
  Group = -> [Sketch003,Pad002,Sketch004,Pad003,Sketch005,Pocket001,Chamfer002,Chamfer003]
  Origin = -> Origin003
  Tip = -> Chamfer003
FEATURE [App::Part] Part001  label="middle-plexi-mount-part"
  Group = -> [Body001]
  Origin = -> Origin002
---- part panels/plexi.FCStd = doc fcstd_3cd9277dd022 ----
FCSTD DOCUMENT  (FreeCAD 1.0R39285 (Git))
Label: plexi
License: All rights reserved
objects: Sketcher::SketchObject×11, PartDesign::Pad×10, PartDesign::Body×10, App::Part×10, PartDesign::Pocket×1
note: 65 computed .brp shape members not serialized (recipe doc carries the construction recipe); baked Part::Feature solids carry a one-line shape summary decoded from their .brp

FEATURE [Sketcher::SketchObject] Sketch
  ArcFitTolerance = 1e-06
  AttachmentSupport = -> [XY_Plane]
  FullyConstrained = true
  MakeInternals = false
  MapMode = 5
  sketch-geometry (5):
    g0: LineSegment StartX=-106 StartY=-236 StartZ=0 EndX=106 EndY=-236 EndZ=0
    g1: LineSegment StartX=106 StartY=-236 StartZ=0 EndX=106 EndY=236 EndZ=0
    g2: LineSegment StartX=106 StartY=236 StartZ=0 EndX=-106 EndY=236 EndZ=0
    g3: LineSegment StartX=-106 StartY=236 StartZ=0 EndX=-106 EndY=-236 EndZ=0
    g4: GeomPoint [constr] X=-1.3e-15 Y=1e-16 Z=0
  constraints (12):
    c: Coincident(g0,g1)
    c: Coincident(g1,g2)
    c: Coincident(g2,g3)
    c: Coincident(g3,g0)
    c: Horizontal(g0)
    c: Horizontal(g2)
    c: Vertical(g1)
    c: Vertical(g3)
    c: Symmetric(g2,g0,g4)
    c: Distance(g1,g3) = 212
    c: Distance(g0,g2) = 472
    c: Coincident(g4,g-1)
FEATURE [Sketcher::SketchObject] Sketch002
  ArcFitTolerance = 1e-06
  AttachmentSupport = -> [XY_Plane005]
  FullyConstrained = false
  MakeInternals = false
  MapMode = 5
  sketch-geometry (5):
    g0: LineSegment StartX=-235.6 StartY=-235.6 StartZ=0 EndX=235.6 EndY=-235.6 EndZ=0
    g1: LineSegment StartX=235.6 StartY=-235.6 StartZ=0 EndX=235.6 EndY=235.6 EndZ=0
    g2: LineSegment StartX=235.6 StartY=235.6 StartZ=0 EndX=-235.6 EndY=235.6 EndZ=0
    g3: LineSegment StartX=-235.6 StartY=235.6 StartZ=0 EndX=-235.6 EndY=-235.6 EndZ=0
    g4: GeomPoint [constr] X=0 Y=0 Z=0
  constraints (11):
    c: Coincident(g0,g1)
    c: Coincident(g1,g2)
    c: Coincident(g2,g3)
    c: Coincident(g3,g0)
    c: Horizontal(g0)
    c: Horizontal(g2)
    c: Vertical(g1)
    c: Vertical(g3)
    c: Symmetric(g2,g0,g4)
    c: Distance(g1,g3) = 471.2
    c: Distance(g0,g2) = 471.2
FEATURE [PartDesign::Pad] Pad002
  Direction = (0,0,1)
  Length = 3
  Length2 = 10
  Profile = -> Sketch002
  ReferenceAxis = -> Sketch002 [N_Axis]
  Refine = true
  Suppressed = false
  Type = 0
FEATURE [PartDesign::Body] Body002  label="plexi-front-471.2x471.2-body"
  AllowCompound = false
  Group = -> [Sketch002,Pad002]
  Origin = -> Origin005
  Tip = -> Pad002
FEATURE [App::Part] Part002  label="plexi-front-471.2x471.2-part"
  Group = -> [Body002]
  Origin = -> Origin004
FEATURE [Sketcher::SketchObject] Sketch004
  ArcFitTolerance = 1e-06
  AttachmentSupport = -> [XY_Plane009]
  FullyConstrained = true
  MakeInternals = false
  MapMode = 5
  sketch-geometry (5):
    g0: LineSegment StartX=-145.6 StartY=-235.6 StartZ=0 EndX=145.6 EndY=-235.6 EndZ=0
    g1: LineSegment StartX=145.6 StartY=-235.6 StartZ=0 EndX=145.6 EndY=235.6 EndZ=0
    g2: LineSegment StartX=145.6 StartY=235.6 StartZ=0 EndX=-145.6 EndY=235.6 EndZ=0
    g3: LineSegment StartX=-145.6 StartY=235.6 StartZ=0 EndX=-145.6 EndY=-235.6 EndZ=0
    g4: GeomPoint [constr] X=0 Y=0 Z=0
  constraints (12):
    c: Coincident(g0,g1)
    c: Coincident(g1,g2)
    c: Coincident(g2,g3)
    c: Coincident(g3,g0)
    c: Horizontal(g0)
    c: Horizontal(g2)
    c: Vertical(g1)
    c: Vertical(g3)
    c: Symmetric(g2,g0,g4)
    c: Distance(g1,g3) = 291.2
    c: Distance(g0,g2) = 471.2
    c: Coincident(g4,g-1)
FEATURE [Sketcher::SketchObject] Sketch001
  ArcFitTolerance = 1e-06
  AttachmentSupport = -> [XY_Plane003]
  FullyConstrained = true
  MakeInternals = false
  MapMode = 5
  sketch-geometry (38):
    g0: LineSegment [constr] StartX=-275 StartY=-255 StartZ=0 EndX=275 EndY=-255 EndZ=0
    g1: LineSegment [constr] StartX=275 StartY=-255 StartZ=0 EndX=275 EndY=255 EndZ=0
    g2: LineSegment [constr] StartX=275 StartY=255 StartZ=0 EndX=-275 EndY=255 EndZ=0
    g3: LineSegment [constr] StartX=-275 StartY=255 StartZ=0 EndX=-275 EndY=-255 EndZ=0
    g4: GeomPoint [constr] X=0 Y=0 Z=0
    g5: LineSegment [constr] StartX=-255.6 StartY=-235.6 StartZ=0 EndX=255.6 EndY=-235.6 EndZ=0
    g6: LineSegment [constr] StartX=255.6 StartY=-235.6 StartZ=0 EndX=255.6 EndY=235.6 EndZ=0
    g7: LineSegment [constr] StartX=255.6 StartY=235.6 StartZ=0 EndX=-255.6 EndY=235.6 EndZ=0
    g8: LineSegment [constr] StartX=-255.6 StartY=235.6 StartZ=0 EndX=-255.6 EndY=-235.6 EndZ=0
    g9: GeomPoint [constr] X=0 Y=0 Z=0
    g10: LineSegment [constr] StartX=-275 StartY=255 StartZ=0 EndX=-275 EndY=225 EndZ=0
    g11: LineSegment [constr] StartX=-275 StartY=225 StartZ=0 EndX=-245 EndY=225 EndZ=0
    g12: LineSegment [constr] StartX=-245 StartY=225 StartZ=0 EndX=-245 EndY=255 EndZ=0
    g13: LineSegment [constr] StartX=-245 StartY=255 StartZ=0 EndX=-275 EndY=255 EndZ=0
    g14: LineSegment [constr] StartX=275 StartY=255 StartZ=0 EndX=245 EndY=255 EndZ=0
    g15: LineSegment [constr] StartX=245 StartY=255 StartZ=0 EndX=245 EndY=225 EndZ=0
    g16: LineSegment [constr] StartX=245 StartY=225 StartZ=0 EndX=275 EndY=225 EndZ=0
    g17: LineSegment [constr] StartX=275 StartY=225 StartZ=0 EndX=275 EndY=255 EndZ=0
    g18: LineSegment [constr] StartX=275 StartY=-255 StartZ=0 EndX=275 EndY=-225 EndZ=0
    g19: LineSegment [constr] StartX=275 StartY=-225 StartZ=0 EndX=245 EndY=-225 EndZ=0
    g20: LineSegment [constr] StartX=245 StartY=-225 StartZ=0 EndX=245 EndY=-255 EndZ=0
    g21: LineSegment [constr] StartX=245 StartY=-255 StartZ=0 EndX=275 EndY=-255 EndZ=0
    g22: LineSegment [constr] StartX=-275 StartY=-255 StartZ=0 EndX=-245 EndY=-255 EndZ=0
    g23: LineSegment [constr] StartX=-245 StartY=-255 StartZ=0 EndX=-245 EndY=-225 EndZ=0
    g24: LineSegment [constr] StartX=-245 StartY=-225 StartZ=0 EndX=-275 EndY=-225 EndZ=0
    g25: LineSegment [constr] StartX=-275 StartY=-225 StartZ=0 EndX=-275 EndY=-255 EndZ=0
    g26: LineSegment StartX=-245 StartY=225 StartZ=0 EndX=-255.6 EndY=225 EndZ=0
    g27: LineSegment StartX=-255.6 StartY=225 StartZ=0 EndX=-255.6 EndY=-225 EndZ=0
    g28: LineSegment StartX=-255.6 StartY=-225 StartZ=0 EndX=-245 EndY=-225 EndZ=0
    g29: LineSegment StartX=-245 StartY=-225 StartZ=0 EndX=-245 EndY=-235.6 EndZ=0
    g30: LineSegment StartX=-245 StartY=-235.6 StartZ=0 EndX=245 EndY=-235.6 EndZ=0
    g31: LineSegment StartX=245 StartY=-235.6 StartZ=0 EndX=245 EndY=-225 EndZ=0
    g32: LineSegment StartX=245 StartY=-225 StartZ=0 EndX=255.6 EndY=-225 EndZ=0
    g33: LineSegment StartX=255.6 StartY=-225 StartZ=0 EndX=255.6 EndY=225 EndZ=0
    g34: LineSegment StartX=255.6 StartY=225 StartZ=0 EndX=245 EndY=225 EndZ=0
    g35: LineSegment StartX=245 StartY=225 StartZ=0 EndX=245 EndY=235.6 EndZ=0
    g36: LineSegment StartX=245 StartY=235.6 StartZ=0 EndX=-245 EndY=235.6 EndZ=0
    g37: LineSegment StartX=-245 StartY=235.6 StartZ=0 EndX=-245 EndY=225 EndZ=0
  constraints (100):
    c: Coincident(g0,g1)
    c: Coincident(g1,g2)
    c: Coincident(g2,g3)
    c: Coincident(g3,g0)
    c: Horizontal(g0)
    c: Horizontal(g2)
    c: Vertical(g1)
    c: Vertical(g3)
    c: Symmetric(g2,g0,g4)
    c: Distance(g1,g3) = 550
    c: Distance(g0,g2) = 510
    c: Coincident(g4,g-1)
    c: Coincident(g5,g6)
    c: Coincident(g6,g7)
    c: Coincident(g7,g8)
    c: Coincident(g8,g5)
    c: Horizontal(g5)
    c: Horizontal(g7)
    c: Vertical(g6)
    c: Vertical(g8)
    c: Symmetric(g7,g5,g9)
    c: Distance(g6,g8) = 511.2
    c: Distance(g5,g7) = 471.2
    c: Coincident(g9,g4)
    c: Coincident(g10,g11)
    c: Coincident(g11,g12)
    c: Coincident(g12,g13)
    c: Coincident(g13,g10)
    c: Vertical(g10)
    c: Vertical(g12)
    c: Horizontal(g11)
    c: Horizontal(g13)
    c: Distance(g10,g12) = 30
    c: Distance(g11,g13) = 30
    c: Coincident(g10,g2)
    c: Coincident(g14,g15)
    c: Coincident(g15,g16)
    c: Coincident(g16,g17)
    c: Coincident(g17,g14)
    c: Horizontal(g14)
    c: Horizontal(g16)
    c: Vertical(g15)
    c: Vertical(g17)
    c: Distance(g15,g17) = 30
    c: Distance(g14,g16) = 30
    c: Coincident(g14,g1)
    c: Coincident(g18,g19)
    c: Coincident(g19,g20)
    c: Coincident(g20,g21)
    c: Coincident(g21,g18)
    c: Vertical(g18)
    c: Vertical(g20)
    c: Horizontal(g19)
    c: Horizontal(g21)
    c: Distance(g18,g20) = 30
    c: Distance(g19,g21) = 30
    c: Coincident(g18,g0)
    c: Coincident(g22,g23)
    c: Coincident(g23,g24)
    c: Coincident(g24,g25)
    c: Coincident(g25,g22)
    c: Horizontal(g22)
    c: Horizontal(g24)
    c: Vertical(g23)
    c: Vertical(g25)
    c: Distance(g23,g25) = 30
    c: Distance(g22,g24) = 30
    c: Coincident(g22,g0)
    c: Coincident(g26,g11)
    c: PointOnObject(g26,g8)
    c: Horizontal(g26)
    c: Coincident(g27,g26)
    c: PointOnObject(g27,g24)
    c: Vertical(g27)
    c: Coincident(g28,g27)
    c: Coincident(g28,g23)
    c: Coincident(g29,g23)
    c: PointOnObject(g29,g5)
    c: Vertical(g29)
    c: Distance(g30) = 490
    c: Coincident(g30,g29)
    c: PointOnObject(g30,g5)
    c: Coincident(g31,g30)
    c: Coincident(g31,g19)
    c: Distance(g32) = 10.6
    c: Coincident(g32,g19)
    c: PointOnObject(g32,g19)
    c: Distance(g33) = 450
    c: Coincident(g33,g32)
    c: PointOnObject(g33,g6)
    c: Coincident(g34,g33)
    c: Coincident(g34,g15)
    c: Distance(g35) = 10.6
    c: Coincident(g35,g15)
    c: PointOnObject(g35,g15)
    c: Distance(g36) = 490
    c: Coincident(g36,g35)
    c: PointOnObject(g36,g7)
    c: Coincident(g37,g36)
    c: Coincident(g37,g11)
FEATURE [PartDesign::Pad] Pad001
  Direction = (0,0,1)
  Length = 3
  Length2 = 10
  Profile = -> Sketch001
  ReferenceAxis = -> Sketch001 [N_Axis]
  Refine = true
  Suppressed = false
  Type = 0
FEATURE [PartDesign::Body] Body001  label="plexi-bottom-511.2x471.2-body"
  AllowCompound = false
  Group = -> [Sketch001,Pad001]
  Origin = -> Origin003
  Tip = -> Pad001
FEATURE [App::Part] Part001  label="plexi-bottom-511.2x471.2-part"
  Group = -> [Body001]
  Origin = -> Origin002
FEATURE [Sketcher::SketchObject] Sketch003
  ArcFitTolerance = 1e-06
  AttachmentSupport = -> [XY_Plane007]
  FullyConstrained = true
  MakeInternals = false
  MapMode = 5
  sketch-geometry (5):
    g0: LineSegment StartX=-105.6 StartY=-235.6 StartZ=0 EndX=105.6 EndY=-235.6 EndZ=0
    g1: LineSegment StartX=105.6 StartY=-235.6 StartZ=0 EndX=105.6 EndY=235.6 EndZ=0
    g2: LineSegment StartX=105.6 StartY=235.6 StartZ=0 EndX=-105.6 EndY=235.6 EndZ=0
    g3: LineSegment StartX=-105.6 StartY=235.6 StartZ=0 EndX=-105.6 EndY=-235.6 EndZ=0
    g4: GeomPoint [constr] X=0 Y=0 Z=0
  constraints (12):
    c: Coincident(g0,g1)
    c: Coincident(g1,g2)
    c: Coincident(g2,g3)
    c: Coincident(g3,g0)
    c: Horizontal(g0)
    c: Horizontal(g2)
    c: Vertical(g1)
    c: Vertical(g3)
    c: Symmetric(g2,g0,g4)
    c: Distance(g1,g3) = 211.2
    c: Distance(g0,g2) = 471.2
    c: Coincident(g4,g-1)
FEATURE [PartDesign::Pad] Pad003
  Direction = (0,0,1)
  Length = 3
  Length2 = 10
  Profile = -> Sketch003
  ReferenceAxis = -> Sketch003 [N_Axis]
  Refine = true
  Suppressed = false
  Type = 0
FEATURE [PartDesign::Body] Body003  label="plexi-top-471.2x211.2-body"
  AllowCompound = false
  Group = -> [Sketch003,Pad003]
  Origin = -> Origin007
  Tip = -> Pad003
FEATURE [App::Part] Part003  label="plexi-top-471.2x211.2-part"
  Group = -> [Body003]
  Origin = -> Origin006
FEATURE [PartDesign::Pad] Pad
  Direction = (0,0,1)
  Length = 3
  Length2 = 10
  Profile = -> Sketch
  ReferenceAxis = -> Sketch [N_Axis]
  Refine = true
  Suppressed = false
  Type = 0
FEATURE [PartDesign::Body] Body  label="plexi-472x212-body"
  AllowCompound = false
  Group = -> [Sketch,Pad]
  Origin = -> Origin
  Tip = -> Pad
FEATURE [App::Part] Part  label="plexi-472x212-part"
  Group = -> [Body]
  Origin = -> Origin001
FEATURE [PartDesign::Pad] Pad004
  Direction = (0,0,1)
  Length = 3
  Length2 = 10
  Profile = -> Sketch004
  ReferenceAxis = -> Sketch004 [N_Axis]
  Refine = true
  Suppressed = false
  Type = 0
FEATURE [PartDesign::Body] Body004  label="plexi-top-471.2x291.2-body"
  AllowCompound = false
  Group = -> [Sketch004,Pad004]
  Origin = -> Origin009
  Tip = -> Pad004
FEATURE [App::Part] Part004  label="plexi-top-471.2x291.2-part"
  Group = -> [Body004]
  Origin = -> Origin008
FEATURE [Sketcher::SketchObject] Sketch005
  ArcFitTolerance = 1e-06
  AttachmentSupport = -> [XY_Plane011]
  FullyConstrained = true
  MakeInternals = false
  MapMode = 5
  sketch-geometry (26):
    g0: LineSegment [constr] StartX=-255 StartY=-255 StartZ=0 EndX=255 EndY=-255 EndZ=0
    g1: LineSegment [constr] StartX=255 StartY=-255 StartZ=0 EndX=255 EndY=255 EndZ=0
    g2: LineSegment [constr] StartX=255 StartY=255 StartZ=0 EndX=-255 EndY=255 EndZ=0
    g3: LineSegment [constr] StartX=-255 StartY=255 StartZ=0 EndX=-255 EndY=-255 EndZ=0
    g4: GeomPoint [constr] X=0 Y=0 Z=0
    g5: LineSegment [constr] StartX=-235.5 StartY=-235.5 StartZ=0 EndX=235.5 EndY=-235.5 EndZ=0
    g6: LineSegment [constr] StartX=235.5 StartY=-235.5 StartZ=0 EndX=235.5 EndY=235.5 EndZ=0
    g7: LineSegment [constr] StartX=235.5 StartY=235.5 StartZ=0 EndX=-235.5 EndY=235.5 EndZ=0
    g8: LineSegment [constr] StartX=-235.5 StartY=235.5 StartZ=0 EndX=-235.5 EndY=-235.5 EndZ=0
    g9: GeomPoint [constr] X=0 Y=0 Z=0
    g10: LineSegment [constr] StartX=-235.5 StartY=-235.5 StartZ=0 EndX=-225 EndY=-235.5 EndZ=0
    g11: LineSegment [constr] StartX=-225 StartY=-235.5 StartZ=0 EndX=-225 EndY=-225 EndZ=0
    g12: LineSegment [constr] StartX=-225 StartY=-225 StartZ=0 EndX=-235.5 EndY=-225 EndZ=0
    g13: LineSegment [constr] StartX=-235.5 StartY=-225 StartZ=0 EndX=-235.5 EndY=-235.5 EndZ=0
    g14: LineSegment [constr] StartX=235.5 StartY=-235.5 StartZ=0 EndX=235.5 EndY=-225 EndZ=0
    g15: LineSegment [constr] StartX=235.5 StartY=-225 StartZ=0 EndX=225 EndY=-225 EndZ=0
    g16: LineSegment [constr] StartX=225 StartY=-225 StartZ=0 EndX=225 EndY=-235.5 EndZ=0
    g17: LineSegment [constr] StartX=225 StartY=-235.5 StartZ=0 EndX=235.5 EndY=-235.5 EndZ=0
    g18: LineSegment StartX=225 StartY=-225 StartZ=0 EndX=235.5 EndY=-225 EndZ=0
    g19: LineSegment StartX=235.5 StartY=-225 StartZ=0 EndX=235.5 EndY=235.5 EndZ=0
    g20: LineSegment StartX=235.5 StartY=235.5 StartZ=0 EndX=-235.5 EndY=235.5 EndZ=0
    g21: LineSegment StartX=-235.5 StartY=235.5 StartZ=0 EndX=-235.5 EndY=-225 EndZ=0
    g22: LineSegment StartX=-235.5 StartY=-225 StartZ=0 EndX=-225 EndY=-225 EndZ=0
    g23: LineSegment StartX=-225 StartY=-225 StartZ=0 EndX=-225 EndY=-235.5 EndZ=0
    g24: LineSegment StartX=-225 StartY=-235.5 StartZ=0 EndX=225 EndY=-235.5 EndZ=0
    g25: LineSegment StartX=225 StartY=-235.5 StartZ=0 EndX=225 EndY=-225 EndZ=0
  constraints (62):
    c: Coincident(g0,g1)
    c: Coincident(g1,g2)
    c: Coincident(g2,g3)
    c: Coincident(g3,g0)
    c: Horizontal(g0)
    c: Horizontal(g2)
    c: Vertical(g1)
    c: Vertical(g3)
    c: Symmetric(g2,g0,g4)
    c: Distance(g1,g3) = 510
    c: Distance(g0,g2) = 510
    c: Coincident(g4,g-1)
    c: Coincident(g5,g6)
    c: Coincident(g6,g7)
    c: Coincident(g7,g8)
    c: Coincident(g8,g5)
    c: Horizontal(g5)
    c: Horizontal(g7)
    c: Vertical(g6)
    c: Vertical(g8)
    c: Symmetric(g7,g5,g9)
    c: Distance(g6,g8) = 471
    c: Distance(g5,g7) = 471
    c: Coincident(g9,g4)
    c: Coincident(g10,g11)
    c: Coincident(g11,g12)
    c: Coincident(g12,g13)
    c: Coincident(g13,g10)
    c: Horizontal(g10)
    c: Horizontal(g12)
    c: Vertical(g11)
    c: Vertical(g13)
    c: Distance(g11,g13) = 10.5
    c: Distance(g10,g12) = 10.5
    c: Coincident(g10,g5)
    c: Coincident(g14,g15)
    c: Coincident(g15,g16)
    c: Coincident(g16,g17)
    c: Coincident(g17,g14)
    c: Vertical(g14)
    c: Vertical(g16)
    c: Horizontal(g15)
    c: Horizontal(g17)
    c: Distance(g14,g16) = 10.5
    c: Distance(g15,g17) = 10.5
    c: Coincident(g14,g5)
    c: Coincident(g18,g15)
    c: Coincident(g18,g14)
    c: Coincident(g19,g14)
    c: Coincident(g19,g6)
    c: Coincident(g20,g6)
    c: Coincident(g20,g7)
    c: Coincident(g21,g7)
    c: Coincident(g21,g12)
    c: Coincident(g22,g12)
    c: Coincident(g22,g11)
    c: Coincident(g23,g11)
    c: Coincident(g23,g10)
    c: Coincident(g24,g10)
    c: Coincident(g24,g16)
    c: Coincident(g25,g16)
    c: Coincident(g25,g15)
FEATURE [PartDesign::Pad] Pad005
  Direction = (0,0,1)
  Length = 3
  Length2 = 10
  Profile = -> Sketch005
  ReferenceAxis = -> Sketch005 [N_Axis]
  Refine = true
  Suppressed = false
  Type = 0
FEATURE [Sketcher::SketchObject] Sketch006
  ArcFitTolerance = 1e-06
  AttachmentSupport = -> [Pad005]
  FullyConstrained = true
  MakeInternals = false
  MapMode = 5
  Placement = pos=(0,0,3) rot=(0,0,1;0rad)
  sketch-geometry (29):
    g0: LineSegment [constr] StartX=-255 StartY=-255 StartZ=0 EndX=255 EndY=-255 EndZ=0
    g1: LineSegment [constr] StartX=255 StartY=-255 StartZ=0 EndX=255 EndY=255 EndZ=0
    g2: LineSegment [constr] StartX=255 StartY=255 StartZ=0 EndX=-255 EndY=255 EndZ=0
    g3: LineSegment [constr] StartX=-255 StartY=255 StartZ=0 EndX=-255 EndY=-255 EndZ=0
    g4: GeomPoint [constr] X=0 Y=0 Z=0
    g5: LineSegment [constr] StartX=-255 StartY=-255 StartZ=0 EndX=-225 EndY=-255 EndZ=0
    g6: LineSegment [constr] StartX=-225 StartY=-255 StartZ=0 EndX=-225 EndY=-21 EndZ=0
    g7: LineSegment [constr] StartX=-225 StartY=-21 StartZ=0 EndX=-255 EndY=-21 EndZ=0
    g8: LineSegment [constr] StartX=-255 StartY=-21 StartZ=0 EndX=-255 EndY=-255 EndZ=0
    g9: LineSegment [constr] StartX=255 StartY=-255 StartZ=0 EndX=255 EndY=-21 EndZ=0
    g10: LineSegment [constr] StartX=255 StartY=-21 StartZ=0 EndX=225 EndY=-21 EndZ=0
    g11: LineSegment [constr] StartX=225 StartY=-21 StartZ=0 EndX=225 EndY=-255 EndZ=0
    g12: LineSegment [constr] StartX=225 StartY=-255 StartZ=0 EndX=255 EndY=-255 EndZ=0
    g13: LineSegment StartX=225 StartY=-21 StartZ=0 EndX=255 EndY=-21 EndZ=0
    g14: LineSegment StartX=255 StartY=-21 StartZ=0 EndX=255 EndY=45 EndZ=0
    g15: LineSegment StartX=255 StartY=45 StartZ=0 EndX=225 EndY=45 EndZ=0
    g16: LineSegment StartX=225 StartY=45 StartZ=0 EndX=225 EndY=-21 EndZ=0
    g17: LineSegment StartX=-255 StartY=-21 StartZ=0 EndX=-225 EndY=-21 EndZ=0
    g18: LineSegment StartX=-225 StartY=-21 StartZ=0 EndX=-225 EndY=45 EndZ=0
    g19: LineSegment StartX=-225 StartY=45 StartZ=0 EndX=-255 EndY=45 EndZ=0
    g20: LineSegment StartX=-255 StartY=45 StartZ=0 EndX=-255 EndY=-21 EndZ=0
    g21: LineSegment StartX=-255 StartY=-255 StartZ=0 EndX=-225 EndY=-255 EndZ=0
    g22: LineSegment StartX=-225 StartY=-255 StartZ=0 EndX=-225 EndY=-189 EndZ=0
    g23: LineSegment StartX=-225 StartY=-189 StartZ=0 EndX=-255 EndY=-189 EndZ=0
    g24: LineSegment StartX=-255 StartY=-189 StartZ=0 EndX=-255 EndY=-255 EndZ=0
    g25: LineSegment StartX=255 StartY=-255 StartZ=0 EndX=255 EndY=-189 EndZ=0
    g26: LineSegment StartX=255 StartY=-189 StartZ=0 EndX=225 EndY=-189 EndZ=0
    g27: LineSegment StartX=225 StartY=-189 StartZ=0 EndX=225 EndY=-255 EndZ=0
    g28: LineSegment StartX=225 StartY=-255 StartZ=0 EndX=255 EndY=-255 EndZ=0
  constraints (78):
    c: Coincident(g0,g1)
    c: Coincident(g1,g2)
    c: Coincident(g2,g3)
    c: Coincident(g3,g0)
    c: Horizontal(g0)
    c: Horizontal(g2)
    c: Vertical(g1)
    c: Vertical(g3)
    c: Symmetric(g2,g0,g4)
    c: Distance(g1,g3) = 510
    c: Distance(g0,g2) = 510
    c: Coincident(g4,g-1)
    c: Coincident(g5,g6)
    c: Coincident(g6,g7)
    c: Coincident(g7,g8)
    c: Coincident(g8,g5)
    c: Horizontal(g5)
    c: Horizontal(g7)
    c: Vertical(g6)
    c: Vertical(g8)
    c: Distance(g6,g8) = 30
    c: Distance(g5,g7) = 234
    c: Coincident(g5,g0)
    c: Coincident(g9,g10)
    c: Coincident(g10,g11)
    c: Coincident(g11,g12)
    c: Coincident(g12,g9)
    c: Vertical(g9)
    c: Vertical(g11)
    c: Horizontal(g10)
    c: Horizontal(g12)
    c: Distance(g9,g11) = 30
    c: Distance(g10,g12) = 234
    c: Coincident(g9,g0)
    c: Coincident(g13,g14)
    c: Coincident(g14,g15)
    c: Coincident(g15,g16)
    c: Coincident(g16,g13)
    c: Horizontal(g13)
    c: Horizontal(g15)
    c: Vertical(g14)
    c: Vertical(g16)
    c: Distance(g13,g15) = 66
    c: Coincident(g13,g10)
    c: PointOnObject(g14,g1)
    c: Coincident(g17,g18)
    c: Coincident(g18,g19)
    c: Coincident(g19,g20)
    c: Coincident(g20,g17)
    c: Horizontal(g17)
    c: Horizontal(g19)
    c: Vertical(g18)
    c: Vertical(g20)
    c: Distance(g18,g20) = 30
    c: Distance(g17,g19) = 66
    c: Coincident(g17,g7)
    c: Coincident(g21,g22)
    c: Coincident(g22,g23)
    c: Coincident(g23,g24)
    c: Coincident(g24,g21)
    c: Horizontal(g21)
    c: Horizontal(g23)
    c: Vertical(g22)
    c: Vertical(g24)
    c: Distance(g21,g23) = 66
    c: Coincident(g21,g0)
    c: PointOnObject(g22,g6)
    c: Coincident(g25,g26)
    c: Coincident(g26,g27)
    c: Coincident(g27,g28)
    c: Coincident(g28,g25)
    c: Vertical(g25)
    c: Vertical(g27)
    c: Horizontal(g26)
    c: Horizontal(g28)
    c: Distance(g26,g28) = 66
    c: Coincident(g25,g0)
    c: PointOnObject(g26,g11)
FEATURE [PartDesign::Pocket] Pocket
  BaseFeature = -> Pad005
  Direction = (0,0,-1)
  Length = 5
  Length2 = 5
  Profile = -> Sketch006
  ReferenceAxis = -> Sketch006 [N_Axis]
  Refine = true
  Suppressed = false
  Type = 0
FEATURE [PartDesign::Body] Body005  label="plexi-back-471x471-body"
  AllowCompound = false
  Group = -> [Sketch005,Pad005,Sketch006,Pocket]
  Origin = -> Origin011
  Tip = -> Pocket
FEATURE [App::Part] Part005  label="plexi-back-471x471-part"
  Group = -> [Body005]
  Origin = -> Origin010
FEATURE [Sketcher::SketchObject] Sketch007
  ArcFitTolerance = 1e-06
  AttachmentSupport = -> [XY_Plane013]
  FullyConstrained = true
  MakeInternals = false
  MapMode = 5
  sketch-geometry (5):
    g0: LineSegment StartX=-130.5 StartY=-105.3 StartZ=0 EndX=130.5 EndY=-105.3 EndZ=0
    g1: LineSegment StartX=130.5 StartY=-105.3 StartZ=0 EndX=130.5 EndY=105.3 EndZ=0
    g2: LineSegment StartX=130.5 StartY=105.3 StartZ=0 EndX=-130.5 EndY=105.3 EndZ=0
    g3: LineSegment StartX=-130.5 StartY=105.3 StartZ=0 EndX=-130.5 EndY=-105.3 EndZ=0
    g4: GeomPoint [constr] X=0 Y=0 Z=0
  constraints (12):
    c: Coincident(g0,g1)
    c: Coincident(g1,g2)
    c: Coincident(g2,g3)
    c: Coincident(g3,g0)
    c: Horizontal(g0)
    c: Horizontal(g2)
    c: Vertical(g1)
    c: Vertical(g3)
    c: Symmetric(g2,g0,g4)
    c: Distance(g1,g3) = 261
    c: Distance(g0,g2) = 210.6
    c: Coincident(g4,g-1)
FEATURE [PartDesign::Pad] Pad006
  Direction = (0,0,1)
  Length = 3
  Length2 = 10
  Profile = -> Sketch007
  ReferenceAxis = -> Sketch007 [N_Axis]
  Refine = true
  Suppressed = false
  Type = 0
FEATURE [PartDesign::Body] Body006  label="plexi-electronics-side-261x210.6-body"
  AllowCompound = false
  Group = -> [Sketch007,Pad006]
  Origin = -> Origin013
  Tip = -> Pad006
FEATURE [App::Part] Part006  label="plexi-electronics-side-261x210.6-part"
  Group = -> [Body006]
  Origin = -> Origin012
FEATURE [Sketcher::SketchObject] Sketch008
  ArcFitTolerance = 1e-06
  AttachmentSupport = -> [XY_Plane015]
  FullyConstrained = true
  MakeInternals = false
  MapMode = 5
  sketch-geometry (5):
    g0: LineSegment StartX=-235.5 StartY=-103.8 StartZ=0 EndX=235.5 EndY=-103.8 EndZ=0
    g1: LineSegment StartX=235.5 StartY=-103.8 StartZ=0 EndX=235.5 EndY=103.8 EndZ=0
    g2: LineSegment StartX=235.5 StartY=103.8 StartZ=0 EndX=-235.5 EndY=103.8 EndZ=0
    g3: LineSegment StartX=-235.5 StartY=103.8 StartZ=0 EndX=-235.5 EndY=-103.8 EndZ=0
    g4: GeomPoint [constr] X=0 Y=0 Z=0
  constraints (12):
    c: Coincident(g0,g1)
    c: Coincident(g1,g2)
    c: Coincident(g2,g3)
    c: Coincident(g3,g0)
    c: Horizontal(g0)
    c: Horizontal(g2)
    c: Vertical(g1)
    c: Vertical(g3)
    c: Symmetric(g2,g0,g4)
    c: Distance(g1,g3) = 471
    c: Distance(g0,g2) = 207.6
    c: Coincident(g4,g-1)
FEATURE [PartDesign::Pad] Pad007
  Direction = (0,0,1)
  Length = 3
  Length2 = 10
  Profile = -> Sketch008
  ReferenceAxis = -> Sketch008 [N_Axis]
  Refine = true
  Suppressed = false
  Type = 0
FEATURE [PartDesign::Body] Body007  label="plexi-electronics-top-471x207.6-body"
  AllowCompound = false
  Group = -> [Sketch008,Pad007]
  Origin = -> Origin015
  Tip = -> Pad007
FEATURE [App::Part] Part007  label="plexi-electronics-top-471x207.6-part"
  Group = -> [Body007]
  Origin = -> Origin014
FEATURE [Sketcher::SketchObject] Sketch009
  ArcFitTolerance = 1e-06
  AttachmentSupport = -> [XY_Plane017]
  FullyConstrained = true
  MakeInternals = false
  MapMode = 5
  sketch-geometry (5):
    g0: LineSegment StartX=-235.5 StartY=-105.3 StartZ=0 EndX=235.5 EndY=-105.3 EndZ=0
    g1: LineSegment StartX=235.5 StartY=-105.3 StartZ=0 EndX=235.5 EndY=105.3 EndZ=0
    g2: LineSegment StartX=235.5 StartY=105.3 StartZ=0 EndX=-235.5 EndY=105.3 EndZ=0
    g3: LineSegment StartX=-235.5 StartY=105.3 StartZ=0 EndX=-235.5 EndY=-105.3 EndZ=0
    g4: GeomPoint [constr] X=0 Y=0 Z=0
  constraints (12):
    c: Coincident(g0,g1)
    c: Coincident(g1,g2)
    c: Coincident(g2,g3)
    c: Coincident(g3,g0)
    c: Horizontal(g0)
    c: Horizontal(g2)
    c: Vertical(g1)
    c: Vertical(g3)
    c: Symmetric(g2,g0,g4)
    c: Distance(g1,g3) = 471
    c: Distance(g0,g2) = 210.6
    c: Coincident(g4,g-1)
FEATURE [PartDesign::Pad] Pad008
  Direction = (0,0,1)
  Length = 3
  Length2 = 10
  Profile = -> Sketch009
  ReferenceAxis = -> Sketch009 [N_Axis]
  Refine = true
  Suppressed = false
  Type = 0
FEATURE [PartDesign::Body] Body008  label="plexi-electronics-bottom-471x210.6-body"
  AllowCompound = false
  Group = -> [Sketch009,Pad008]
  Origin = -> Origin017
  Tip = -> Pad008
FEATURE [App::Part] Part008  label="plexi-electronics-bottom-471x210.6-part"
  Group = -> [Body008]
  Origin = -> Origin016
FEATURE [Sketcher::SketchObject] Sketch010
  ArcFitTolerance = 1e-06
  AttachmentSupport = -> [XY_Plane019]
  FullyConstrained = true
  MakeInternals = false
  MapMode = 5
  sketch-geometry (5):
    g0: LineSegment StartX=-130.5 StartY=-235.5 StartZ=0 EndX=130.5 EndY=-235.5 EndZ=0
    g1: LineSegment StartX=130.5 StartY=-235.5 StartZ=0 EndX=130.5 EndY=235.5 EndZ=0
    g2: LineSegment StartX=130.5 StartY=235.5 StartZ=0 EndX=-130.5 EndY=235.5 EndZ=0
    g3: LineSegment StartX=-130.5 StartY=235.5 StartZ=0 EndX=-130.5 EndY=-235.5 EndZ=0
    g4: GeomPoint [constr] X=0 Y=0 Z=0
  constraints (12):
    c: Coincident(g0,g1)
    c: Coincident(g1,g2)
    c: Coincident(g2,g3)
    c: Coincident(g3,g0)
    c: Horizontal(g0)
    c: Horizontal(g2)
    c: Vertical(g1)
    c: Vertical(g3)
    c: Symmetric(g2,g0,g4)
    c: Distance(g1,g3) = 261
    c: Distance(g0,g2) = 471
    c: Coincident(g4,g-1)
FEATURE [PartDesign::Pad] Pad009
  Direction = (0,0,1)
  Length = 3
  Length2 = 10
  Profile = -> Sketch010
  ReferenceAxis = -> Sketch010 [N_Axis]
  Refine = true
  Suppressed = false
  Type = 0
FEATURE [PartDesign::Body] Body009  label="plexi-electronics-front-471x261-body"
  AllowCompound = false
  Group = -> [Sketch010,Pad009]
  Origin = -> Origin019
  Tip = -> Pad009
FEATURE [App::Part] Part009  label="plexi-electronics-front-471x261-part"
  Group = -> [Body009]
  Origin = -> Origin018
